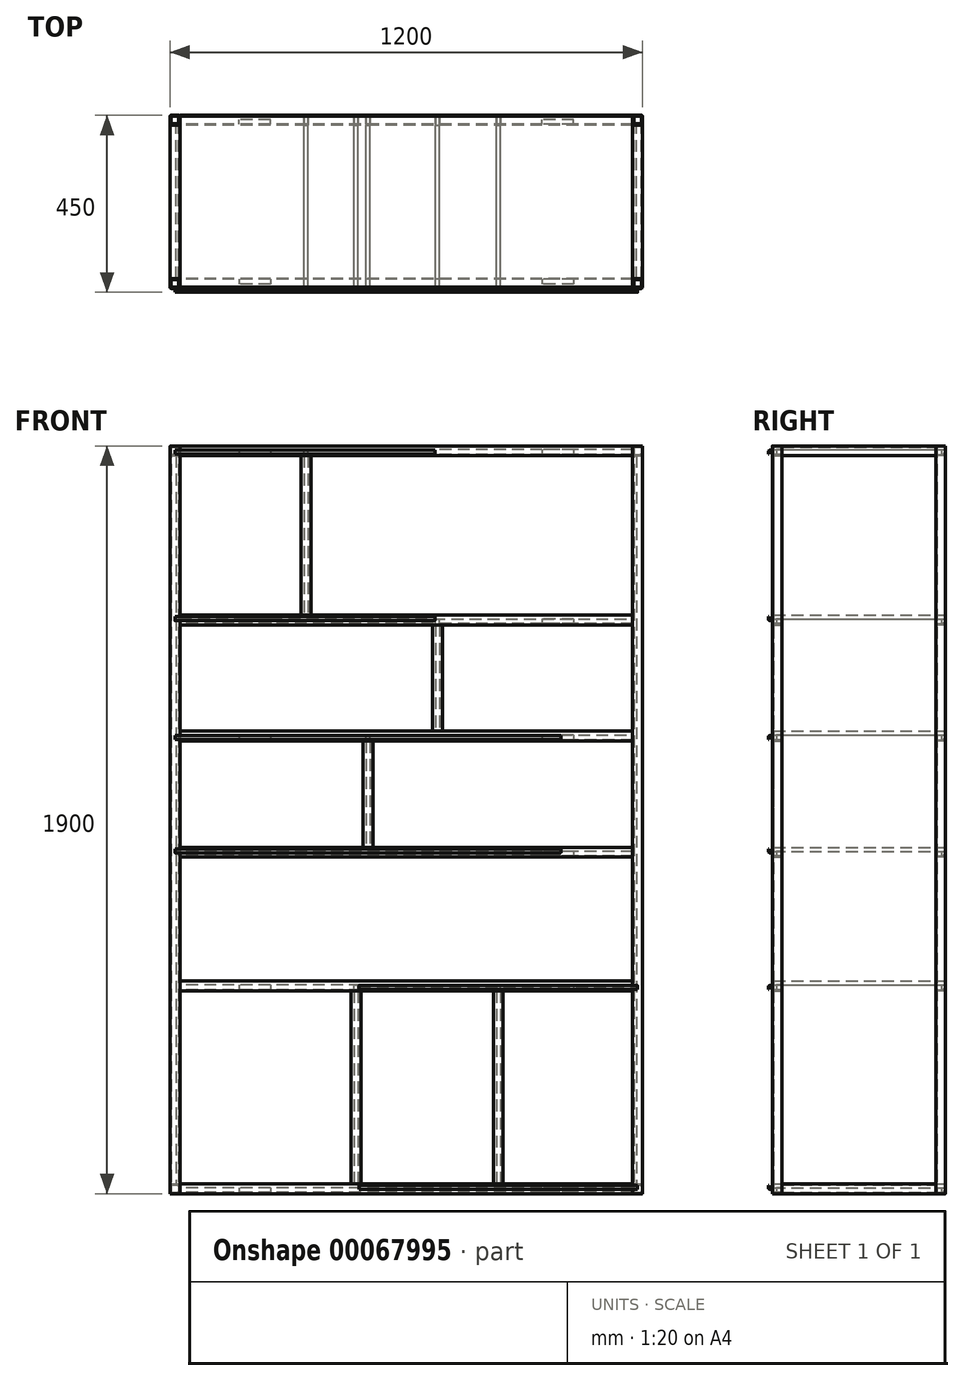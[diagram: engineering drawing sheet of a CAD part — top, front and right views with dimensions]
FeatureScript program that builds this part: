
annotation { "Feature Type Name" : "Feature", "Feature Type Description" : "" }
export const myFeature = defineFeature(function(context is Context, id is Id, definition is map)
    precondition{}
    {
        {
            var Q0;
            Q0=qCreatedBy(makeId("Top.planeOp"),FACE);
            var sketch = newSketch(context, id + "F0", { "sketchPlane" : qUnion([Q0])});
            skLineSegment(sketch, "E0.bottom", {"start": v(-9.5, 12.5) * mm, "end": v(9.5, 12.5) * mm});
            skLineSegment(sketch, "E0.top", {"start": v(-9.5, -12.5) * mm, "end": v(9.5, -12.5) * mm});
            skLineSegment(sketch, "E0.left", {"start": v(-12.5, 9.5) * mm, "end": v(-12.5, -9.5) * mm});
            skLineSegment(sketch, "E0.right", {"start": v(12.5, 9.5) * mm, "end": v(12.5, -9.5) * mm});
            skLineSegment(sketch, "E1.bottom", {"start": v(-6.5, 9.5) * mm, "end": v(6.5, 9.5) * mm});
            skLineSegment(sketch, "E1.top", {"start": v(-6.5, -9.5) * mm, "end": v(6.5, -9.5) * mm});
            skLineSegment(sketch, "E1.left", {"start": v(-9.5, 6.5) * mm, "end": v(-9.5, -6.5) * mm});
            skLineSegment(sketch, "E1.right", {"start": v(9.5, 6.5) * mm, "end": v(9.5, -6.5) * mm});
            skPoint(sketch, "E2.visualSharp", {"position": v(-12.5, 12.5) * mm});
            skArc(sketch, "E2.filletArc", {"start": v(-9.5, 12.5) * mm, "mid": v(-11.62, 11.62) * mm, "end": v(-12.5, 9.5) * mm});
            skPoint(sketch, "E3.visualSharp", {"position": v(12.5, 12.5) * mm});
            skArc(sketch, "E3.filletArc", {"start": v(12.5, 9.5) * mm, "mid": v(11.62, 11.62) * mm, "end": v(9.5, 12.5) * mm});
            skPoint(sketch, "E4.visualSharp", {"position": v(12.5, -12.5) * mm});
            skArc(sketch, "E4.filletArc", {"start": v(9.5, -12.5) * mm, "mid": v(11.62, -11.62) * mm, "end": v(12.5, -9.5) * mm});
            skPoint(sketch, "E5.visualSharp", {"position": v(-12.5, -12.5) * mm});
            skArc(sketch, "E5.filletArc", {"start": v(-12.5, -9.5) * mm, "mid": v(-11.62, -11.62) * mm, "end": v(-9.5, -12.5) * mm});
            skArc(sketch, "E6.filletArc", {"start": v(-6.5, 9.5) * mm, "mid": v(-8.62, 8.62) * mm, "end": v(-9.5, 6.5) * mm});
            skArc(sketch, "E7.filletArc", {"start": v(6.5, -9.5) * mm, "mid": v(8.62, -8.62) * mm, "end": v(9.5, -6.5) * mm});
            skArc(sketch, "E8.filletArc", {"start": v(9.5, 6.5) * mm, "mid": v(8.62, 8.62) * mm, "end": v(6.5, 9.5) * mm});
            skArc(sketch, "E9.filletArc", {"start": v(-9.5, -6.5) * mm, "mid": v(-8.62, -8.62) * mm, "end": v(-6.5, -9.5) * mm});
            skSolve(sketch);
        }
        {
            var Q0;
            Q0=makeQuery(id+"F0.imprint","IMPRINT",FACE,{"disambiguationData":[TD([[makeQuery(id+"F0.imprint","IMPRINT",EDGE,{"derivedFrom":sQuery(id+"F0.wireOp",EDGE,"E0.bottom")}),-1.0]])]});
            extrude(context, id + "F1", {"entities" : qUnion([Q0]), "depth" : 1900 * mm});
        }
        {
            var Q0;
            Q0=makeQuery(id+"F1.opExtrude","SWEPT_BODY",BODY,{"disambiguationData":[OSD([sQuery(id+"F0.wireOp",EDGE,"E0.bottom"),sQuery(id+"F0.wireOp",EDGE,"E0.top"),sQuery(id+"F0.wireOp",EDGE,"E0.left"),sQuery(id+"F0.wireOp",EDGE,"E0.right"),sQuery(id+"F0.wireOp",EDGE,"E1.bottom"),sQuery(id+"F0.wireOp",EDGE,"E1.top"),sQuery(id+"F0.wireOp",EDGE,"E1.left"),sQuery(id+"F0.wireOp",EDGE,"E1.right"),sQuery(id+"F0.wireOp",EDGE,"E2.filletArc"),sQuery(id+"F0.wireOp",EDGE,"E3.filletArc"),sQuery(id+"F0.wireOp",EDGE,"E4.filletArc"),sQuery(id+"F0.wireOp",EDGE,"E5.filletArc"),sQuery(id+"F0.wireOp",EDGE,"E6.filletArc"),sQuery(id+"F0.wireOp",EDGE,"E7.filletArc"),sQuery(id+"F0.wireOp",EDGE,"E8.filletArc"),sQuery(id+"F0.wireOp",EDGE,"E9.filletArc")])]});
            transform(context, id + "F2", {"entities" : qUnion([Q0]), "transformType" : TransformType.TRANSLATION_3D, "dx" : 415 * mm, "dy" : 0 * mm, "dz" : 0 * mm, "makeCopy" : true});
        }
        {
            var Q0;
            Q0=makeQuery(id+"F1.opExtrude","SWEPT_BODY",BODY,{"disambiguationData":[OSD([sQuery(id+"F0.wireOp",EDGE,"E0.bottom"),sQuery(id+"F0.wireOp",EDGE,"E0.top"),sQuery(id+"F0.wireOp",EDGE,"E0.left"),sQuery(id+"F0.wireOp",EDGE,"E0.right"),sQuery(id+"F0.wireOp",EDGE,"E1.bottom"),sQuery(id+"F0.wireOp",EDGE,"E1.top"),sQuery(id+"F0.wireOp",EDGE,"E1.left"),sQuery(id+"F0.wireOp",EDGE,"E1.right"),sQuery(id+"F0.wireOp",EDGE,"E2.filletArc"),sQuery(id+"F0.wireOp",EDGE,"E3.filletArc"),sQuery(id+"F0.wireOp",EDGE,"E4.filletArc"),sQuery(id+"F0.wireOp",EDGE,"E5.filletArc"),sQuery(id+"F0.wireOp",EDGE,"E6.filletArc"),sQuery(id+"F0.wireOp",EDGE,"E7.filletArc"),sQuery(id+"F0.wireOp",EDGE,"E8.filletArc"),sQuery(id+"F0.wireOp",EDGE,"E9.filletArc")])]});
            var Q1;
            Q1=makeQuery(id+"F2.opPattern","COPY",BODY,{"derivedFrom":makeQuery(id+"F1.opExtrude","SWEPT_BODY",BODY,{"disambiguationData":[OSD([sQuery(id+"F0.wireOp",EDGE,"E0.bottom"),sQuery(id+"F0.wireOp",EDGE,"E0.top"),sQuery(id+"F0.wireOp",EDGE,"E0.left"),sQuery(id+"F0.wireOp",EDGE,"E0.right"),sQuery(id+"F0.wireOp",EDGE,"E1.bottom"),sQuery(id+"F0.wireOp",EDGE,"E1.top"),sQuery(id+"F0.wireOp",EDGE,"E1.left"),sQuery(id+"F0.wireOp",EDGE,"E1.right"),sQuery(id+"F0.wireOp",EDGE,"E2.filletArc"),sQuery(id+"F0.wireOp",EDGE,"E3.filletArc"),sQuery(id+"F0.wireOp",EDGE,"E4.filletArc"),sQuery(id+"F0.wireOp",EDGE,"E5.filletArc"),sQuery(id+"F0.wireOp",EDGE,"E6.filletArc"),sQuery(id+"F0.wireOp",EDGE,"E7.filletArc"),sQuery(id+"F0.wireOp",EDGE,"E8.filletArc"),sQuery(id+"F0.wireOp",EDGE,"E9.filletArc")])]}),"instanceName":"1"});
            transform(context, id + "F3", {"entities" : qUnion([Q0, Q1]), "transformType" : TransformType.TRANSLATION_3D, "dx" : 0 * mm, "dy" : 1175 * mm, "dz" : 0 * mm, "makeCopy" : true});
        }
        {
            var Q0;
            Q0=makeQuery(id+"F2.opPattern","COPY",FACE,{"derivedFrom":makeQuery(id+"F1.opExtrude","SWEPT_FACE",FACE,{"disambiguationData":[OSD([sQuery(id+"F0.wireOp",EDGE,"E0.left")])]}),"instanceName":"1"});
            var sketch = newSketch(context, id + "F4", { "sketchPlane" : qUnion([Q0])});
            skSolve(sketch);
        }
        {
            var Q0;
            {var subQ0=sQuery(id+"F0.wireOp",EDGE,"E0.left");Q0=makeQuery(id+"F4.imprint","IMPRINT",FACE,{"disambiguationData":[TD([[makeQuery(id+"F4.imprint","IMPRINT",EDGE,{"derivedFrom":makeQuery(id+"F2.opPattern","COPY",EDGE,{"derivedFrom":makeQuery(id+"F1.opExtrude","CAP_EDGE",EDGE,{"disambiguationData":[OSD([subQ0])],"isStart":true}),"instanceName":"1"})}),1.0]])]});}
            var sketch = newSketch(context, id + "F5", { "sketchPlane" : qUnion([Q0])});
            skLineSegment(sketch, "E10.bottom", {"start": v(-9.5, 1900) * mm, "end": v(9.5, 1900) * mm});
            skLineSegment(sketch, "E10.top", {"start": v(-9.5, 1875) * mm, "end": v(9.5, 1875) * mm});
            skLineSegment(sketch, "E10.left", {"start": v(-12.5, 1897) * mm, "end": v(-12.5, 1878) * mm});
            skLineSegment(sketch, "E10.right", {"start": v(12.5, 1897) * mm, "end": v(12.5, 1878) * mm});
            skLineSegment(sketch, "E11.bottom", {"start": v(-6.5, 1897) * mm, "end": v(6.5, 1897) * mm});
            skLineSegment(sketch, "E11.top", {"start": v(-6.5, 1878) * mm, "end": v(6.5, 1878) * mm});
            skLineSegment(sketch, "E11.left", {"start": v(-9.5, 1894) * mm, "end": v(-9.5, 1881) * mm});
            skLineSegment(sketch, "E11.right", {"start": v(9.5, 1894) * mm, "end": v(9.5, 1881) * mm});
            skPoint(sketch, "E12.visualSharp", {"position": v(-12.5, 1900) * mm});
            skArc(sketch, "E12.filletArc", {"start": v(-9.5, 1900) * mm, "mid": v(-11.62, 1899.12) * mm, "end": v(-12.5, 1897) * mm});
            skPoint(sketch, "E13.visualSharp", {"position": v(12.5, 1900) * mm});
            skArc(sketch, "E13.filletArc", {"start": v(12.5, 1897) * mm, "mid": v(11.62, 1899.12) * mm, "end": v(9.5, 1900) * mm});
            skPoint(sketch, "E14.visualSharp", {"position": v(12.5, 1875) * mm});
            skArc(sketch, "E14.filletArc", {"start": v(9.5, 1875) * mm, "mid": v(11.62, 1875.88) * mm, "end": v(12.5, 1878) * mm});
            skPoint(sketch, "E15.visualSharp", {"position": v(-12.5, 1875) * mm});
            skArc(sketch, "E15.filletArc", {"start": v(-12.5, 1878) * mm, "mid": v(-11.62, 1875.88) * mm, "end": v(-9.5, 1875) * mm});
            skArc(sketch, "E16.filletArc", {"start": v(-9.5, 1881) * mm, "mid": v(-8.62, 1878.88) * mm, "end": v(-6.5, 1878) * mm});
            skArc(sketch, "E17.filletArc", {"start": v(-6.5, 1897) * mm, "mid": v(-8.62, 1896.12) * mm, "end": v(-9.5, 1894) * mm});
            skArc(sketch, "E18.filletArc", {"start": v(9.5, 1894) * mm, "mid": v(8.62, 1896.12) * mm, "end": v(6.5, 1897) * mm});
            skArc(sketch, "E19.filletArc", {"start": v(6.5, 1878) * mm, "mid": v(8.62, 1878.88) * mm, "end": v(9.5, 1881) * mm});
            skSolve(sketch);
        }
        {
            var Q0;
            {var subQ2=sQuery(id+"F5.wireOp",EDGE,"E10.bottom");Q0=makeQuery(id+"F5.imprint","IMPRINT",FACE,{"disambiguationData":[TD([[makeQuery(id+"F5.imprint","IMPRINT",EDGE,{"derivedFrom":subQ2}),-1.0]])]});}
            var Q1;
            Q1=makeQuery(id+"F5.imprint","IMPRINT",FACE,{"disambiguationData":[TD([[makeQuery(id+"F5.imprint","IMPRINT",EDGE,{"derivedFrom":sQuery(id+"F5.wireOp",EDGE,"E10.right")}),-1.0]])]});
            var Q2;
            {var subQ2=sQuery(id+"F5.wireOp",EDGE,"E10.top");Q2=makeQuery(id+"F5.imprint","IMPRINT",FACE,{"disambiguationData":[TD([[makeQuery(id+"F5.imprint","IMPRINT",EDGE,{"derivedFrom":subQ2}),1.0]])]});}
            var Q3;
            Q3=makeQuery(id+"F5.imprint","IMPRINT",FACE,{"disambiguationData":[TD([[makeQuery(id+"F5.imprint","IMPRINT",EDGE,{"derivedFrom":sQuery(id+"F5.wireOp",EDGE,"E10.left")}),1.0]])]});
            extrude(context, id + "F6", {"entities" : qUnion([Q0, Q1, Q2, Q3]), "depth" : 390 * mm});
        }
        {
            var Q0;
            Q0=makeQuery(id+"F6.opExtrude","SWEPT_BODY",BODY,{"disambiguationData":[OSD([sQuery(id+"F5.wireOp",EDGE,"E10.bottom"),sQuery(id+"F5.wireOp",EDGE,"E10.top"),sQuery(id+"F5.wireOp",EDGE,"E10.left"),sQuery(id+"F5.wireOp",EDGE,"E10.right"),sQuery(id+"F5.wireOp",EDGE,"E11.bottom"),sQuery(id+"F5.wireOp",EDGE,"E11.top"),sQuery(id+"F5.wireOp",EDGE,"E11.left"),sQuery(id+"F5.wireOp",EDGE,"E11.right"),sQuery(id+"F5.wireOp",EDGE,"E12.filletArc"),sQuery(id+"F5.wireOp",EDGE,"E13.filletArc"),sQuery(id+"F5.wireOp",EDGE,"E14.filletArc"),sQuery(id+"F5.wireOp",EDGE,"E15.filletArc"),sQuery(id+"F5.wireOp",EDGE,"E16.filletArc"),sQuery(id+"F5.wireOp",EDGE,"E17.filletArc"),sQuery(id+"F5.wireOp",EDGE,"E18.filletArc"),sQuery(id+"F5.wireOp",EDGE,"E19.filletArc")])]});
            transform(context, id + "F7", {"entities" : qUnion([Q0]), "transformType" : TransformType.TRANSLATION_3D, "dx" : 0 * mm, "dy" : 1175 * mm, "dz" : 0 * mm, "makeCopy" : true});
        }
        {
            var Q0;
            Q0=makeQuery(id+"F6.opExtrude","SWEPT_BODY",BODY,{"disambiguationData":[OSD([sQuery(id+"F5.wireOp",EDGE,"E10.bottom"),sQuery(id+"F5.wireOp",EDGE,"E10.top"),sQuery(id+"F5.wireOp",EDGE,"E10.left"),sQuery(id+"F5.wireOp",EDGE,"E10.right"),sQuery(id+"F5.wireOp",EDGE,"E11.bottom"),sQuery(id+"F5.wireOp",EDGE,"E11.top"),sQuery(id+"F5.wireOp",EDGE,"E11.left"),sQuery(id+"F5.wireOp",EDGE,"E11.right"),sQuery(id+"F5.wireOp",EDGE,"E12.filletArc"),sQuery(id+"F5.wireOp",EDGE,"E13.filletArc"),sQuery(id+"F5.wireOp",EDGE,"E14.filletArc"),sQuery(id+"F5.wireOp",EDGE,"E15.filletArc"),sQuery(id+"F5.wireOp",EDGE,"E16.filletArc"),sQuery(id+"F5.wireOp",EDGE,"E17.filletArc"),sQuery(id+"F5.wireOp",EDGE,"E18.filletArc"),sQuery(id+"F5.wireOp",EDGE,"E19.filletArc")])]});
            var Q1;
            Q1=makeQuery(id+"F7.opPattern","COPY",BODY,{"derivedFrom":makeQuery(id+"F6.opExtrude","SWEPT_BODY",BODY,{"disambiguationData":[OSD([sQuery(id+"F5.wireOp",EDGE,"E10.bottom"),sQuery(id+"F5.wireOp",EDGE,"E10.top"),sQuery(id+"F5.wireOp",EDGE,"E10.left"),sQuery(id+"F5.wireOp",EDGE,"E10.right"),sQuery(id+"F5.wireOp",EDGE,"E11.bottom"),sQuery(id+"F5.wireOp",EDGE,"E11.top"),sQuery(id+"F5.wireOp",EDGE,"E11.left"),sQuery(id+"F5.wireOp",EDGE,"E11.right"),sQuery(id+"F5.wireOp",EDGE,"E12.filletArc"),sQuery(id+"F5.wireOp",EDGE,"E13.filletArc"),sQuery(id+"F5.wireOp",EDGE,"E14.filletArc"),sQuery(id+"F5.wireOp",EDGE,"E15.filletArc"),sQuery(id+"F5.wireOp",EDGE,"E16.filletArc"),sQuery(id+"F5.wireOp",EDGE,"E17.filletArc"),sQuery(id+"F5.wireOp",EDGE,"E18.filletArc"),sQuery(id+"F5.wireOp",EDGE,"E19.filletArc")])]}),"instanceName":"1"});
            transform(context, id + "F8", {"entities" : qUnion([Q0, Q1]), "transformType" : TransformType.TRANSLATION_3D, "dx" : 0 * mm, "dy" : 0 * mm, "dz" : -1875 * mm, "makeCopy" : true});
        }
        {
            var Q0;
            Q0=makeQuery(id+"F2.opPattern","COPY",FACE,{"derivedFrom":makeQuery(id+"F1.opExtrude","SWEPT_FACE",FACE,{"disambiguationData":[OSD([sQuery(id+"F0.wireOp",EDGE,"E0.bottom")])]}),"instanceName":"1"});
            var sketch = newSketch(context, id + "F9", { "sketchPlane" : qUnion([Q0])});
            skLineSegment(sketch, "E20", {"start": v(-427.5, 1900) * mm, "end": v(-427.5, 1875) * mm});
            skLineSegment(sketch, "E21", {"start": v(-427.5, 1875) * mm, "end": v(-402.5, 1875) * mm});
            skLineSegment(sketch, "E22", {"start": v(-402.5, 1875) * mm, "end": v(-402.5, 1876) * mm});
            skLineSegment(sketch, "E23", {"start": v(-404.5, 1878) * mm, "end": v(-419.5, 1878) * mm});
            skLineSegment(sketch, "E24", {"start": v(-424.5, 1883) * mm, "end": v(-424.5, 1898) * mm});
            skLineSegment(sketch, "E25", {"start": v(-426.5, 1900) * mm, "end": v(-427.5, 1900) * mm});
            skPoint(sketch, "E26.visualSharp", {"position": v(-424.5, 1878) * mm});
            skArc(sketch, "E26.filletArc", {"start": v(-424.5, 1883) * mm, "mid": v(-423.04, 1879.46) * mm, "end": v(-419.5, 1878) * mm});
            skPoint(sketch, "E27.visualSharp", {"position": v(-424.5, 1900) * mm});
            skArc(sketch, "E27.filletArc", {"start": v(-424.5, 1898) * mm, "mid": v(-425.09, 1899.41) * mm, "end": v(-426.5, 1900) * mm});
            skPoint(sketch, "E28.visualSharp", {"position": v(-402.5, 1878) * mm});
            skArc(sketch, "E28.filletArc", {"start": v(-402.5, 1876) * mm, "mid": v(-403.09, 1877.41) * mm, "end": v(-404.5, 1878) * mm});
            skSolve(sketch);
        }
        {
            var Q0;
            {var subQ4=sQuery(id+"F9.wireOp",EDGE,"E22");Q0=makeQuery(id+"F9.imprint","IMPRINT",FACE,{"disambiguationData":[TD([[makeQuery(id+"F9.imprint","IMPRINT",EDGE,{"derivedFrom":subQ4}),1.0]])]});}
            var Q1;
            {var subQ0=sQuery(id+"F9.wireOp",EDGE,"E26.filletArc");Q1=makeQuery(id+"F9.imprint","IMPRINT",FACE,{"disambiguationData":[TD([[makeQuery(id+"F9.imprint","IMPRINT",EDGE,{"derivedFrom":subQ0}),-1.0]])]});}
            var Q2;
            {var subQ4=sQuery(id+"F9.wireOp",EDGE,"E20");Q2=makeQuery(id+"F9.imprint","IMPRINT",FACE,{"disambiguationData":[TD([[makeQuery(id+"F9.imprint","IMPRINT",EDGE,{"derivedFrom":subQ4}),1.0]])]});}
            extrude(context, id + "F10", {"entities" : qUnion([Q0, Q1, Q2]), "depth" : 1150 * mm});
        }
        {
            var Q0;
            Q0=makeQuery(id+"F10.opExtrude","SWEPT_BODY",BODY,{"disambiguationData":[OSD([sQuery(id+"F9.wireOp",EDGE,"E20"),sQuery(id+"F9.wireOp",EDGE,"E21"),sQuery(id+"F9.wireOp",EDGE,"E22"),sQuery(id+"F9.wireOp",EDGE,"E23"),sQuery(id+"F9.wireOp",EDGE,"E24"),sQuery(id+"F9.wireOp",EDGE,"E25"),sQuery(id+"F9.wireOp",EDGE,"E26.filletArc"),sQuery(id+"F9.wireOp",EDGE,"E27.filletArc"),sQuery(id+"F9.wireOp",EDGE,"E28.filletArc")])]});
            var Q1;
            Q1=makeQuery(id+"F10.opExtrude","SWEPT_FACE",FACE,{"disambiguationData":[OSD([sQuery(id+"F9.wireOp",EDGE,"E22")])]});
            mirror(context, id + "F11", {"entities" : qUnion([Q0]), "mirrorPlane" : qUnion([Q1])});
        }
        {
            var Q0;
            Q0=makeQuery(id+"F11.opPattern","COPY",BODY,{"derivedFrom":makeQuery(id+"F10.opExtrude","SWEPT_BODY",BODY,{"disambiguationData":[OSD([sQuery(id+"F9.wireOp",EDGE,"E20"),sQuery(id+"F9.wireOp",EDGE,"E21"),sQuery(id+"F9.wireOp",EDGE,"E22"),sQuery(id+"F9.wireOp",EDGE,"E23"),sQuery(id+"F9.wireOp",EDGE,"E24"),sQuery(id+"F9.wireOp",EDGE,"E25"),sQuery(id+"F9.wireOp",EDGE,"E26.filletArc"),sQuery(id+"F9.wireOp",EDGE,"E27.filletArc"),sQuery(id+"F9.wireOp",EDGE,"E28.filletArc")])]}),"instanceName":"1"});
            transform(context, id + "F12", {"entities" : qUnion([Q0]), "transformType" : TransformType.TRANSLATION_3D, "dx" : -390 * mm, "dy" : 0 * mm, "dz" : 0 * mm, "makeCopy" : false});
        }
        {
            var Q0;
            Q0=makeQuery(id+"F10.opExtrude","SWEPT_BODY",BODY,{"disambiguationData":[OSD([sQuery(id+"F9.wireOp",EDGE,"E20"),sQuery(id+"F9.wireOp",EDGE,"E21"),sQuery(id+"F9.wireOp",EDGE,"E22"),sQuery(id+"F9.wireOp",EDGE,"E23"),sQuery(id+"F9.wireOp",EDGE,"E24"),sQuery(id+"F9.wireOp",EDGE,"E25"),sQuery(id+"F9.wireOp",EDGE,"E26.filletArc"),sQuery(id+"F9.wireOp",EDGE,"E27.filletArc"),sQuery(id+"F9.wireOp",EDGE,"E28.filletArc")])]});
            var Q1;
            Q1=makeQuery(id+"F11.opPattern","COPY",BODY,{"derivedFrom":makeQuery(id+"F10.opExtrude","SWEPT_BODY",BODY,{"disambiguationData":[OSD([sQuery(id+"F9.wireOp",EDGE,"E20"),sQuery(id+"F9.wireOp",EDGE,"E21"),sQuery(id+"F9.wireOp",EDGE,"E22"),sQuery(id+"F9.wireOp",EDGE,"E23"),sQuery(id+"F9.wireOp",EDGE,"E24"),sQuery(id+"F9.wireOp",EDGE,"E25"),sQuery(id+"F9.wireOp",EDGE,"E26.filletArc"),sQuery(id+"F9.wireOp",EDGE,"E27.filletArc"),sQuery(id+"F9.wireOp",EDGE,"E28.filletArc")])]}),"instanceName":"1"});
            transform(context, id + "F13", {"entities" : qUnion([Q0, Q1]), "transformType" : TransformType.TRANSLATION_3D, "dx" : 0 * mm, "dy" : 0 * mm, "dz" : -1875 * mm, "makeCopy" : false});
        }
        {
            var Q0;
            Q0=makeQuery(id+"F10.opExtrude","SWEPT_BODY",BODY,{"disambiguationData":[OSD([sQuery(id+"F9.wireOp",EDGE,"E20"),sQuery(id+"F9.wireOp",EDGE,"E21"),sQuery(id+"F9.wireOp",EDGE,"E22"),sQuery(id+"F9.wireOp",EDGE,"E23"),sQuery(id+"F9.wireOp",EDGE,"E24"),sQuery(id+"F9.wireOp",EDGE,"E25"),sQuery(id+"F9.wireOp",EDGE,"E26.filletArc"),sQuery(id+"F9.wireOp",EDGE,"E27.filletArc"),sQuery(id+"F9.wireOp",EDGE,"E28.filletArc")])]});
            var Q1;
            Q1=makeQuery(id+"F11.opPattern","COPY",BODY,{"derivedFrom":makeQuery(id+"F10.opExtrude","SWEPT_BODY",BODY,{"disambiguationData":[OSD([sQuery(id+"F9.wireOp",EDGE,"E20"),sQuery(id+"F9.wireOp",EDGE,"E21"),sQuery(id+"F9.wireOp",EDGE,"E22"),sQuery(id+"F9.wireOp",EDGE,"E23"),sQuery(id+"F9.wireOp",EDGE,"E24"),sQuery(id+"F9.wireOp",EDGE,"E25"),sQuery(id+"F9.wireOp",EDGE,"E26.filletArc"),sQuery(id+"F9.wireOp",EDGE,"E27.filletArc"),sQuery(id+"F9.wireOp",EDGE,"E28.filletArc")])]}),"instanceName":"1"});
            transform(context, id + "F14", {"entities" : qUnion([Q0, Q1]), "transformType" : TransformType.TRANSLATION_3D, "dx" : 0 * mm, "dy" : 0 * mm, "dz" : 515 * mm, "makeCopy" : true});
        }
        {
            var Q0;
            Q0=makeQuery(id+"F14.opPattern","COPY",BODY,{"derivedFrom":makeQuery(id+"F10.opExtrude","SWEPT_BODY",BODY,{"disambiguationData":[OSD([sQuery(id+"F9.wireOp",EDGE,"E20"),sQuery(id+"F9.wireOp",EDGE,"E21"),sQuery(id+"F9.wireOp",EDGE,"E22"),sQuery(id+"F9.wireOp",EDGE,"E23"),sQuery(id+"F9.wireOp",EDGE,"E24"),sQuery(id+"F9.wireOp",EDGE,"E25"),sQuery(id+"F9.wireOp",EDGE,"E26.filletArc"),sQuery(id+"F9.wireOp",EDGE,"E27.filletArc"),sQuery(id+"F9.wireOp",EDGE,"E28.filletArc")])]}),"instanceName":"1"});
            var Q1;
            Q1=makeQuery(id+"F14.opPattern","COPY",BODY,{"derivedFrom":makeQuery(id+"F11.opPattern","COPY",BODY,{"derivedFrom":makeQuery(id+"F10.opExtrude","SWEPT_BODY",BODY,{"disambiguationData":[OSD([sQuery(id+"F9.wireOp",EDGE,"E20"),sQuery(id+"F9.wireOp",EDGE,"E21"),sQuery(id+"F9.wireOp",EDGE,"E22"),sQuery(id+"F9.wireOp",EDGE,"E23"),sQuery(id+"F9.wireOp",EDGE,"E24"),sQuery(id+"F9.wireOp",EDGE,"E25"),sQuery(id+"F9.wireOp",EDGE,"E26.filletArc"),sQuery(id+"F9.wireOp",EDGE,"E27.filletArc"),sQuery(id+"F9.wireOp",EDGE,"E28.filletArc")])]}),"instanceName":"1"}),"instanceName":"1"});
            transform(context, id + "F15", {"entities" : qUnion([Q0, Q1]), "transformType" : TransformType.TRANSLATION_3D, "dx" : 0 * mm, "dy" : 0 * mm, "dz" : 340 * mm, "makeCopy" : true});
        }
        {
            var Q0;
            Q0=makeQuery(id+"F15.opPattern","COPY",BODY,{"derivedFrom":makeQuery(id+"F14.opPattern","COPY",BODY,{"derivedFrom":makeQuery(id+"F10.opExtrude","SWEPT_BODY",BODY,{"disambiguationData":[OSD([sQuery(id+"F9.wireOp",EDGE,"E20"),sQuery(id+"F9.wireOp",EDGE,"E21"),sQuery(id+"F9.wireOp",EDGE,"E22"),sQuery(id+"F9.wireOp",EDGE,"E23"),sQuery(id+"F9.wireOp",EDGE,"E24"),sQuery(id+"F9.wireOp",EDGE,"E25"),sQuery(id+"F9.wireOp",EDGE,"E26.filletArc"),sQuery(id+"F9.wireOp",EDGE,"E27.filletArc"),sQuery(id+"F9.wireOp",EDGE,"E28.filletArc")])]}),"instanceName":"1"}),"instanceName":"1"});
            var Q1;
            Q1=makeQuery(id+"F15.opPattern","COPY",BODY,{"derivedFrom":makeQuery(id+"F14.opPattern","COPY",BODY,{"derivedFrom":makeQuery(id+"F11.opPattern","COPY",BODY,{"derivedFrom":makeQuery(id+"F10.opExtrude","SWEPT_BODY",BODY,{"disambiguationData":[OSD([sQuery(id+"F9.wireOp",EDGE,"E20"),sQuery(id+"F9.wireOp",EDGE,"E21"),sQuery(id+"F9.wireOp",EDGE,"E22"),sQuery(id+"F9.wireOp",EDGE,"E23"),sQuery(id+"F9.wireOp",EDGE,"E24"),sQuery(id+"F9.wireOp",EDGE,"E25"),sQuery(id+"F9.wireOp",EDGE,"E26.filletArc"),sQuery(id+"F9.wireOp",EDGE,"E27.filletArc"),sQuery(id+"F9.wireOp",EDGE,"E28.filletArc")])]}),"instanceName":"1"}),"instanceName":"1"}),"instanceName":"1"});
            transform(context, id + "F16", {"entities" : qUnion([Q0, Q1]), "transformType" : TransformType.TRANSLATION_3D, "dx" : 0 * mm, "dy" : 0 * mm, "dz" : 295 * mm, "makeCopy" : true});
        }
        {
            var Q0;
            Q0=makeQuery(id+"F16.opPattern","COPY",BODY,{"derivedFrom":makeQuery(id+"F15.opPattern","COPY",BODY,{"derivedFrom":makeQuery(id+"F14.opPattern","COPY",BODY,{"derivedFrom":makeQuery(id+"F10.opExtrude","SWEPT_BODY",BODY,{"disambiguationData":[OSD([sQuery(id+"F9.wireOp",EDGE,"E20"),sQuery(id+"F9.wireOp",EDGE,"E21"),sQuery(id+"F9.wireOp",EDGE,"E22"),sQuery(id+"F9.wireOp",EDGE,"E23"),sQuery(id+"F9.wireOp",EDGE,"E24"),sQuery(id+"F9.wireOp",EDGE,"E25"),sQuery(id+"F9.wireOp",EDGE,"E26.filletArc"),sQuery(id+"F9.wireOp",EDGE,"E27.filletArc"),sQuery(id+"F9.wireOp",EDGE,"E28.filletArc")])]}),"instanceName":"1"}),"instanceName":"1"}),"instanceName":"1"});
            var Q1;
            Q1=makeQuery(id+"F16.opPattern","COPY",BODY,{"derivedFrom":makeQuery(id+"F15.opPattern","COPY",BODY,{"derivedFrom":makeQuery(id+"F14.opPattern","COPY",BODY,{"derivedFrom":makeQuery(id+"F11.opPattern","COPY",BODY,{"derivedFrom":makeQuery(id+"F10.opExtrude","SWEPT_BODY",BODY,{"disambiguationData":[OSD([sQuery(id+"F9.wireOp",EDGE,"E20"),sQuery(id+"F9.wireOp",EDGE,"E21"),sQuery(id+"F9.wireOp",EDGE,"E22"),sQuery(id+"F9.wireOp",EDGE,"E23"),sQuery(id+"F9.wireOp",EDGE,"E24"),sQuery(id+"F9.wireOp",EDGE,"E25"),sQuery(id+"F9.wireOp",EDGE,"E26.filletArc"),sQuery(id+"F9.wireOp",EDGE,"E27.filletArc"),sQuery(id+"F9.wireOp",EDGE,"E28.filletArc")])]}),"instanceName":"1"}),"instanceName":"1"}),"instanceName":"1"}),"instanceName":"1"});
            transform(context, id + "F17", {"entities" : qUnion([Q0, Q1]), "transformType" : TransformType.TRANSLATION_3D, "dx" : 0 * mm, "dy" : 0 * mm, "dz" : 295 * mm, "makeCopy" : true});
        }
        {
            var Q0;
            Q0=makeQuery(id+"F17.opPattern","COPY",BODY,{"derivedFrom":makeQuery(id+"F16.opPattern","COPY",BODY,{"derivedFrom":makeQuery(id+"F15.opPattern","COPY",BODY,{"derivedFrom":makeQuery(id+"F14.opPattern","COPY",BODY,{"derivedFrom":makeQuery(id+"F10.opExtrude","SWEPT_BODY",BODY,{"disambiguationData":[OSD([sQuery(id+"F9.wireOp",EDGE,"E20"),sQuery(id+"F9.wireOp",EDGE,"E21"),sQuery(id+"F9.wireOp",EDGE,"E22"),sQuery(id+"F9.wireOp",EDGE,"E23"),sQuery(id+"F9.wireOp",EDGE,"E24"),sQuery(id+"F9.wireOp",EDGE,"E25"),sQuery(id+"F9.wireOp",EDGE,"E26.filletArc"),sQuery(id+"F9.wireOp",EDGE,"E27.filletArc"),sQuery(id+"F9.wireOp",EDGE,"E28.filletArc")])]}),"instanceName":"1"}),"instanceName":"1"}),"instanceName":"1"}),"instanceName":"1"});
            var Q1;
            Q1=makeQuery(id+"F17.opPattern","COPY",BODY,{"derivedFrom":makeQuery(id+"F16.opPattern","COPY",BODY,{"derivedFrom":makeQuery(id+"F15.opPattern","COPY",BODY,{"derivedFrom":makeQuery(id+"F14.opPattern","COPY",BODY,{"derivedFrom":makeQuery(id+"F11.opPattern","COPY",BODY,{"derivedFrom":makeQuery(id+"F10.opExtrude","SWEPT_BODY",BODY,{"disambiguationData":[OSD([sQuery(id+"F9.wireOp",EDGE,"E20"),sQuery(id+"F9.wireOp",EDGE,"E21"),sQuery(id+"F9.wireOp",EDGE,"E22"),sQuery(id+"F9.wireOp",EDGE,"E23"),sQuery(id+"F9.wireOp",EDGE,"E24"),sQuery(id+"F9.wireOp",EDGE,"E25"),sQuery(id+"F9.wireOp",EDGE,"E26.filletArc"),sQuery(id+"F9.wireOp",EDGE,"E27.filletArc"),sQuery(id+"F9.wireOp",EDGE,"E28.filletArc")])]}),"instanceName":"1"}),"instanceName":"1"}),"instanceName":"1"}),"instanceName":"1"}),"instanceName":"1"});
            transform(context, id + "F18", {"entities" : qUnion([Q0, Q1]), "transformType" : TransformType.TRANSLATION_3D, "dx" : 0 * mm, "dy" : 0 * mm, "dz" : 430 * mm, "makeCopy" : true});
        }
        {
            var Q0;
            Q0=makeQuery(id+"F1.opExtrude","SWEPT_FACE",FACE,{"disambiguationData":[OSD([sQuery(id+"F0.wireOp",EDGE,"E0.bottom")])]});
            var sketch = newSketch(context, id + "F19", { "sketchPlane" : qUnion([Q0])});
            skLineSegment(sketch, "E29.bottom", {"start": v(-10.5, 1890) * mm, "end": v(4.5, 1890) * mm});
            skLineSegment(sketch, "E29.top", {"start": v(-10.5, 1878) * mm, "end": v(4.5, 1878) * mm});
            skLineSegment(sketch, "E29.left", {"start": v(-10.5, 1890) * mm, "end": v(-10.5, 1878) * mm});
            skLineSegment(sketch, "E29.right", {"start": v(4.5, 1890) * mm, "end": v(4.5, 1878) * mm});
            skSolve(sketch);
        }
        {
            var Q0;
            {var subQ0=sQuery(id+"F19.wireOp",EDGE,"E29.right");Q0=makeQuery(id+"F19.imprint","IMPRINT",FACE,{"disambiguationData":[TD([[makeQuery(id+"F19.imprint","IMPRINT",EDGE,{"derivedFrom":subQ0}),-1.0]])]});}
            var Q1;
            {var subQ0=sQuery(id+"F19.wireOp",EDGE,"E29.left");Q1=makeQuery(id+"F19.imprint","IMPRINT",FACE,{"disambiguationData":[TD([[makeQuery(id+"F19.imprint","IMPRINT",EDGE,{"derivedFrom":subQ0}),1.0]])]});}
            extrude(context, id + "F20", {"entities" : qUnion([Q0, Q1]), "depth" : 60 * mm});
        }
        {
            var Q0;
            Q0=makeQuery(id+"F20.opExtrude","SWEPT_BODY",BODY,{"disambiguationData":[OSD([sQuery(id+"F19.wireOp",EDGE,"E29.bottom"),sQuery(id+"F19.wireOp",EDGE,"E29.top"),sQuery(id+"F19.wireOp",EDGE,"E29.left"),sQuery(id+"F19.wireOp",EDGE,"E29.right")])]});
            transform(context, id + "F21", {"entities" : qUnion([Q0]), "transformType" : TransformType.TRANSLATION_3D, "dx" : 0 * mm, "dy" : 1090 * mm, "dz" : 0 * mm, "makeCopy" : true});
        }
        {
            var Q0;
            Q0=makeQuery(id+"F20.opExtrude","SWEPT_BODY",BODY,{"disambiguationData":[OSD([sQuery(id+"F19.wireOp",EDGE,"E29.bottom"),sQuery(id+"F19.wireOp",EDGE,"E29.top"),sQuery(id+"F19.wireOp",EDGE,"E29.left"),sQuery(id+"F19.wireOp",EDGE,"E29.right")])]});
            transform(context, id + "F22", {"entities" : qUnion([Q0]), "transformType" : TransformType.TRANSLATION_3D, "dx" : 0 * mm, "dy" : 363 * mm, "dz" : 0 * mm, "makeCopy" : true});
        }
        {
            var Q0;
            Q0=makeQuery(id+"F21.opPattern","COPY",BODY,{"derivedFrom":makeQuery(id+"F20.opExtrude","SWEPT_BODY",BODY,{"disambiguationData":[OSD([sQuery(id+"F19.wireOp",EDGE,"E29.bottom"),sQuery(id+"F19.wireOp",EDGE,"E29.top"),sQuery(id+"F19.wireOp",EDGE,"E29.left"),sQuery(id+"F19.wireOp",EDGE,"E29.right")])]}),"instanceName":"1"});
            transform(context, id + "F23", {"entities" : qUnion([Q0]), "transformType" : TransformType.TRANSLATION_3D, "dx" : 0 * mm, "dy" : -363 * mm, "dz" : 0 * mm, "makeCopy" : true});
        }
        {
            var Q0;
            Q0=makeQuery(id+"F22.opPattern","COPY",BODY,{"derivedFrom":makeQuery(id+"F20.opExtrude","SWEPT_BODY",BODY,{"disambiguationData":[OSD([sQuery(id+"F19.wireOp",EDGE,"E29.bottom"),sQuery(id+"F19.wireOp",EDGE,"E29.top"),sQuery(id+"F19.wireOp",EDGE,"E29.left"),sQuery(id+"F19.wireOp",EDGE,"E29.right")])]}),"instanceName":"1"});
            var Q1;
            Q1=makeQuery(id+"F20.opExtrude","SWEPT_BODY",BODY,{"disambiguationData":[OSD([sQuery(id+"F19.wireOp",EDGE,"E29.bottom"),sQuery(id+"F19.wireOp",EDGE,"E29.top"),sQuery(id+"F19.wireOp",EDGE,"E29.left"),sQuery(id+"F19.wireOp",EDGE,"E29.right")])]});
            var Q2;
            Q2=makeQuery(id+"F23.opPattern","COPY",BODY,{"derivedFrom":makeQuery(id+"F21.opPattern","COPY",BODY,{"derivedFrom":makeQuery(id+"F20.opExtrude","SWEPT_BODY",BODY,{"disambiguationData":[OSD([sQuery(id+"F19.wireOp",EDGE,"E29.bottom"),sQuery(id+"F19.wireOp",EDGE,"E29.top"),sQuery(id+"F19.wireOp",EDGE,"E29.left"),sQuery(id+"F19.wireOp",EDGE,"E29.right")])]}),"instanceName":"1"}),"instanceName":"1"});
            var Q3;
            Q3=makeQuery(id+"F21.opPattern","COPY",BODY,{"derivedFrom":makeQuery(id+"F20.opExtrude","SWEPT_BODY",BODY,{"disambiguationData":[OSD([sQuery(id+"F19.wireOp",EDGE,"E29.bottom"),sQuery(id+"F19.wireOp",EDGE,"E29.top"),sQuery(id+"F19.wireOp",EDGE,"E29.left"),sQuery(id+"F19.wireOp",EDGE,"E29.right")])]}),"instanceName":"1"});
            transform(context, id + "F24", {"entities" : qUnion([Q0, Q1, Q2, Q3]), "transformType" : TransformType.TRANSLATION_3D, "dx" : 409 * mm, "dy" : 0 * mm, "dz" : 0 * mm, "makeCopy" : true});
        }
        {
            var Q0;
            Q0=makeQuery(id+"F20.opExtrude","SWEPT_BODY",BODY,{"disambiguationData":[OSD([sQuery(id+"F19.wireOp",EDGE,"E29.bottom"),sQuery(id+"F19.wireOp",EDGE,"E29.top"),sQuery(id+"F19.wireOp",EDGE,"E29.left"),sQuery(id+"F19.wireOp",EDGE,"E29.right")])]});
            var Q1;
            Q1=makeQuery(id+"F22.opPattern","COPY",BODY,{"derivedFrom":makeQuery(id+"F20.opExtrude","SWEPT_BODY",BODY,{"disambiguationData":[OSD([sQuery(id+"F19.wireOp",EDGE,"E29.bottom"),sQuery(id+"F19.wireOp",EDGE,"E29.top"),sQuery(id+"F19.wireOp",EDGE,"E29.left"),sQuery(id+"F19.wireOp",EDGE,"E29.right")])]}),"instanceName":"1"});
            var Q2;
            Q2=makeQuery(id+"F23.opPattern","COPY",BODY,{"derivedFrom":makeQuery(id+"F21.opPattern","COPY",BODY,{"derivedFrom":makeQuery(id+"F20.opExtrude","SWEPT_BODY",BODY,{"disambiguationData":[OSD([sQuery(id+"F19.wireOp",EDGE,"E29.bottom"),sQuery(id+"F19.wireOp",EDGE,"E29.top"),sQuery(id+"F19.wireOp",EDGE,"E29.left"),sQuery(id+"F19.wireOp",EDGE,"E29.right")])]}),"instanceName":"1"}),"instanceName":"1"});
            var Q3;
            Q3=makeQuery(id+"F21.opPattern","COPY",BODY,{"derivedFrom":makeQuery(id+"F20.opExtrude","SWEPT_BODY",BODY,{"disambiguationData":[OSD([sQuery(id+"F19.wireOp",EDGE,"E29.bottom"),sQuery(id+"F19.wireOp",EDGE,"E29.top"),sQuery(id+"F19.wireOp",EDGE,"E29.left"),sQuery(id+"F19.wireOp",EDGE,"E29.right")])]}),"instanceName":"1"});
            var Q4;
            Q4=makeQuery(id+"F24.opPattern","COPY",BODY,{"derivedFrom":makeQuery(id+"F21.opPattern","COPY",BODY,{"derivedFrom":makeQuery(id+"F20.opExtrude","SWEPT_BODY",BODY,{"disambiguationData":[OSD([sQuery(id+"F19.wireOp",EDGE,"E29.bottom"),sQuery(id+"F19.wireOp",EDGE,"E29.top"),sQuery(id+"F19.wireOp",EDGE,"E29.left"),sQuery(id+"F19.wireOp",EDGE,"E29.right")])]}),"instanceName":"1"}),"instanceName":"1"});
            var Q5;
            Q5=makeQuery(id+"F24.opPattern","COPY",BODY,{"derivedFrom":makeQuery(id+"F23.opPattern","COPY",BODY,{"derivedFrom":makeQuery(id+"F21.opPattern","COPY",BODY,{"derivedFrom":makeQuery(id+"F20.opExtrude","SWEPT_BODY",BODY,{"disambiguationData":[OSD([sQuery(id+"F19.wireOp",EDGE,"E29.bottom"),sQuery(id+"F19.wireOp",EDGE,"E29.top"),sQuery(id+"F19.wireOp",EDGE,"E29.left"),sQuery(id+"F19.wireOp",EDGE,"E29.right")])]}),"instanceName":"1"}),"instanceName":"1"}),"instanceName":"1"});
            var Q6;
            Q6=makeQuery(id+"F24.opPattern","COPY",BODY,{"derivedFrom":makeQuery(id+"F22.opPattern","COPY",BODY,{"derivedFrom":makeQuery(id+"F20.opExtrude","SWEPT_BODY",BODY,{"disambiguationData":[OSD([sQuery(id+"F19.wireOp",EDGE,"E29.bottom"),sQuery(id+"F19.wireOp",EDGE,"E29.top"),sQuery(id+"F19.wireOp",EDGE,"E29.left"),sQuery(id+"F19.wireOp",EDGE,"E29.right")])]}),"instanceName":"1"}),"instanceName":"1"});
            var Q7;
            Q7=makeQuery(id+"F24.opPattern","COPY",BODY,{"derivedFrom":makeQuery(id+"F20.opExtrude","SWEPT_BODY",BODY,{"disambiguationData":[OSD([sQuery(id+"F19.wireOp",EDGE,"E29.bottom"),sQuery(id+"F19.wireOp",EDGE,"E29.top"),sQuery(id+"F19.wireOp",EDGE,"E29.left"),sQuery(id+"F19.wireOp",EDGE,"E29.right")])]}),"instanceName":"1"});
            transform(context, id + "F25", {"entities" : qUnion([Q0, Q1, Q2, Q3, Q4, Q5, Q6, Q7]), "transformType" : TransformType.TRANSLATION_3D, "dx" : 0 * mm, "dy" : 0 * mm, "dz" : -430 * mm, "makeCopy" : true});
        }
        {
            var Q0;
            Q0=makeQuery(id+"F25.opPattern","COPY",BODY,{"derivedFrom":makeQuery(id+"F21.opPattern","COPY",BODY,{"derivedFrom":makeQuery(id+"F20.opExtrude","SWEPT_BODY",BODY,{"disambiguationData":[OSD([sQuery(id+"F19.wireOp",EDGE,"E29.bottom"),sQuery(id+"F19.wireOp",EDGE,"E29.top"),sQuery(id+"F19.wireOp",EDGE,"E29.left"),sQuery(id+"F19.wireOp",EDGE,"E29.right")])]}),"instanceName":"1"}),"instanceName":"1"});
            var Q1;
            Q1=makeQuery(id+"F25.opPattern","COPY",BODY,{"derivedFrom":makeQuery(id+"F24.opPattern","COPY",BODY,{"derivedFrom":makeQuery(id+"F21.opPattern","COPY",BODY,{"derivedFrom":makeQuery(id+"F20.opExtrude","SWEPT_BODY",BODY,{"disambiguationData":[OSD([sQuery(id+"F19.wireOp",EDGE,"E29.bottom"),sQuery(id+"F19.wireOp",EDGE,"E29.top"),sQuery(id+"F19.wireOp",EDGE,"E29.left"),sQuery(id+"F19.wireOp",EDGE,"E29.right")])]}),"instanceName":"1"}),"instanceName":"1"}),"instanceName":"1"});
            var Q2;
            Q2=makeQuery(id+"F25.opPattern","COPY",BODY,{"derivedFrom":makeQuery(id+"F23.opPattern","COPY",BODY,{"derivedFrom":makeQuery(id+"F21.opPattern","COPY",BODY,{"derivedFrom":makeQuery(id+"F20.opExtrude","SWEPT_BODY",BODY,{"disambiguationData":[OSD([sQuery(id+"F19.wireOp",EDGE,"E29.bottom"),sQuery(id+"F19.wireOp",EDGE,"E29.top"),sQuery(id+"F19.wireOp",EDGE,"E29.left"),sQuery(id+"F19.wireOp",EDGE,"E29.right")])]}),"instanceName":"1"}),"instanceName":"1"}),"instanceName":"1"});
            var Q3;
            Q3=makeQuery(id+"F25.opPattern","COPY",BODY,{"derivedFrom":makeQuery(id+"F24.opPattern","COPY",BODY,{"derivedFrom":makeQuery(id+"F23.opPattern","COPY",BODY,{"derivedFrom":makeQuery(id+"F21.opPattern","COPY",BODY,{"derivedFrom":makeQuery(id+"F20.opExtrude","SWEPT_BODY",BODY,{"disambiguationData":[OSD([sQuery(id+"F19.wireOp",EDGE,"E29.bottom"),sQuery(id+"F19.wireOp",EDGE,"E29.top"),sQuery(id+"F19.wireOp",EDGE,"E29.left"),sQuery(id+"F19.wireOp",EDGE,"E29.right")])]}),"instanceName":"1"}),"instanceName":"1"}),"instanceName":"1"}),"instanceName":"1"});
            var Q4;
            Q4=makeQuery(id+"F25.opPattern","COPY",BODY,{"derivedFrom":makeQuery(id+"F22.opPattern","COPY",BODY,{"derivedFrom":makeQuery(id+"F20.opExtrude","SWEPT_BODY",BODY,{"disambiguationData":[OSD([sQuery(id+"F19.wireOp",EDGE,"E29.bottom"),sQuery(id+"F19.wireOp",EDGE,"E29.top"),sQuery(id+"F19.wireOp",EDGE,"E29.left"),sQuery(id+"F19.wireOp",EDGE,"E29.right")])]}),"instanceName":"1"}),"instanceName":"1"});
            var Q5;
            Q5=makeQuery(id+"F25.opPattern","COPY",BODY,{"derivedFrom":makeQuery(id+"F24.opPattern","COPY",BODY,{"derivedFrom":makeQuery(id+"F22.opPattern","COPY",BODY,{"derivedFrom":makeQuery(id+"F20.opExtrude","SWEPT_BODY",BODY,{"disambiguationData":[OSD([sQuery(id+"F19.wireOp",EDGE,"E29.bottom"),sQuery(id+"F19.wireOp",EDGE,"E29.top"),sQuery(id+"F19.wireOp",EDGE,"E29.left"),sQuery(id+"F19.wireOp",EDGE,"E29.right")])]}),"instanceName":"1"}),"instanceName":"1"}),"instanceName":"1"});
            var Q6;
            Q6=makeQuery(id+"F25.opPattern","COPY",BODY,{"derivedFrom":makeQuery(id+"F20.opExtrude","SWEPT_BODY",BODY,{"disambiguationData":[OSD([sQuery(id+"F19.wireOp",EDGE,"E29.bottom"),sQuery(id+"F19.wireOp",EDGE,"E29.top"),sQuery(id+"F19.wireOp",EDGE,"E29.left"),sQuery(id+"F19.wireOp",EDGE,"E29.right")])]}),"instanceName":"1"});
            var Q7;
            Q7=makeQuery(id+"F25.opPattern","COPY",BODY,{"derivedFrom":makeQuery(id+"F24.opPattern","COPY",BODY,{"derivedFrom":makeQuery(id+"F20.opExtrude","SWEPT_BODY",BODY,{"disambiguationData":[OSD([sQuery(id+"F19.wireOp",EDGE,"E29.bottom"),sQuery(id+"F19.wireOp",EDGE,"E29.top"),sQuery(id+"F19.wireOp",EDGE,"E29.left"),sQuery(id+"F19.wireOp",EDGE,"E29.right")])]}),"instanceName":"1"}),"instanceName":"1"});
            transform(context, id + "F26", {"entities" : qUnion([Q0, Q1, Q2, Q3, Q4, Q5, Q6, Q7]), "transformType" : TransformType.TRANSLATION_3D, "dx" : 0 * mm, "dy" : 0 * mm, "dz" : -295 * mm, "makeCopy" : true});
        }
        {
            var Q0;
            Q0=makeQuery(id+"F26.opPattern","COPY",BODY,{"derivedFrom":makeQuery(id+"F25.opPattern","COPY",BODY,{"derivedFrom":makeQuery(id+"F21.opPattern","COPY",BODY,{"derivedFrom":makeQuery(id+"F20.opExtrude","SWEPT_BODY",BODY,{"disambiguationData":[OSD([sQuery(id+"F19.wireOp",EDGE,"E29.bottom"),sQuery(id+"F19.wireOp",EDGE,"E29.top"),sQuery(id+"F19.wireOp",EDGE,"E29.left"),sQuery(id+"F19.wireOp",EDGE,"E29.right")])]}),"instanceName":"1"}),"instanceName":"1"}),"instanceName":"1"});
            var Q1;
            Q1=makeQuery(id+"F26.opPattern","COPY",BODY,{"derivedFrom":makeQuery(id+"F25.opPattern","COPY",BODY,{"derivedFrom":makeQuery(id+"F24.opPattern","COPY",BODY,{"derivedFrom":makeQuery(id+"F21.opPattern","COPY",BODY,{"derivedFrom":makeQuery(id+"F20.opExtrude","SWEPT_BODY",BODY,{"disambiguationData":[OSD([sQuery(id+"F19.wireOp",EDGE,"E29.bottom"),sQuery(id+"F19.wireOp",EDGE,"E29.top"),sQuery(id+"F19.wireOp",EDGE,"E29.left"),sQuery(id+"F19.wireOp",EDGE,"E29.right")])]}),"instanceName":"1"}),"instanceName":"1"}),"instanceName":"1"}),"instanceName":"1"});
            var Q2;
            Q2=makeQuery(id+"F26.opPattern","COPY",BODY,{"derivedFrom":makeQuery(id+"F25.opPattern","COPY",BODY,{"derivedFrom":makeQuery(id+"F23.opPattern","COPY",BODY,{"derivedFrom":makeQuery(id+"F21.opPattern","COPY",BODY,{"derivedFrom":makeQuery(id+"F20.opExtrude","SWEPT_BODY",BODY,{"disambiguationData":[OSD([sQuery(id+"F19.wireOp",EDGE,"E29.bottom"),sQuery(id+"F19.wireOp",EDGE,"E29.top"),sQuery(id+"F19.wireOp",EDGE,"E29.left"),sQuery(id+"F19.wireOp",EDGE,"E29.right")])]}),"instanceName":"1"}),"instanceName":"1"}),"instanceName":"1"}),"instanceName":"1"});
            var Q3;
            Q3=makeQuery(id+"F26.opPattern","COPY",BODY,{"derivedFrom":makeQuery(id+"F25.opPattern","COPY",BODY,{"derivedFrom":makeQuery(id+"F24.opPattern","COPY",BODY,{"derivedFrom":makeQuery(id+"F23.opPattern","COPY",BODY,{"derivedFrom":makeQuery(id+"F21.opPattern","COPY",BODY,{"derivedFrom":makeQuery(id+"F20.opExtrude","SWEPT_BODY",BODY,{"disambiguationData":[OSD([sQuery(id+"F19.wireOp",EDGE,"E29.bottom"),sQuery(id+"F19.wireOp",EDGE,"E29.top"),sQuery(id+"F19.wireOp",EDGE,"E29.left"),sQuery(id+"F19.wireOp",EDGE,"E29.right")])]}),"instanceName":"1"}),"instanceName":"1"}),"instanceName":"1"}),"instanceName":"1"}),"instanceName":"1"});
            var Q4;
            Q4=makeQuery(id+"F26.opPattern","COPY",BODY,{"derivedFrom":makeQuery(id+"F25.opPattern","COPY",BODY,{"derivedFrom":makeQuery(id+"F22.opPattern","COPY",BODY,{"derivedFrom":makeQuery(id+"F20.opExtrude","SWEPT_BODY",BODY,{"disambiguationData":[OSD([sQuery(id+"F19.wireOp",EDGE,"E29.bottom"),sQuery(id+"F19.wireOp",EDGE,"E29.top"),sQuery(id+"F19.wireOp",EDGE,"E29.left"),sQuery(id+"F19.wireOp",EDGE,"E29.right")])]}),"instanceName":"1"}),"instanceName":"1"}),"instanceName":"1"});
            var Q5;
            Q5=makeQuery(id+"F26.opPattern","COPY",BODY,{"derivedFrom":makeQuery(id+"F25.opPattern","COPY",BODY,{"derivedFrom":makeQuery(id+"F24.opPattern","COPY",BODY,{"derivedFrom":makeQuery(id+"F22.opPattern","COPY",BODY,{"derivedFrom":makeQuery(id+"F20.opExtrude","SWEPT_BODY",BODY,{"disambiguationData":[OSD([sQuery(id+"F19.wireOp",EDGE,"E29.bottom"),sQuery(id+"F19.wireOp",EDGE,"E29.top"),sQuery(id+"F19.wireOp",EDGE,"E29.left"),sQuery(id+"F19.wireOp",EDGE,"E29.right")])]}),"instanceName":"1"}),"instanceName":"1"}),"instanceName":"1"}),"instanceName":"1"});
            var Q6;
            Q6=makeQuery(id+"F26.opPattern","COPY",BODY,{"derivedFrom":makeQuery(id+"F25.opPattern","COPY",BODY,{"derivedFrom":makeQuery(id+"F20.opExtrude","SWEPT_BODY",BODY,{"disambiguationData":[OSD([sQuery(id+"F19.wireOp",EDGE,"E29.bottom"),sQuery(id+"F19.wireOp",EDGE,"E29.top"),sQuery(id+"F19.wireOp",EDGE,"E29.left"),sQuery(id+"F19.wireOp",EDGE,"E29.right")])]}),"instanceName":"1"}),"instanceName":"1"});
            var Q7;
            Q7=makeQuery(id+"F26.opPattern","COPY",BODY,{"derivedFrom":makeQuery(id+"F25.opPattern","COPY",BODY,{"derivedFrom":makeQuery(id+"F24.opPattern","COPY",BODY,{"derivedFrom":makeQuery(id+"F20.opExtrude","SWEPT_BODY",BODY,{"disambiguationData":[OSD([sQuery(id+"F19.wireOp",EDGE,"E29.bottom"),sQuery(id+"F19.wireOp",EDGE,"E29.top"),sQuery(id+"F19.wireOp",EDGE,"E29.left"),sQuery(id+"F19.wireOp",EDGE,"E29.right")])]}),"instanceName":"1"}),"instanceName":"1"}),"instanceName":"1"});
            transform(context, id + "F27", {"entities" : qUnion([Q0, Q1, Q2, Q3, Q4, Q5, Q6, Q7]), "transformType" : TransformType.TRANSLATION_3D, "dx" : 0 * mm, "dy" : 0 * mm, "dz" : -295 * mm, "makeCopy" : true});
        }
        {
            var Q0;
            Q0=makeQuery(id+"F27.opPattern","COPY",BODY,{"derivedFrom":makeQuery(id+"F26.opPattern","COPY",BODY,{"derivedFrom":makeQuery(id+"F25.opPattern","COPY",BODY,{"derivedFrom":makeQuery(id+"F21.opPattern","COPY",BODY,{"derivedFrom":makeQuery(id+"F20.opExtrude","SWEPT_BODY",BODY,{"disambiguationData":[OSD([sQuery(id+"F19.wireOp",EDGE,"E29.bottom"),sQuery(id+"F19.wireOp",EDGE,"E29.top"),sQuery(id+"F19.wireOp",EDGE,"E29.left"),sQuery(id+"F19.wireOp",EDGE,"E29.right")])]}),"instanceName":"1"}),"instanceName":"1"}),"instanceName":"1"}),"instanceName":"1"});
            var Q1;
            Q1=makeQuery(id+"F27.opPattern","COPY",BODY,{"derivedFrom":makeQuery(id+"F26.opPattern","COPY",BODY,{"derivedFrom":makeQuery(id+"F25.opPattern","COPY",BODY,{"derivedFrom":makeQuery(id+"F24.opPattern","COPY",BODY,{"derivedFrom":makeQuery(id+"F21.opPattern","COPY",BODY,{"derivedFrom":makeQuery(id+"F20.opExtrude","SWEPT_BODY",BODY,{"disambiguationData":[OSD([sQuery(id+"F19.wireOp",EDGE,"E29.bottom"),sQuery(id+"F19.wireOp",EDGE,"E29.top"),sQuery(id+"F19.wireOp",EDGE,"E29.left"),sQuery(id+"F19.wireOp",EDGE,"E29.right")])]}),"instanceName":"1"}),"instanceName":"1"}),"instanceName":"1"}),"instanceName":"1"}),"instanceName":"1"});
            var Q2;
            Q2=makeQuery(id+"F27.opPattern","COPY",BODY,{"derivedFrom":makeQuery(id+"F26.opPattern","COPY",BODY,{"derivedFrom":makeQuery(id+"F25.opPattern","COPY",BODY,{"derivedFrom":makeQuery(id+"F23.opPattern","COPY",BODY,{"derivedFrom":makeQuery(id+"F21.opPattern","COPY",BODY,{"derivedFrom":makeQuery(id+"F20.opExtrude","SWEPT_BODY",BODY,{"disambiguationData":[OSD([sQuery(id+"F19.wireOp",EDGE,"E29.bottom"),sQuery(id+"F19.wireOp",EDGE,"E29.top"),sQuery(id+"F19.wireOp",EDGE,"E29.left"),sQuery(id+"F19.wireOp",EDGE,"E29.right")])]}),"instanceName":"1"}),"instanceName":"1"}),"instanceName":"1"}),"instanceName":"1"}),"instanceName":"1"});
            var Q3;
            Q3=makeQuery(id+"F27.opPattern","COPY",BODY,{"derivedFrom":makeQuery(id+"F26.opPattern","COPY",BODY,{"derivedFrom":makeQuery(id+"F25.opPattern","COPY",BODY,{"derivedFrom":makeQuery(id+"F24.opPattern","COPY",BODY,{"derivedFrom":makeQuery(id+"F23.opPattern","COPY",BODY,{"derivedFrom":makeQuery(id+"F21.opPattern","COPY",BODY,{"derivedFrom":makeQuery(id+"F20.opExtrude","SWEPT_BODY",BODY,{"disambiguationData":[OSD([sQuery(id+"F19.wireOp",EDGE,"E29.bottom"),sQuery(id+"F19.wireOp",EDGE,"E29.top"),sQuery(id+"F19.wireOp",EDGE,"E29.left"),sQuery(id+"F19.wireOp",EDGE,"E29.right")])]}),"instanceName":"1"}),"instanceName":"1"}),"instanceName":"1"}),"instanceName":"1"}),"instanceName":"1"}),"instanceName":"1"});
            var Q4;
            Q4=makeQuery(id+"F27.opPattern","COPY",BODY,{"derivedFrom":makeQuery(id+"F26.opPattern","COPY",BODY,{"derivedFrom":makeQuery(id+"F25.opPattern","COPY",BODY,{"derivedFrom":makeQuery(id+"F22.opPattern","COPY",BODY,{"derivedFrom":makeQuery(id+"F20.opExtrude","SWEPT_BODY",BODY,{"disambiguationData":[OSD([sQuery(id+"F19.wireOp",EDGE,"E29.bottom"),sQuery(id+"F19.wireOp",EDGE,"E29.top"),sQuery(id+"F19.wireOp",EDGE,"E29.left"),sQuery(id+"F19.wireOp",EDGE,"E29.right")])]}),"instanceName":"1"}),"instanceName":"1"}),"instanceName":"1"}),"instanceName":"1"});
            var Q5;
            Q5=makeQuery(id+"F27.opPattern","COPY",BODY,{"derivedFrom":makeQuery(id+"F26.opPattern","COPY",BODY,{"derivedFrom":makeQuery(id+"F25.opPattern","COPY",BODY,{"derivedFrom":makeQuery(id+"F24.opPattern","COPY",BODY,{"derivedFrom":makeQuery(id+"F22.opPattern","COPY",BODY,{"derivedFrom":makeQuery(id+"F20.opExtrude","SWEPT_BODY",BODY,{"disambiguationData":[OSD([sQuery(id+"F19.wireOp",EDGE,"E29.bottom"),sQuery(id+"F19.wireOp",EDGE,"E29.top"),sQuery(id+"F19.wireOp",EDGE,"E29.left"),sQuery(id+"F19.wireOp",EDGE,"E29.right")])]}),"instanceName":"1"}),"instanceName":"1"}),"instanceName":"1"}),"instanceName":"1"}),"instanceName":"1"});
            var Q6;
            Q6=makeQuery(id+"F27.opPattern","COPY",BODY,{"derivedFrom":makeQuery(id+"F26.opPattern","COPY",BODY,{"derivedFrom":makeQuery(id+"F25.opPattern","COPY",BODY,{"derivedFrom":makeQuery(id+"F20.opExtrude","SWEPT_BODY",BODY,{"disambiguationData":[OSD([sQuery(id+"F19.wireOp",EDGE,"E29.bottom"),sQuery(id+"F19.wireOp",EDGE,"E29.top"),sQuery(id+"F19.wireOp",EDGE,"E29.left"),sQuery(id+"F19.wireOp",EDGE,"E29.right")])]}),"instanceName":"1"}),"instanceName":"1"}),"instanceName":"1"});
            var Q7;
            Q7=makeQuery(id+"F27.opPattern","COPY",BODY,{"derivedFrom":makeQuery(id+"F26.opPattern","COPY",BODY,{"derivedFrom":makeQuery(id+"F25.opPattern","COPY",BODY,{"derivedFrom":makeQuery(id+"F24.opPattern","COPY",BODY,{"derivedFrom":makeQuery(id+"F20.opExtrude","SWEPT_BODY",BODY,{"disambiguationData":[OSD([sQuery(id+"F19.wireOp",EDGE,"E29.bottom"),sQuery(id+"F19.wireOp",EDGE,"E29.top"),sQuery(id+"F19.wireOp",EDGE,"E29.left"),sQuery(id+"F19.wireOp",EDGE,"E29.right")])]}),"instanceName":"1"}),"instanceName":"1"}),"instanceName":"1"}),"instanceName":"1"});
            transform(context, id + "F28", {"entities" : qUnion([Q0, Q1, Q2, Q3, Q4, Q5, Q6, Q7]), "transformType" : TransformType.TRANSLATION_3D, "dx" : 0 * mm, "dy" : 0 * mm, "dz" : -340 * mm, "makeCopy" : true});
        }
        {
            var Q0;
            Q0=makeQuery(id+"F28.opPattern","COPY",BODY,{"derivedFrom":makeQuery(id+"F27.opPattern","COPY",BODY,{"derivedFrom":makeQuery(id+"F26.opPattern","COPY",BODY,{"derivedFrom":makeQuery(id+"F25.opPattern","COPY",BODY,{"derivedFrom":makeQuery(id+"F21.opPattern","COPY",BODY,{"derivedFrom":makeQuery(id+"F20.opExtrude","SWEPT_BODY",BODY,{"disambiguationData":[OSD([sQuery(id+"F19.wireOp",EDGE,"E29.bottom"),sQuery(id+"F19.wireOp",EDGE,"E29.top"),sQuery(id+"F19.wireOp",EDGE,"E29.left"),sQuery(id+"F19.wireOp",EDGE,"E29.right")])]}),"instanceName":"1"}),"instanceName":"1"}),"instanceName":"1"}),"instanceName":"1"}),"instanceName":"1"});
            var Q1;
            Q1=makeQuery(id+"F28.opPattern","COPY",BODY,{"derivedFrom":makeQuery(id+"F27.opPattern","COPY",BODY,{"derivedFrom":makeQuery(id+"F26.opPattern","COPY",BODY,{"derivedFrom":makeQuery(id+"F25.opPattern","COPY",BODY,{"derivedFrom":makeQuery(id+"F24.opPattern","COPY",BODY,{"derivedFrom":makeQuery(id+"F21.opPattern","COPY",BODY,{"derivedFrom":makeQuery(id+"F20.opExtrude","SWEPT_BODY",BODY,{"disambiguationData":[OSD([sQuery(id+"F19.wireOp",EDGE,"E29.bottom"),sQuery(id+"F19.wireOp",EDGE,"E29.top"),sQuery(id+"F19.wireOp",EDGE,"E29.left"),sQuery(id+"F19.wireOp",EDGE,"E29.right")])]}),"instanceName":"1"}),"instanceName":"1"}),"instanceName":"1"}),"instanceName":"1"}),"instanceName":"1"}),"instanceName":"1"});
            var Q2;
            Q2=makeQuery(id+"F28.opPattern","COPY",BODY,{"derivedFrom":makeQuery(id+"F27.opPattern","COPY",BODY,{"derivedFrom":makeQuery(id+"F26.opPattern","COPY",BODY,{"derivedFrom":makeQuery(id+"F25.opPattern","COPY",BODY,{"derivedFrom":makeQuery(id+"F23.opPattern","COPY",BODY,{"derivedFrom":makeQuery(id+"F21.opPattern","COPY",BODY,{"derivedFrom":makeQuery(id+"F20.opExtrude","SWEPT_BODY",BODY,{"disambiguationData":[OSD([sQuery(id+"F19.wireOp",EDGE,"E29.bottom"),sQuery(id+"F19.wireOp",EDGE,"E29.top"),sQuery(id+"F19.wireOp",EDGE,"E29.left"),sQuery(id+"F19.wireOp",EDGE,"E29.right")])]}),"instanceName":"1"}),"instanceName":"1"}),"instanceName":"1"}),"instanceName":"1"}),"instanceName":"1"}),"instanceName":"1"});
            var Q3;
            Q3=makeQuery(id+"F28.opPattern","COPY",BODY,{"derivedFrom":makeQuery(id+"F27.opPattern","COPY",BODY,{"derivedFrom":makeQuery(id+"F26.opPattern","COPY",BODY,{"derivedFrom":makeQuery(id+"F25.opPattern","COPY",BODY,{"derivedFrom":makeQuery(id+"F24.opPattern","COPY",BODY,{"derivedFrom":makeQuery(id+"F23.opPattern","COPY",BODY,{"derivedFrom":makeQuery(id+"F21.opPattern","COPY",BODY,{"derivedFrom":makeQuery(id+"F20.opExtrude","SWEPT_BODY",BODY,{"disambiguationData":[OSD([sQuery(id+"F19.wireOp",EDGE,"E29.bottom"),sQuery(id+"F19.wireOp",EDGE,"E29.top"),sQuery(id+"F19.wireOp",EDGE,"E29.left"),sQuery(id+"F19.wireOp",EDGE,"E29.right")])]}),"instanceName":"1"}),"instanceName":"1"}),"instanceName":"1"}),"instanceName":"1"}),"instanceName":"1"}),"instanceName":"1"}),"instanceName":"1"});
            var Q4;
            Q4=makeQuery(id+"F28.opPattern","COPY",BODY,{"derivedFrom":makeQuery(id+"F27.opPattern","COPY",BODY,{"derivedFrom":makeQuery(id+"F26.opPattern","COPY",BODY,{"derivedFrom":makeQuery(id+"F25.opPattern","COPY",BODY,{"derivedFrom":makeQuery(id+"F22.opPattern","COPY",BODY,{"derivedFrom":makeQuery(id+"F20.opExtrude","SWEPT_BODY",BODY,{"disambiguationData":[OSD([sQuery(id+"F19.wireOp",EDGE,"E29.bottom"),sQuery(id+"F19.wireOp",EDGE,"E29.top"),sQuery(id+"F19.wireOp",EDGE,"E29.left"),sQuery(id+"F19.wireOp",EDGE,"E29.right")])]}),"instanceName":"1"}),"instanceName":"1"}),"instanceName":"1"}),"instanceName":"1"}),"instanceName":"1"});
            var Q5;
            Q5=makeQuery(id+"F28.opPattern","COPY",BODY,{"derivedFrom":makeQuery(id+"F27.opPattern","COPY",BODY,{"derivedFrom":makeQuery(id+"F26.opPattern","COPY",BODY,{"derivedFrom":makeQuery(id+"F25.opPattern","COPY",BODY,{"derivedFrom":makeQuery(id+"F24.opPattern","COPY",BODY,{"derivedFrom":makeQuery(id+"F22.opPattern","COPY",BODY,{"derivedFrom":makeQuery(id+"F20.opExtrude","SWEPT_BODY",BODY,{"disambiguationData":[OSD([sQuery(id+"F19.wireOp",EDGE,"E29.bottom"),sQuery(id+"F19.wireOp",EDGE,"E29.top"),sQuery(id+"F19.wireOp",EDGE,"E29.left"),sQuery(id+"F19.wireOp",EDGE,"E29.right")])]}),"instanceName":"1"}),"instanceName":"1"}),"instanceName":"1"}),"instanceName":"1"}),"instanceName":"1"}),"instanceName":"1"});
            var Q6;
            Q6=makeQuery(id+"F28.opPattern","COPY",BODY,{"derivedFrom":makeQuery(id+"F27.opPattern","COPY",BODY,{"derivedFrom":makeQuery(id+"F26.opPattern","COPY",BODY,{"derivedFrom":makeQuery(id+"F25.opPattern","COPY",BODY,{"derivedFrom":makeQuery(id+"F20.opExtrude","SWEPT_BODY",BODY,{"disambiguationData":[OSD([sQuery(id+"F19.wireOp",EDGE,"E29.bottom"),sQuery(id+"F19.wireOp",EDGE,"E29.top"),sQuery(id+"F19.wireOp",EDGE,"E29.left"),sQuery(id+"F19.wireOp",EDGE,"E29.right")])]}),"instanceName":"1"}),"instanceName":"1"}),"instanceName":"1"}),"instanceName":"1"});
            var Q7;
            Q7=makeQuery(id+"F28.opPattern","COPY",BODY,{"derivedFrom":makeQuery(id+"F27.opPattern","COPY",BODY,{"derivedFrom":makeQuery(id+"F26.opPattern","COPY",BODY,{"derivedFrom":makeQuery(id+"F25.opPattern","COPY",BODY,{"derivedFrom":makeQuery(id+"F24.opPattern","COPY",BODY,{"derivedFrom":makeQuery(id+"F20.opExtrude","SWEPT_BODY",BODY,{"disambiguationData":[OSD([sQuery(id+"F19.wireOp",EDGE,"E29.bottom"),sQuery(id+"F19.wireOp",EDGE,"E29.top"),sQuery(id+"F19.wireOp",EDGE,"E29.left"),sQuery(id+"F19.wireOp",EDGE,"E29.right")])]}),"instanceName":"1"}),"instanceName":"1"}),"instanceName":"1"}),"instanceName":"1"}),"instanceName":"1"});
            transform(context, id + "F29", {"entities" : qUnion([Q0, Q1, Q2, Q3, Q4, Q5, Q6, Q7]), "transformType" : TransformType.TRANSLATION_3D, "dx" : 0 * mm, "dy" : 0 * mm, "dz" : -515 * mm, "makeCopy" : true});
        }
        {
            var Q0;
            Q0=makeQuery(id+"F17.opPattern","COPY",FACE,{"derivedFrom":makeQuery(id+"F16.opPattern","COPY",FACE,{"derivedFrom":makeQuery(id+"F15.opPattern","COPY",FACE,{"derivedFrom":makeQuery(id+"F14.opPattern","COPY",FACE,{"derivedFrom":makeQuery(id+"F11.opPattern","COPY",FACE,{"derivedFrom":makeQuery(id+"F10.opExtrude","SWEPT_FACE",FACE,{"disambiguationData":[OSD([sQuery(id+"F9.wireOp",EDGE,"E25")])]}),"instanceName":"1"}),"instanceName":"1"}),"instanceName":"1"}),"instanceName":"1"}),"instanceName":"1"});
            var sketch = newSketch(context, id + "F30", { "sketchPlane" : qUnion([Q0])});
            skLineSegment(sketch, "E30.bottom", {"start": v(-12.5, 854.5) * mm, "end": v(-9.5, 854.5) * mm});
            skLineSegment(sketch, "E30.top", {"start": v(-12.5, 829.5) * mm, "end": v(-9.5, 829.5) * mm});
            skLineSegment(sketch, "E30.left", {"start": v(-12.5, 854.5) * mm, "end": v(-12.5, 829.5) * mm});
            skLineSegment(sketch, "E30.right", {"start": v(-9.5, 854.5) * mm, "end": v(-9.5, 829.5) * mm});
            skSolve(sketch);
        }
        {
            var Q0;
            {var subQ0=sQuery(id+"F30.wireOp",EDGE,"E30.left");Q0=makeQuery(id+"F30.imprint","IMPRINT",FACE,{"disambiguationData":[TD([[makeQuery(id+"F30.imprint","IMPRINT",EDGE,{"derivedFrom":subQ0}),1.0]])]});}
            var Q1;
            {var subQ0=sQuery(id+"F30.wireOp",EDGE,"E30.right");Q1=makeQuery(id+"F30.imprint","IMPRINT",FACE,{"disambiguationData":[TD([[makeQuery(id+"F30.imprint","IMPRINT",EDGE,{"derivedFrom":subQ0}),-1.0]])]});}
            extrude(context, id + "F31", {"entities" : qUnion([Q0, Q1]), "depth" : 405 * mm});
        }
        {
            var Q0;
            Q0=makeQuery(id+"F16.opPattern","COPY",FACE,{"derivedFrom":makeQuery(id+"F15.opPattern","COPY",FACE,{"derivedFrom":makeQuery(id+"F14.opPattern","COPY",FACE,{"derivedFrom":makeQuery(id+"F11.opPattern","COPY",FACE,{"derivedFrom":makeQuery(id+"F10.opExtrude","SWEPT_FACE",FACE,{"disambiguationData":[OSD([sQuery(id+"F9.wireOp",EDGE,"E25")])]}),"instanceName":"1"}),"instanceName":"1"}),"instanceName":"1"}),"instanceName":"1"});
            var sketch = newSketch(context, id + "F32", { "sketchPlane" : qUnion([Q0])});
            skLineSegment(sketch, "E31.bottom", {"start": v(-12.5, 520.5) * mm, "end": v(-9.5, 520.5) * mm});
            skLineSegment(sketch, "E31.top", {"start": v(-12.5, 495.5) * mm, "end": v(-9.5, 495.5) * mm});
            skLineSegment(sketch, "E31.left", {"start": v(-12.5, 520.5) * mm, "end": v(-12.5, 495.5) * mm});
            skLineSegment(sketch, "E31.right", {"start": v(-9.5, 520.5) * mm, "end": v(-9.5, 495.5) * mm});
            skSolve(sketch);
        }
        {
            var Q0;
            {var subQ0=sQuery(id+"F32.wireOp",EDGE,"E31.right");Q0=makeQuery(id+"F32.imprint","IMPRINT",FACE,{"disambiguationData":[TD([[makeQuery(id+"F32.imprint","IMPRINT",EDGE,{"derivedFrom":subQ0}),-1.0]])]});}
            var Q1;
            {var subQ0=sQuery(id+"F32.wireOp",EDGE,"E31.left");Q1=makeQuery(id+"F32.imprint","IMPRINT",FACE,{"disambiguationData":[TD([[makeQuery(id+"F32.imprint","IMPRINT",EDGE,{"derivedFrom":subQ0}),1.0]])]});}
            extrude(context, id + "F33", {"entities" : qUnion([Q0, Q1]), "depth" : 270 * mm});
        }
        {
            var Q0;
            Q0=makeQuery(id+"F15.opPattern","COPY",FACE,{"derivedFrom":makeQuery(id+"F14.opPattern","COPY",FACE,{"derivedFrom":makeQuery(id+"F11.opPattern","COPY",FACE,{"derivedFrom":makeQuery(id+"F10.opExtrude","SWEPT_FACE",FACE,{"disambiguationData":[OSD([sQuery(id+"F9.wireOp",EDGE,"E25")])]}),"instanceName":"1"}),"instanceName":"1"}),"instanceName":"1"});
            var sketch = newSketch(context, id + "F34", { "sketchPlane" : qUnion([Q0])});
            skLineSegment(sketch, "E32.bottom", {"start": v(-12.5, 697.5) * mm, "end": v(-9.5, 697.5) * mm});
            skLineSegment(sketch, "E32.top", {"start": v(-12.5, 672.5) * mm, "end": v(-9.5, 672.5) * mm});
            skLineSegment(sketch, "E32.left", {"start": v(-12.5, 697.5) * mm, "end": v(-12.5, 672.5) * mm});
            skLineSegment(sketch, "E32.right", {"start": v(-9.5, 697.5) * mm, "end": v(-9.5, 672.5) * mm});
            skSolve(sketch);
        }
        {
            var Q0;
            {var subQ0=sQuery(id+"F34.wireOp",EDGE,"E32.right");Q0=makeQuery(id+"F34.imprint","IMPRINT",FACE,{"disambiguationData":[TD([[makeQuery(id+"F34.imprint","IMPRINT",EDGE,{"derivedFrom":subQ0}),-1.0]])]});}
            var Q1;
            {var subQ0=sQuery(id+"F34.wireOp",EDGE,"E32.left");Q1=makeQuery(id+"F34.imprint","IMPRINT",FACE,{"disambiguationData":[TD([[makeQuery(id+"F34.imprint","IMPRINT",EDGE,{"derivedFrom":subQ0}),1.0]])]});}
            extrude(context, id + "F35", {"entities" : qUnion([Q0, Q1]), "depth" : 270 * mm});
        }
        {
            var Q0;
            Q0=makeQuery(id+"F11.opPattern","COPY",FACE,{"derivedFrom":makeQuery(id+"F10.opExtrude","SWEPT_FACE",FACE,{"disambiguationData":[OSD([sQuery(id+"F9.wireOp",EDGE,"E25")])]}),"instanceName":"1"});
            var sketch = newSketch(context, id + "F36", { "sketchPlane" : qUnion([Q0])});
            skLineSegment(sketch, "E33.bottom", {"start": v(-12.5, 727.5) * mm, "end": v(-9.5, 727.5) * mm});
            skLineSegment(sketch, "E33.top", {"start": v(-12.5, 702.5) * mm, "end": v(-9.5, 702.5) * mm});
            skLineSegment(sketch, "E33.left", {"start": v(-12.5, 727.5) * mm, "end": v(-12.5, 702.5) * mm});
            skLineSegment(sketch, "E33.right", {"start": v(-9.5, 727.5) * mm, "end": v(-9.5, 702.5) * mm});
            skSolve(sketch);
        }
        {
            var Q0;
            {var subQ0=sQuery(id+"F36.wireOp",EDGE,"E33.right");Q0=makeQuery(id+"F36.imprint","IMPRINT",FACE,{"disambiguationData":[TD([[makeQuery(id+"F36.imprint","IMPRINT",EDGE,{"derivedFrom":subQ0}),-1.0]])]});}
            var Q1;
            {var subQ0=sQuery(id+"F36.wireOp",EDGE,"E33.left");Q1=makeQuery(id+"F36.imprint","IMPRINT",FACE,{"disambiguationData":[TD([[makeQuery(id+"F36.imprint","IMPRINT",EDGE,{"derivedFrom":subQ0}),1.0]])]});}
            extrude(context, id + "F37", {"entities" : qUnion([Q0, Q1]), "depth" : 490 * mm});
        }
        {
            var Q0;
            Q0=makeQuery(id+"F37.opExtrude","SWEPT_BODY",BODY,{"disambiguationData":[OSD([sQuery(id+"F36.wireOp",EDGE,"E33.bottom"),sQuery(id+"F36.wireOp",EDGE,"E33.top"),sQuery(id+"F36.wireOp",EDGE,"E33.left"),sQuery(id+"F36.wireOp",EDGE,"E33.right")])]});
            transform(context, id + "F38", {"entities" : qUnion([Q0]), "transformType" : TransformType.TRANSLATION_3D, "dx" : 0 * mm, "dy" : -361 * mm, "dz" : 0 * mm, "makeCopy" : true});
        }
        {
            var Q0;
            Q0=makeQuery(id+"F31.opExtrude","SWEPT_BODY",BODY,{"disambiguationData":[OSD([sQuery(id+"F30.wireOp",EDGE,"E30.bottom"),sQuery(id+"F30.wireOp",EDGE,"E30.top"),sQuery(id+"F30.wireOp",EDGE,"E30.left"),sQuery(id+"F30.wireOp",EDGE,"E30.right")])]});
            var Q1;
            Q1=makeQuery(id+"F33.opExtrude","SWEPT_BODY",BODY,{"disambiguationData":[OSD([sQuery(id+"F32.wireOp",EDGE,"E31.bottom"),sQuery(id+"F32.wireOp",EDGE,"E31.top"),sQuery(id+"F32.wireOp",EDGE,"E31.left"),sQuery(id+"F32.wireOp",EDGE,"E31.right")])]});
            var Q2;
            Q2=makeQuery(id+"F35.opExtrude","SWEPT_BODY",BODY,{"disambiguationData":[OSD([sQuery(id+"F34.wireOp",EDGE,"E32.bottom"),sQuery(id+"F34.wireOp",EDGE,"E32.top"),sQuery(id+"F34.wireOp",EDGE,"E32.left"),sQuery(id+"F34.wireOp",EDGE,"E32.right")])]});
            var Q3;
            Q3=makeQuery(id+"F37.opExtrude","SWEPT_BODY",BODY,{"disambiguationData":[OSD([sQuery(id+"F36.wireOp",EDGE,"E33.bottom"),sQuery(id+"F36.wireOp",EDGE,"E33.top"),sQuery(id+"F36.wireOp",EDGE,"E33.left"),sQuery(id+"F36.wireOp",EDGE,"E33.right")])]});
            var Q4;
            Q4=makeQuery(id+"F38.opPattern","COPY",BODY,{"derivedFrom":makeQuery(id+"F37.opExtrude","SWEPT_BODY",BODY,{"disambiguationData":[OSD([sQuery(id+"F36.wireOp",EDGE,"E33.bottom"),sQuery(id+"F36.wireOp",EDGE,"E33.top"),sQuery(id+"F36.wireOp",EDGE,"E33.left"),sQuery(id+"F36.wireOp",EDGE,"E33.right")])]}),"instanceName":"1"});
            transform(context, id + "F39", {"entities" : qUnion([Q0, Q1, Q2, Q3, Q4]), "transformType" : TransformType.TRANSLATION_3D, "dx" : 0 * mm, "dy" : 0 * mm, "dz" : 0 * mm, "makeCopy" : false});
        }
        {
            var Q0;
            Q0=makeQuery(id+"F31.opExtrude","SWEPT_BODY",BODY,{"disambiguationData":[OSD([sQuery(id+"F30.wireOp",EDGE,"E30.bottom"),sQuery(id+"F30.wireOp",EDGE,"E30.top"),sQuery(id+"F30.wireOp",EDGE,"E30.left"),sQuery(id+"F30.wireOp",EDGE,"E30.right")])]});
            var Q1;
            Q1=makeQuery(id+"F33.opExtrude","SWEPT_BODY",BODY,{"disambiguationData":[OSD([sQuery(id+"F32.wireOp",EDGE,"E31.bottom"),sQuery(id+"F32.wireOp",EDGE,"E31.top"),sQuery(id+"F32.wireOp",EDGE,"E31.left"),sQuery(id+"F32.wireOp",EDGE,"E31.right")])]});
            var Q2;
            Q2=makeQuery(id+"F35.opExtrude","SWEPT_BODY",BODY,{"disambiguationData":[OSD([sQuery(id+"F34.wireOp",EDGE,"E32.bottom"),sQuery(id+"F34.wireOp",EDGE,"E32.top"),sQuery(id+"F34.wireOp",EDGE,"E32.left"),sQuery(id+"F34.wireOp",EDGE,"E32.right")])]});
            var Q3;
            Q3=makeQuery(id+"F37.opExtrude","SWEPT_BODY",BODY,{"disambiguationData":[OSD([sQuery(id+"F36.wireOp",EDGE,"E33.bottom"),sQuery(id+"F36.wireOp",EDGE,"E33.top"),sQuery(id+"F36.wireOp",EDGE,"E33.left"),sQuery(id+"F36.wireOp",EDGE,"E33.right")])]});
            var Q4;
            Q4=makeQuery(id+"F38.opPattern","COPY",BODY,{"derivedFrom":makeQuery(id+"F37.opExtrude","SWEPT_BODY",BODY,{"disambiguationData":[OSD([sQuery(id+"F36.wireOp",EDGE,"E33.bottom"),sQuery(id+"F36.wireOp",EDGE,"E33.top"),sQuery(id+"F36.wireOp",EDGE,"E33.left"),sQuery(id+"F36.wireOp",EDGE,"E33.right")])]}),"instanceName":"1"});
            transform(context, id + "F40", {"entities" : qUnion([Q0, Q1, Q2, Q3, Q4]), "transformType" : TransformType.TRANSLATION_3D, "dx" : 437 * mm, "dy" : 0 * mm, "dz" : 0 * mm, "makeCopy" : true});
        }
        {
            var Q0;
            Q0=makeQuery(id+"F21.opPattern","COPY",FACE,{"derivedFrom":makeQuery(id+"F20.opExtrude","SWEPT_FACE",FACE,{"disambiguationData":[OSD([sQuery(id+"F19.wireOp",EDGE,"E29.bottom")])]}),"instanceName":"1"});
            var sketch = newSketch(context, id + "F41", { "sketchPlane" : qUnion([Q0])});
            skLineSegment(sketch, "E34.bottom", {"start": v(-9.5, 1162.5) * mm, "end": v(424.5, 1162.5) * mm});
            skLineSegment(sketch, "E34.top", {"start": v(-9.5, 12.5) * mm, "end": v(424.5, 12.5) * mm});
            skLineSegment(sketch, "E34.left", {"start": v(-9.5, 1162.5) * mm, "end": v(-9.5, 12.5) * mm});
            skLineSegment(sketch, "E34.right", {"start": v(424.5, 1162.5) * mm, "end": v(424.5, 12.5) * mm});
            skSolve(sketch);
        }
        {
            var Q0;
            Q0=makeQuery(id+"F41.imprint","IMPRINT",FACE,{"disambiguationData":[TD([[makeQuery(id+"F41.imprint","IMPRINT",EDGE,{"derivedFrom":sQuery(id+"F41.wireOp",EDGE,"E34.top")}),1.0]])]});
            var Q1;
            {var subQ1=sQuery(id+"F19.wireOp",EDGE,"E29.bottom");Q1=makeQuery(id+"F41.imprint","IMPRINT",FACE,{"disambiguationData":[TD([[makeQuery(id+"F41.imprint","IMPRINT",EDGE,{"derivedFrom":makeQuery(id+"F21.opPattern","COPY",EDGE,{"derivedFrom":makeQuery(id+"F20.opExtrude","CAP_EDGE",EDGE,{"disambiguationData":[OSD([subQ1])],"isStart":true}),"instanceName":"1"})}),-1.0]])]});}
            extrude(context, id + "F42", {"entities" : qUnion([Q0, Q1]), "depth" : 10 * mm});
        }
        {
            var Q0;
            Q0=makeQuery(id+"F42.opExtrude","SWEPT_BODY",BODY,{"disambiguationData":[OSD([sQuery(id+"F41.wireOp",EDGE,"E34.bottom"),sQuery(id+"F41.wireOp",EDGE,"E34.top"),sQuery(id+"F41.wireOp",EDGE,"E34.left"),sQuery(id+"F41.wireOp",EDGE,"E34.right")])]});
            transform(context, id + "F43", {"entities" : qUnion([Q0]), "transformType" : TransformType.TRANSLATION_3D, "dx" : 0 * mm, "dy" : 0 * mm, "dz" : -430 * mm, "makeCopy" : true});
        }
        {
            var Q0;
            Q0=makeQuery(id+"F43.opPattern","COPY",BODY,{"derivedFrom":makeQuery(id+"F42.opExtrude","SWEPT_BODY",BODY,{"disambiguationData":[OSD([sQuery(id+"F41.wireOp",EDGE,"E34.bottom"),sQuery(id+"F41.wireOp",EDGE,"E34.top"),sQuery(id+"F41.wireOp",EDGE,"E34.left"),sQuery(id+"F41.wireOp",EDGE,"E34.right")])]}),"instanceName":"1"});
            transform(context, id + "F44", {"entities" : qUnion([Q0]), "transformType" : TransformType.TRANSLATION_3D, "dx" : 0 * mm, "dy" : 0 * mm, "dz" : -295 * mm, "makeCopy" : true});
        }
        {
            var Q0;
            Q0=makeQuery(id+"F44.opPattern","COPY",BODY,{"derivedFrom":makeQuery(id+"F43.opPattern","COPY",BODY,{"derivedFrom":makeQuery(id+"F42.opExtrude","SWEPT_BODY",BODY,{"disambiguationData":[OSD([sQuery(id+"F41.wireOp",EDGE,"E34.bottom"),sQuery(id+"F41.wireOp",EDGE,"E34.top"),sQuery(id+"F41.wireOp",EDGE,"E34.left"),sQuery(id+"F41.wireOp",EDGE,"E34.right")])]}),"instanceName":"1"}),"instanceName":"1"});
            transform(context, id + "F45", {"entities" : qUnion([Q0]), "transformType" : TransformType.TRANSLATION_3D, "dx" : 0 * mm, "dy" : 0 * mm, "dz" : -295 * mm, "makeCopy" : true});
        }
        {
            var Q0;
            Q0=makeQuery(id+"F45.opPattern","COPY",BODY,{"derivedFrom":makeQuery(id+"F44.opPattern","COPY",BODY,{"derivedFrom":makeQuery(id+"F43.opPattern","COPY",BODY,{"derivedFrom":makeQuery(id+"F42.opExtrude","SWEPT_BODY",BODY,{"disambiguationData":[OSD([sQuery(id+"F41.wireOp",EDGE,"E34.bottom"),sQuery(id+"F41.wireOp",EDGE,"E34.top"),sQuery(id+"F41.wireOp",EDGE,"E34.left"),sQuery(id+"F41.wireOp",EDGE,"E34.right")])]}),"instanceName":"1"}),"instanceName":"1"}),"instanceName":"1"});
            transform(context, id + "F46", {"entities" : qUnion([Q0]), "transformType" : TransformType.TRANSLATION_3D, "dx" : 0 * mm, "dy" : 0 * mm, "dz" : -340 * mm, "makeCopy" : true});
        }
        {
            var Q0;
            Q0=makeQuery(id+"F46.opPattern","COPY",BODY,{"derivedFrom":makeQuery(id+"F45.opPattern","COPY",BODY,{"derivedFrom":makeQuery(id+"F44.opPattern","COPY",BODY,{"derivedFrom":makeQuery(id+"F43.opPattern","COPY",BODY,{"derivedFrom":makeQuery(id+"F42.opExtrude","SWEPT_BODY",BODY,{"disambiguationData":[OSD([sQuery(id+"F41.wireOp",EDGE,"E34.bottom"),sQuery(id+"F41.wireOp",EDGE,"E34.top"),sQuery(id+"F41.wireOp",EDGE,"E34.left"),sQuery(id+"F41.wireOp",EDGE,"E34.right")])]}),"instanceName":"1"}),"instanceName":"1"}),"instanceName":"1"}),"instanceName":"1"});
            transform(context, id + "F47", {"entities" : qUnion([Q0]), "transformType" : TransformType.TRANSLATION_3D, "dx" : 0 * mm, "dy" : 0 * mm, "dz" : -515 * mm, "makeCopy" : true});
        }
        {
            var Q0;
            Q0=makeQuery(id+"F1.opExtrude","SWEPT_BODY",BODY,{"disambiguationData":[OSD([sQuery(id+"F0.wireOp",EDGE,"E0.bottom"),sQuery(id+"F0.wireOp",EDGE,"E0.top"),sQuery(id+"F0.wireOp",EDGE,"E0.left"),sQuery(id+"F0.wireOp",EDGE,"E0.right"),sQuery(id+"F0.wireOp",EDGE,"E1.bottom"),sQuery(id+"F0.wireOp",EDGE,"E1.top"),sQuery(id+"F0.wireOp",EDGE,"E1.left"),sQuery(id+"F0.wireOp",EDGE,"E1.right"),sQuery(id+"F0.wireOp",EDGE,"E2.filletArc"),sQuery(id+"F0.wireOp",EDGE,"E3.filletArc"),sQuery(id+"F0.wireOp",EDGE,"E4.filletArc"),sQuery(id+"F0.wireOp",EDGE,"E5.filletArc"),sQuery(id+"F0.wireOp",EDGE,"E6.filletArc"),sQuery(id+"F0.wireOp",EDGE,"E7.filletArc"),sQuery(id+"F0.wireOp",EDGE,"E8.filletArc"),sQuery(id+"F0.wireOp",EDGE,"E9.filletArc")])]});
            var Q1;
            Q1=makeQuery(id+"F2.opPattern","COPY",BODY,{"derivedFrom":makeQuery(id+"F1.opExtrude","SWEPT_BODY",BODY,{"disambiguationData":[OSD([sQuery(id+"F0.wireOp",EDGE,"E0.bottom"),sQuery(id+"F0.wireOp",EDGE,"E0.top"),sQuery(id+"F0.wireOp",EDGE,"E0.left"),sQuery(id+"F0.wireOp",EDGE,"E0.right"),sQuery(id+"F0.wireOp",EDGE,"E1.bottom"),sQuery(id+"F0.wireOp",EDGE,"E1.top"),sQuery(id+"F0.wireOp",EDGE,"E1.left"),sQuery(id+"F0.wireOp",EDGE,"E1.right"),sQuery(id+"F0.wireOp",EDGE,"E2.filletArc"),sQuery(id+"F0.wireOp",EDGE,"E3.filletArc"),sQuery(id+"F0.wireOp",EDGE,"E4.filletArc"),sQuery(id+"F0.wireOp",EDGE,"E5.filletArc"),sQuery(id+"F0.wireOp",EDGE,"E6.filletArc"),sQuery(id+"F0.wireOp",EDGE,"E7.filletArc"),sQuery(id+"F0.wireOp",EDGE,"E8.filletArc"),sQuery(id+"F0.wireOp",EDGE,"E9.filletArc")])]}),"instanceName":"1"});
            var Q2;
            Q2=makeQuery(id+"F3.opPattern","COPY",BODY,{"derivedFrom":makeQuery(id+"F1.opExtrude","SWEPT_BODY",BODY,{"disambiguationData":[OSD([sQuery(id+"F0.wireOp",EDGE,"E0.bottom"),sQuery(id+"F0.wireOp",EDGE,"E0.top"),sQuery(id+"F0.wireOp",EDGE,"E0.left"),sQuery(id+"F0.wireOp",EDGE,"E0.right"),sQuery(id+"F0.wireOp",EDGE,"E1.bottom"),sQuery(id+"F0.wireOp",EDGE,"E1.top"),sQuery(id+"F0.wireOp",EDGE,"E1.left"),sQuery(id+"F0.wireOp",EDGE,"E1.right"),sQuery(id+"F0.wireOp",EDGE,"E2.filletArc"),sQuery(id+"F0.wireOp",EDGE,"E3.filletArc"),sQuery(id+"F0.wireOp",EDGE,"E4.filletArc"),sQuery(id+"F0.wireOp",EDGE,"E5.filletArc"),sQuery(id+"F0.wireOp",EDGE,"E6.filletArc"),sQuery(id+"F0.wireOp",EDGE,"E7.filletArc"),sQuery(id+"F0.wireOp",EDGE,"E8.filletArc"),sQuery(id+"F0.wireOp",EDGE,"E9.filletArc")])]}),"instanceName":"1"});
            var Q3;
            Q3=makeQuery(id+"F3.opPattern","COPY",BODY,{"derivedFrom":makeQuery(id+"F2.opPattern","COPY",BODY,{"derivedFrom":makeQuery(id+"F1.opExtrude","SWEPT_BODY",BODY,{"disambiguationData":[OSD([sQuery(id+"F0.wireOp",EDGE,"E0.bottom"),sQuery(id+"F0.wireOp",EDGE,"E0.top"),sQuery(id+"F0.wireOp",EDGE,"E0.left"),sQuery(id+"F0.wireOp",EDGE,"E0.right"),sQuery(id+"F0.wireOp",EDGE,"E1.bottom"),sQuery(id+"F0.wireOp",EDGE,"E1.top"),sQuery(id+"F0.wireOp",EDGE,"E1.left"),sQuery(id+"F0.wireOp",EDGE,"E1.right"),sQuery(id+"F0.wireOp",EDGE,"E2.filletArc"),sQuery(id+"F0.wireOp",EDGE,"E3.filletArc"),sQuery(id+"F0.wireOp",EDGE,"E4.filletArc"),sQuery(id+"F0.wireOp",EDGE,"E5.filletArc"),sQuery(id+"F0.wireOp",EDGE,"E6.filletArc"),sQuery(id+"F0.wireOp",EDGE,"E7.filletArc"),sQuery(id+"F0.wireOp",EDGE,"E8.filletArc"),sQuery(id+"F0.wireOp",EDGE,"E9.filletArc")])]}),"instanceName":"1"}),"instanceName":"1"});
            var Q4;
            Q4=makeQuery(id+"F6.opExtrude","SWEPT_BODY",BODY,{"disambiguationData":[OSD([sQuery(id+"F5.wireOp",EDGE,"E10.bottom"),sQuery(id+"F5.wireOp",EDGE,"E10.top"),sQuery(id+"F5.wireOp",EDGE,"E10.left"),sQuery(id+"F5.wireOp",EDGE,"E10.right"),sQuery(id+"F5.wireOp",EDGE,"E11.bottom"),sQuery(id+"F5.wireOp",EDGE,"E11.top"),sQuery(id+"F5.wireOp",EDGE,"E11.left"),sQuery(id+"F5.wireOp",EDGE,"E11.right"),sQuery(id+"F5.wireOp",EDGE,"E12.filletArc"),sQuery(id+"F5.wireOp",EDGE,"E13.filletArc"),sQuery(id+"F5.wireOp",EDGE,"E14.filletArc"),sQuery(id+"F5.wireOp",EDGE,"E15.filletArc"),sQuery(id+"F5.wireOp",EDGE,"E16.filletArc"),sQuery(id+"F5.wireOp",EDGE,"E17.filletArc"),sQuery(id+"F5.wireOp",EDGE,"E18.filletArc"),sQuery(id+"F5.wireOp",EDGE,"E19.filletArc")])]});
            var Q5;
            Q5=makeQuery(id+"F7.opPattern","COPY",BODY,{"derivedFrom":makeQuery(id+"F6.opExtrude","SWEPT_BODY",BODY,{"disambiguationData":[OSD([sQuery(id+"F5.wireOp",EDGE,"E10.bottom"),sQuery(id+"F5.wireOp",EDGE,"E10.top"),sQuery(id+"F5.wireOp",EDGE,"E10.left"),sQuery(id+"F5.wireOp",EDGE,"E10.right"),sQuery(id+"F5.wireOp",EDGE,"E11.bottom"),sQuery(id+"F5.wireOp",EDGE,"E11.top"),sQuery(id+"F5.wireOp",EDGE,"E11.left"),sQuery(id+"F5.wireOp",EDGE,"E11.right"),sQuery(id+"F5.wireOp",EDGE,"E12.filletArc"),sQuery(id+"F5.wireOp",EDGE,"E13.filletArc"),sQuery(id+"F5.wireOp",EDGE,"E14.filletArc"),sQuery(id+"F5.wireOp",EDGE,"E15.filletArc"),sQuery(id+"F5.wireOp",EDGE,"E16.filletArc"),sQuery(id+"F5.wireOp",EDGE,"E17.filletArc"),sQuery(id+"F5.wireOp",EDGE,"E18.filletArc"),sQuery(id+"F5.wireOp",EDGE,"E19.filletArc")])]}),"instanceName":"1"});
            var Q6;
            Q6=makeQuery(id+"F8.opPattern","COPY",BODY,{"derivedFrom":makeQuery(id+"F6.opExtrude","SWEPT_BODY",BODY,{"disambiguationData":[OSD([sQuery(id+"F5.wireOp",EDGE,"E10.bottom"),sQuery(id+"F5.wireOp",EDGE,"E10.top"),sQuery(id+"F5.wireOp",EDGE,"E10.left"),sQuery(id+"F5.wireOp",EDGE,"E10.right"),sQuery(id+"F5.wireOp",EDGE,"E11.bottom"),sQuery(id+"F5.wireOp",EDGE,"E11.top"),sQuery(id+"F5.wireOp",EDGE,"E11.left"),sQuery(id+"F5.wireOp",EDGE,"E11.right"),sQuery(id+"F5.wireOp",EDGE,"E12.filletArc"),sQuery(id+"F5.wireOp",EDGE,"E13.filletArc"),sQuery(id+"F5.wireOp",EDGE,"E14.filletArc"),sQuery(id+"F5.wireOp",EDGE,"E15.filletArc"),sQuery(id+"F5.wireOp",EDGE,"E16.filletArc"),sQuery(id+"F5.wireOp",EDGE,"E17.filletArc"),sQuery(id+"F5.wireOp",EDGE,"E18.filletArc"),sQuery(id+"F5.wireOp",EDGE,"E19.filletArc")])]}),"instanceName":"1"});
            var Q7;
            Q7=makeQuery(id+"F8.opPattern","COPY",BODY,{"derivedFrom":makeQuery(id+"F7.opPattern","COPY",BODY,{"derivedFrom":makeQuery(id+"F6.opExtrude","SWEPT_BODY",BODY,{"disambiguationData":[OSD([sQuery(id+"F5.wireOp",EDGE,"E10.bottom"),sQuery(id+"F5.wireOp",EDGE,"E10.top"),sQuery(id+"F5.wireOp",EDGE,"E10.left"),sQuery(id+"F5.wireOp",EDGE,"E10.right"),sQuery(id+"F5.wireOp",EDGE,"E11.bottom"),sQuery(id+"F5.wireOp",EDGE,"E11.top"),sQuery(id+"F5.wireOp",EDGE,"E11.left"),sQuery(id+"F5.wireOp",EDGE,"E11.right"),sQuery(id+"F5.wireOp",EDGE,"E12.filletArc"),sQuery(id+"F5.wireOp",EDGE,"E13.filletArc"),sQuery(id+"F5.wireOp",EDGE,"E14.filletArc"),sQuery(id+"F5.wireOp",EDGE,"E15.filletArc"),sQuery(id+"F5.wireOp",EDGE,"E16.filletArc"),sQuery(id+"F5.wireOp",EDGE,"E17.filletArc"),sQuery(id+"F5.wireOp",EDGE,"E18.filletArc"),sQuery(id+"F5.wireOp",EDGE,"E19.filletArc")])]}),"instanceName":"1"}),"instanceName":"1"});
            var Q8;
            Q8=makeQuery(id+"F10.opExtrude","SWEPT_BODY",BODY,{"disambiguationData":[OSD([sQuery(id+"F9.wireOp",EDGE,"E20"),sQuery(id+"F9.wireOp",EDGE,"E21"),sQuery(id+"F9.wireOp",EDGE,"E22"),sQuery(id+"F9.wireOp",EDGE,"E23"),sQuery(id+"F9.wireOp",EDGE,"E24"),sQuery(id+"F9.wireOp",EDGE,"E25"),sQuery(id+"F9.wireOp",EDGE,"E26.filletArc"),sQuery(id+"F9.wireOp",EDGE,"E27.filletArc"),sQuery(id+"F9.wireOp",EDGE,"E28.filletArc")])]});
            var Q9;
            Q9=makeQuery(id+"F11.opPattern","COPY",BODY,{"derivedFrom":makeQuery(id+"F10.opExtrude","SWEPT_BODY",BODY,{"disambiguationData":[OSD([sQuery(id+"F9.wireOp",EDGE,"E20"),sQuery(id+"F9.wireOp",EDGE,"E21"),sQuery(id+"F9.wireOp",EDGE,"E22"),sQuery(id+"F9.wireOp",EDGE,"E23"),sQuery(id+"F9.wireOp",EDGE,"E24"),sQuery(id+"F9.wireOp",EDGE,"E25"),sQuery(id+"F9.wireOp",EDGE,"E26.filletArc"),sQuery(id+"F9.wireOp",EDGE,"E27.filletArc"),sQuery(id+"F9.wireOp",EDGE,"E28.filletArc")])]}),"instanceName":"1"});
            var Q10;
            Q10=makeQuery(id+"F14.opPattern","COPY",BODY,{"derivedFrom":makeQuery(id+"F11.opPattern","COPY",BODY,{"derivedFrom":makeQuery(id+"F10.opExtrude","SWEPT_BODY",BODY,{"disambiguationData":[OSD([sQuery(id+"F9.wireOp",EDGE,"E20"),sQuery(id+"F9.wireOp",EDGE,"E21"),sQuery(id+"F9.wireOp",EDGE,"E22"),sQuery(id+"F9.wireOp",EDGE,"E23"),sQuery(id+"F9.wireOp",EDGE,"E24"),sQuery(id+"F9.wireOp",EDGE,"E25"),sQuery(id+"F9.wireOp",EDGE,"E26.filletArc"),sQuery(id+"F9.wireOp",EDGE,"E27.filletArc"),sQuery(id+"F9.wireOp",EDGE,"E28.filletArc")])]}),"instanceName":"1"}),"instanceName":"1"});
            var Q11;
            Q11=makeQuery(id+"F15.opPattern","COPY",BODY,{"derivedFrom":makeQuery(id+"F14.opPattern","COPY",BODY,{"derivedFrom":makeQuery(id+"F11.opPattern","COPY",BODY,{"derivedFrom":makeQuery(id+"F10.opExtrude","SWEPT_BODY",BODY,{"disambiguationData":[OSD([sQuery(id+"F9.wireOp",EDGE,"E20"),sQuery(id+"F9.wireOp",EDGE,"E21"),sQuery(id+"F9.wireOp",EDGE,"E22"),sQuery(id+"F9.wireOp",EDGE,"E23"),sQuery(id+"F9.wireOp",EDGE,"E24"),sQuery(id+"F9.wireOp",EDGE,"E25"),sQuery(id+"F9.wireOp",EDGE,"E26.filletArc"),sQuery(id+"F9.wireOp",EDGE,"E27.filletArc"),sQuery(id+"F9.wireOp",EDGE,"E28.filletArc")])]}),"instanceName":"1"}),"instanceName":"1"}),"instanceName":"1"});
            var Q12;
            Q12=makeQuery(id+"F16.opPattern","COPY",BODY,{"derivedFrom":makeQuery(id+"F15.opPattern","COPY",BODY,{"derivedFrom":makeQuery(id+"F14.opPattern","COPY",BODY,{"derivedFrom":makeQuery(id+"F11.opPattern","COPY",BODY,{"derivedFrom":makeQuery(id+"F10.opExtrude","SWEPT_BODY",BODY,{"disambiguationData":[OSD([sQuery(id+"F9.wireOp",EDGE,"E20"),sQuery(id+"F9.wireOp",EDGE,"E21"),sQuery(id+"F9.wireOp",EDGE,"E22"),sQuery(id+"F9.wireOp",EDGE,"E23"),sQuery(id+"F9.wireOp",EDGE,"E24"),sQuery(id+"F9.wireOp",EDGE,"E25"),sQuery(id+"F9.wireOp",EDGE,"E26.filletArc"),sQuery(id+"F9.wireOp",EDGE,"E27.filletArc"),sQuery(id+"F9.wireOp",EDGE,"E28.filletArc")])]}),"instanceName":"1"}),"instanceName":"1"}),"instanceName":"1"}),"instanceName":"1"});
            var Q13;
            Q13=makeQuery(id+"F17.opPattern","COPY",BODY,{"derivedFrom":makeQuery(id+"F16.opPattern","COPY",BODY,{"derivedFrom":makeQuery(id+"F15.opPattern","COPY",BODY,{"derivedFrom":makeQuery(id+"F14.opPattern","COPY",BODY,{"derivedFrom":makeQuery(id+"F11.opPattern","COPY",BODY,{"derivedFrom":makeQuery(id+"F10.opExtrude","SWEPT_BODY",BODY,{"disambiguationData":[OSD([sQuery(id+"F9.wireOp",EDGE,"E20"),sQuery(id+"F9.wireOp",EDGE,"E21"),sQuery(id+"F9.wireOp",EDGE,"E22"),sQuery(id+"F9.wireOp",EDGE,"E23"),sQuery(id+"F9.wireOp",EDGE,"E24"),sQuery(id+"F9.wireOp",EDGE,"E25"),sQuery(id+"F9.wireOp",EDGE,"E26.filletArc"),sQuery(id+"F9.wireOp",EDGE,"E27.filletArc"),sQuery(id+"F9.wireOp",EDGE,"E28.filletArc")])]}),"instanceName":"1"}),"instanceName":"1"}),"instanceName":"1"}),"instanceName":"1"}),"instanceName":"1"});
            var Q14;
            Q14=makeQuery(id+"F18.opPattern","COPY",BODY,{"derivedFrom":makeQuery(id+"F17.opPattern","COPY",BODY,{"derivedFrom":makeQuery(id+"F16.opPattern","COPY",BODY,{"derivedFrom":makeQuery(id+"F15.opPattern","COPY",BODY,{"derivedFrom":makeQuery(id+"F14.opPattern","COPY",BODY,{"derivedFrom":makeQuery(id+"F10.opExtrude","SWEPT_BODY",BODY,{"disambiguationData":[OSD([sQuery(id+"F9.wireOp",EDGE,"E20"),sQuery(id+"F9.wireOp",EDGE,"E21"),sQuery(id+"F9.wireOp",EDGE,"E22"),sQuery(id+"F9.wireOp",EDGE,"E23"),sQuery(id+"F9.wireOp",EDGE,"E24"),sQuery(id+"F9.wireOp",EDGE,"E25"),sQuery(id+"F9.wireOp",EDGE,"E26.filletArc"),sQuery(id+"F9.wireOp",EDGE,"E27.filletArc"),sQuery(id+"F9.wireOp",EDGE,"E28.filletArc")])]}),"instanceName":"1"}),"instanceName":"1"}),"instanceName":"1"}),"instanceName":"1"}),"instanceName":"1"});
            var Q15;
            Q15=makeQuery(id+"F18.opPattern","COPY",BODY,{"derivedFrom":makeQuery(id+"F17.opPattern","COPY",BODY,{"derivedFrom":makeQuery(id+"F16.opPattern","COPY",BODY,{"derivedFrom":makeQuery(id+"F15.opPattern","COPY",BODY,{"derivedFrom":makeQuery(id+"F14.opPattern","COPY",BODY,{"derivedFrom":makeQuery(id+"F11.opPattern","COPY",BODY,{"derivedFrom":makeQuery(id+"F10.opExtrude","SWEPT_BODY",BODY,{"disambiguationData":[OSD([sQuery(id+"F9.wireOp",EDGE,"E20"),sQuery(id+"F9.wireOp",EDGE,"E21"),sQuery(id+"F9.wireOp",EDGE,"E22"),sQuery(id+"F9.wireOp",EDGE,"E23"),sQuery(id+"F9.wireOp",EDGE,"E24"),sQuery(id+"F9.wireOp",EDGE,"E25"),sQuery(id+"F9.wireOp",EDGE,"E26.filletArc"),sQuery(id+"F9.wireOp",EDGE,"E27.filletArc"),sQuery(id+"F9.wireOp",EDGE,"E28.filletArc")])]}),"instanceName":"1"}),"instanceName":"1"}),"instanceName":"1"}),"instanceName":"1"}),"instanceName":"1"}),"instanceName":"1"});
            var Q16;
            Q16=makeQuery(id+"F24.opPattern","COPY",BODY,{"derivedFrom":makeQuery(id+"F22.opPattern","COPY",BODY,{"derivedFrom":makeQuery(id+"F20.opExtrude","SWEPT_BODY",BODY,{"disambiguationData":[OSD([sQuery(id+"F19.wireOp",EDGE,"E29.bottom"),sQuery(id+"F19.wireOp",EDGE,"E29.top"),sQuery(id+"F19.wireOp",EDGE,"E29.left"),sQuery(id+"F19.wireOp",EDGE,"E29.right")])]}),"instanceName":"1"}),"instanceName":"1"});
            var Q17;
            Q17=makeQuery(id+"F25.opPattern","COPY",BODY,{"derivedFrom":makeQuery(id+"F24.opPattern","COPY",BODY,{"derivedFrom":makeQuery(id+"F21.opPattern","COPY",BODY,{"derivedFrom":makeQuery(id+"F20.opExtrude","SWEPT_BODY",BODY,{"disambiguationData":[OSD([sQuery(id+"F19.wireOp",EDGE,"E29.bottom"),sQuery(id+"F19.wireOp",EDGE,"E29.top"),sQuery(id+"F19.wireOp",EDGE,"E29.left"),sQuery(id+"F19.wireOp",EDGE,"E29.right")])]}),"instanceName":"1"}),"instanceName":"1"}),"instanceName":"1"});
            var Q18;
            Q18=makeQuery(id+"F29.opPattern","COPY",BODY,{"derivedFrom":makeQuery(id+"F28.opPattern","COPY",BODY,{"derivedFrom":makeQuery(id+"F27.opPattern","COPY",BODY,{"derivedFrom":makeQuery(id+"F26.opPattern","COPY",BODY,{"derivedFrom":makeQuery(id+"F25.opPattern","COPY",BODY,{"derivedFrom":makeQuery(id+"F22.opPattern","COPY",BODY,{"derivedFrom":makeQuery(id+"F20.opExtrude","SWEPT_BODY",BODY,{"disambiguationData":[OSD([sQuery(id+"F19.wireOp",EDGE,"E29.bottom"),sQuery(id+"F19.wireOp",EDGE,"E29.top"),sQuery(id+"F19.wireOp",EDGE,"E29.left"),sQuery(id+"F19.wireOp",EDGE,"E29.right")])]}),"instanceName":"1"}),"instanceName":"1"}),"instanceName":"1"}),"instanceName":"1"}),"instanceName":"1"}),"instanceName":"1"});
            var Q19;
            Q19=makeQuery(id+"F29.opPattern","COPY",BODY,{"derivedFrom":makeQuery(id+"F28.opPattern","COPY",BODY,{"derivedFrom":makeQuery(id+"F27.opPattern","COPY",BODY,{"derivedFrom":makeQuery(id+"F26.opPattern","COPY",BODY,{"derivedFrom":makeQuery(id+"F25.opPattern","COPY",BODY,{"derivedFrom":makeQuery(id+"F24.opPattern","COPY",BODY,{"derivedFrom":makeQuery(id+"F20.opExtrude","SWEPT_BODY",BODY,{"disambiguationData":[OSD([sQuery(id+"F19.wireOp",EDGE,"E29.bottom"),sQuery(id+"F19.wireOp",EDGE,"E29.top"),sQuery(id+"F19.wireOp",EDGE,"E29.left"),sQuery(id+"F19.wireOp",EDGE,"E29.right")])]}),"instanceName":"1"}),"instanceName":"1"}),"instanceName":"1"}),"instanceName":"1"}),"instanceName":"1"}),"instanceName":"1"});
            var Q20;
            Q20=makeQuery(id+"F29.opPattern","COPY",BODY,{"derivedFrom":makeQuery(id+"F28.opPattern","COPY",BODY,{"derivedFrom":makeQuery(id+"F27.opPattern","COPY",BODY,{"derivedFrom":makeQuery(id+"F26.opPattern","COPY",BODY,{"derivedFrom":makeQuery(id+"F25.opPattern","COPY",BODY,{"derivedFrom":makeQuery(id+"F24.opPattern","COPY",BODY,{"derivedFrom":makeQuery(id+"F21.opPattern","COPY",BODY,{"derivedFrom":makeQuery(id+"F20.opExtrude","SWEPT_BODY",BODY,{"disambiguationData":[OSD([sQuery(id+"F19.wireOp",EDGE,"E29.bottom"),sQuery(id+"F19.wireOp",EDGE,"E29.top"),sQuery(id+"F19.wireOp",EDGE,"E29.left"),sQuery(id+"F19.wireOp",EDGE,"E29.right")])]}),"instanceName":"1"}),"instanceName":"1"}),"instanceName":"1"}),"instanceName":"1"}),"instanceName":"1"}),"instanceName":"1"}),"instanceName":"1"});
            var Q21;
            Q21=makeQuery(id+"F29.opPattern","COPY",BODY,{"derivedFrom":makeQuery(id+"F28.opPattern","COPY",BODY,{"derivedFrom":makeQuery(id+"F27.opPattern","COPY",BODY,{"derivedFrom":makeQuery(id+"F26.opPattern","COPY",BODY,{"derivedFrom":makeQuery(id+"F25.opPattern","COPY",BODY,{"derivedFrom":makeQuery(id+"F24.opPattern","COPY",BODY,{"derivedFrom":makeQuery(id+"F22.opPattern","COPY",BODY,{"derivedFrom":makeQuery(id+"F20.opExtrude","SWEPT_BODY",BODY,{"disambiguationData":[OSD([sQuery(id+"F19.wireOp",EDGE,"E29.bottom"),sQuery(id+"F19.wireOp",EDGE,"E29.top"),sQuery(id+"F19.wireOp",EDGE,"E29.left"),sQuery(id+"F19.wireOp",EDGE,"E29.right")])]}),"instanceName":"1"}),"instanceName":"1"}),"instanceName":"1"}),"instanceName":"1"}),"instanceName":"1"}),"instanceName":"1"}),"instanceName":"1"});
            var Q22;
            Q22=makeQuery(id+"F29.opPattern","COPY",BODY,{"derivedFrom":makeQuery(id+"F28.opPattern","COPY",BODY,{"derivedFrom":makeQuery(id+"F27.opPattern","COPY",BODY,{"derivedFrom":makeQuery(id+"F26.opPattern","COPY",BODY,{"derivedFrom":makeQuery(id+"F25.opPattern","COPY",BODY,{"derivedFrom":makeQuery(id+"F24.opPattern","COPY",BODY,{"derivedFrom":makeQuery(id+"F23.opPattern","COPY",BODY,{"derivedFrom":makeQuery(id+"F21.opPattern","COPY",BODY,{"derivedFrom":makeQuery(id+"F20.opExtrude","SWEPT_BODY",BODY,{"disambiguationData":[OSD([sQuery(id+"F19.wireOp",EDGE,"E29.bottom"),sQuery(id+"F19.wireOp",EDGE,"E29.top"),sQuery(id+"F19.wireOp",EDGE,"E29.left"),sQuery(id+"F19.wireOp",EDGE,"E29.right")])]}),"instanceName":"1"}),"instanceName":"1"}),"instanceName":"1"}),"instanceName":"1"}),"instanceName":"1"}),"instanceName":"1"}),"instanceName":"1"}),"instanceName":"1"});
            var Q23;
            Q23=makeQuery(id+"F31.opExtrude","SWEPT_BODY",BODY,{"disambiguationData":[OSD([sQuery(id+"F30.wireOp",EDGE,"E30.bottom"),sQuery(id+"F30.wireOp",EDGE,"E30.top"),sQuery(id+"F30.wireOp",EDGE,"E30.left"),sQuery(id+"F30.wireOp",EDGE,"E30.right")])]});
            var Q24;
            Q24=makeQuery(id+"F33.opExtrude","SWEPT_BODY",BODY,{"disambiguationData":[OSD([sQuery(id+"F32.wireOp",EDGE,"E31.bottom"),sQuery(id+"F32.wireOp",EDGE,"E31.top"),sQuery(id+"F32.wireOp",EDGE,"E31.left"),sQuery(id+"F32.wireOp",EDGE,"E31.right")])]});
            var Q25;
            Q25=makeQuery(id+"F35.opExtrude","SWEPT_BODY",BODY,{"disambiguationData":[OSD([sQuery(id+"F34.wireOp",EDGE,"E32.bottom"),sQuery(id+"F34.wireOp",EDGE,"E32.top"),sQuery(id+"F34.wireOp",EDGE,"E32.left"),sQuery(id+"F34.wireOp",EDGE,"E32.right")])]});
            var Q26;
            Q26=makeQuery(id+"F37.opExtrude","SWEPT_BODY",BODY,{"disambiguationData":[OSD([sQuery(id+"F36.wireOp",EDGE,"E33.bottom"),sQuery(id+"F36.wireOp",EDGE,"E33.top"),sQuery(id+"F36.wireOp",EDGE,"E33.left"),sQuery(id+"F36.wireOp",EDGE,"E33.right")])]});
            var Q27;
            Q27=makeQuery(id+"F38.opPattern","COPY",BODY,{"derivedFrom":makeQuery(id+"F37.opExtrude","SWEPT_BODY",BODY,{"disambiguationData":[OSD([sQuery(id+"F36.wireOp",EDGE,"E33.bottom"),sQuery(id+"F36.wireOp",EDGE,"E33.top"),sQuery(id+"F36.wireOp",EDGE,"E33.left"),sQuery(id+"F36.wireOp",EDGE,"E33.right")])]}),"instanceName":"1"});
            var Q28;
            Q28=makeQuery(id+"F40.opPattern","COPY",BODY,{"derivedFrom":makeQuery(id+"F37.opExtrude","SWEPT_BODY",BODY,{"disambiguationData":[OSD([sQuery(id+"F36.wireOp",EDGE,"E33.bottom"),sQuery(id+"F36.wireOp",EDGE,"E33.top"),sQuery(id+"F36.wireOp",EDGE,"E33.left"),sQuery(id+"F36.wireOp",EDGE,"E33.right")])]}),"instanceName":"1"});
            var Q29;
            Q29=makeQuery(id+"F40.opPattern","COPY",BODY,{"derivedFrom":makeQuery(id+"F38.opPattern","COPY",BODY,{"derivedFrom":makeQuery(id+"F37.opExtrude","SWEPT_BODY",BODY,{"disambiguationData":[OSD([sQuery(id+"F36.wireOp",EDGE,"E33.bottom"),sQuery(id+"F36.wireOp",EDGE,"E33.top"),sQuery(id+"F36.wireOp",EDGE,"E33.left"),sQuery(id+"F36.wireOp",EDGE,"E33.right")])]}),"instanceName":"1"}),"instanceName":"1"});
            var Q30;
            Q30=makeQuery(id+"F42.opExtrude","SWEPT_BODY",BODY,{"disambiguationData":[OSD([sQuery(id+"F41.wireOp",EDGE,"E34.bottom"),sQuery(id+"F41.wireOp",EDGE,"E34.top"),sQuery(id+"F41.wireOp",EDGE,"E34.left"),sQuery(id+"F41.wireOp",EDGE,"E34.right")])]});
            var Q31;
            Q31=makeQuery(id+"F43.opPattern","COPY",BODY,{"derivedFrom":makeQuery(id+"F42.opExtrude","SWEPT_BODY",BODY,{"disambiguationData":[OSD([sQuery(id+"F41.wireOp",EDGE,"E34.bottom"),sQuery(id+"F41.wireOp",EDGE,"E34.top"),sQuery(id+"F41.wireOp",EDGE,"E34.left"),sQuery(id+"F41.wireOp",EDGE,"E34.right")])]}),"instanceName":"1"});
            var Q32;
            Q32=makeQuery(id+"F44.opPattern","COPY",BODY,{"derivedFrom":makeQuery(id+"F43.opPattern","COPY",BODY,{"derivedFrom":makeQuery(id+"F42.opExtrude","SWEPT_BODY",BODY,{"disambiguationData":[OSD([sQuery(id+"F41.wireOp",EDGE,"E34.bottom"),sQuery(id+"F41.wireOp",EDGE,"E34.top"),sQuery(id+"F41.wireOp",EDGE,"E34.left"),sQuery(id+"F41.wireOp",EDGE,"E34.right")])]}),"instanceName":"1"}),"instanceName":"1"});
            var Q33;
            Q33=makeQuery(id+"F45.opPattern","COPY",BODY,{"derivedFrom":makeQuery(id+"F44.opPattern","COPY",BODY,{"derivedFrom":makeQuery(id+"F43.opPattern","COPY",BODY,{"derivedFrom":makeQuery(id+"F42.opExtrude","SWEPT_BODY",BODY,{"disambiguationData":[OSD([sQuery(id+"F41.wireOp",EDGE,"E34.bottom"),sQuery(id+"F41.wireOp",EDGE,"E34.top"),sQuery(id+"F41.wireOp",EDGE,"E34.left"),sQuery(id+"F41.wireOp",EDGE,"E34.right")])]}),"instanceName":"1"}),"instanceName":"1"}),"instanceName":"1"});
            var Q34;
            Q34=makeQuery(id+"F46.opPattern","COPY",BODY,{"derivedFrom":makeQuery(id+"F45.opPattern","COPY",BODY,{"derivedFrom":makeQuery(id+"F44.opPattern","COPY",BODY,{"derivedFrom":makeQuery(id+"F43.opPattern","COPY",BODY,{"derivedFrom":makeQuery(id+"F42.opExtrude","SWEPT_BODY",BODY,{"disambiguationData":[OSD([sQuery(id+"F41.wireOp",EDGE,"E34.bottom"),sQuery(id+"F41.wireOp",EDGE,"E34.top"),sQuery(id+"F41.wireOp",EDGE,"E34.left"),sQuery(id+"F41.wireOp",EDGE,"E34.right")])]}),"instanceName":"1"}),"instanceName":"1"}),"instanceName":"1"}),"instanceName":"1"});
            var Q35;
            Q35=makeQuery(id+"F47.opPattern","COPY",BODY,{"derivedFrom":makeQuery(id+"F46.opPattern","COPY",BODY,{"derivedFrom":makeQuery(id+"F45.opPattern","COPY",BODY,{"derivedFrom":makeQuery(id+"F44.opPattern","COPY",BODY,{"derivedFrom":makeQuery(id+"F43.opPattern","COPY",BODY,{"derivedFrom":makeQuery(id+"F42.opExtrude","SWEPT_BODY",BODY,{"disambiguationData":[OSD([sQuery(id+"F41.wireOp",EDGE,"E34.bottom"),sQuery(id+"F41.wireOp",EDGE,"E34.top"),sQuery(id+"F41.wireOp",EDGE,"E34.left"),sQuery(id+"F41.wireOp",EDGE,"E34.right")])]}),"instanceName":"1"}),"instanceName":"1"}),"instanceName":"1"}),"instanceName":"1"}),"instanceName":"1"});
            var Q36;
            Q36=makeQuery(id+"F14.opPattern","COPY",BODY,{"derivedFrom":makeQuery(id+"F10.opExtrude","SWEPT_BODY",BODY,{"disambiguationData":[OSD([sQuery(id+"F9.wireOp",EDGE,"E20"),sQuery(id+"F9.wireOp",EDGE,"E21"),sQuery(id+"F9.wireOp",EDGE,"E22"),sQuery(id+"F9.wireOp",EDGE,"E23"),sQuery(id+"F9.wireOp",EDGE,"E24"),sQuery(id+"F9.wireOp",EDGE,"E25"),sQuery(id+"F9.wireOp",EDGE,"E26.filletArc"),sQuery(id+"F9.wireOp",EDGE,"E27.filletArc"),sQuery(id+"F9.wireOp",EDGE,"E28.filletArc")])]}),"instanceName":"1"});
            var Q37;
            Q37=makeQuery(id+"F15.opPattern","COPY",BODY,{"derivedFrom":makeQuery(id+"F14.opPattern","COPY",BODY,{"derivedFrom":makeQuery(id+"F10.opExtrude","SWEPT_BODY",BODY,{"disambiguationData":[OSD([sQuery(id+"F9.wireOp",EDGE,"E20"),sQuery(id+"F9.wireOp",EDGE,"E21"),sQuery(id+"F9.wireOp",EDGE,"E22"),sQuery(id+"F9.wireOp",EDGE,"E23"),sQuery(id+"F9.wireOp",EDGE,"E24"),sQuery(id+"F9.wireOp",EDGE,"E25"),sQuery(id+"F9.wireOp",EDGE,"E26.filletArc"),sQuery(id+"F9.wireOp",EDGE,"E27.filletArc"),sQuery(id+"F9.wireOp",EDGE,"E28.filletArc")])]}),"instanceName":"1"}),"instanceName":"1"});
            var Q38;
            Q38=makeQuery(id+"F16.opPattern","COPY",BODY,{"derivedFrom":makeQuery(id+"F15.opPattern","COPY",BODY,{"derivedFrom":makeQuery(id+"F14.opPattern","COPY",BODY,{"derivedFrom":makeQuery(id+"F10.opExtrude","SWEPT_BODY",BODY,{"disambiguationData":[OSD([sQuery(id+"F9.wireOp",EDGE,"E20"),sQuery(id+"F9.wireOp",EDGE,"E21"),sQuery(id+"F9.wireOp",EDGE,"E22"),sQuery(id+"F9.wireOp",EDGE,"E23"),sQuery(id+"F9.wireOp",EDGE,"E24"),sQuery(id+"F9.wireOp",EDGE,"E25"),sQuery(id+"F9.wireOp",EDGE,"E26.filletArc"),sQuery(id+"F9.wireOp",EDGE,"E27.filletArc"),sQuery(id+"F9.wireOp",EDGE,"E28.filletArc")])]}),"instanceName":"1"}),"instanceName":"1"}),"instanceName":"1"});
            var Q39;
            Q39=makeQuery(id+"F17.opPattern","COPY",BODY,{"derivedFrom":makeQuery(id+"F16.opPattern","COPY",BODY,{"derivedFrom":makeQuery(id+"F15.opPattern","COPY",BODY,{"derivedFrom":makeQuery(id+"F14.opPattern","COPY",BODY,{"derivedFrom":makeQuery(id+"F10.opExtrude","SWEPT_BODY",BODY,{"disambiguationData":[OSD([sQuery(id+"F9.wireOp",EDGE,"E20"),sQuery(id+"F9.wireOp",EDGE,"E21"),sQuery(id+"F9.wireOp",EDGE,"E22"),sQuery(id+"F9.wireOp",EDGE,"E23"),sQuery(id+"F9.wireOp",EDGE,"E24"),sQuery(id+"F9.wireOp",EDGE,"E25"),sQuery(id+"F9.wireOp",EDGE,"E26.filletArc"),sQuery(id+"F9.wireOp",EDGE,"E27.filletArc"),sQuery(id+"F9.wireOp",EDGE,"E28.filletArc")])]}),"instanceName":"1"}),"instanceName":"1"}),"instanceName":"1"}),"instanceName":"1"});
            var Q40;
            Q40=makeQuery(id+"F21.opPattern","COPY",BODY,{"derivedFrom":makeQuery(id+"F20.opExtrude","SWEPT_BODY",BODY,{"disambiguationData":[OSD([sQuery(id+"F19.wireOp",EDGE,"E29.bottom"),sQuery(id+"F19.wireOp",EDGE,"E29.top"),sQuery(id+"F19.wireOp",EDGE,"E29.left"),sQuery(id+"F19.wireOp",EDGE,"E29.right")])]}),"instanceName":"1"});
            var Q41;
            Q41=makeQuery(id+"F24.opPattern","COPY",BODY,{"derivedFrom":makeQuery(id+"F20.opExtrude","SWEPT_BODY",BODY,{"disambiguationData":[OSD([sQuery(id+"F19.wireOp",EDGE,"E29.bottom"),sQuery(id+"F19.wireOp",EDGE,"E29.top"),sQuery(id+"F19.wireOp",EDGE,"E29.left"),sQuery(id+"F19.wireOp",EDGE,"E29.right")])]}),"instanceName":"1"});
            var Q42;
            Q42=makeQuery(id+"F24.opPattern","COPY",BODY,{"derivedFrom":makeQuery(id+"F21.opPattern","COPY",BODY,{"derivedFrom":makeQuery(id+"F20.opExtrude","SWEPT_BODY",BODY,{"disambiguationData":[OSD([sQuery(id+"F19.wireOp",EDGE,"E29.bottom"),sQuery(id+"F19.wireOp",EDGE,"E29.top"),sQuery(id+"F19.wireOp",EDGE,"E29.left"),sQuery(id+"F19.wireOp",EDGE,"E29.right")])]}),"instanceName":"1"}),"instanceName":"1"});
            var Q43;
            Q43=makeQuery(id+"F24.opPattern","COPY",BODY,{"derivedFrom":makeQuery(id+"F23.opPattern","COPY",BODY,{"derivedFrom":makeQuery(id+"F21.opPattern","COPY",BODY,{"derivedFrom":makeQuery(id+"F20.opExtrude","SWEPT_BODY",BODY,{"disambiguationData":[OSD([sQuery(id+"F19.wireOp",EDGE,"E29.bottom"),sQuery(id+"F19.wireOp",EDGE,"E29.top"),sQuery(id+"F19.wireOp",EDGE,"E29.left"),sQuery(id+"F19.wireOp",EDGE,"E29.right")])]}),"instanceName":"1"}),"instanceName":"1"}),"instanceName":"1"});
            var Q44;
            Q44=makeQuery(id+"F25.opPattern","COPY",BODY,{"derivedFrom":makeQuery(id+"F20.opExtrude","SWEPT_BODY",BODY,{"disambiguationData":[OSD([sQuery(id+"F19.wireOp",EDGE,"E29.bottom"),sQuery(id+"F19.wireOp",EDGE,"E29.top"),sQuery(id+"F19.wireOp",EDGE,"E29.left"),sQuery(id+"F19.wireOp",EDGE,"E29.right")])]}),"instanceName":"1"});
            var Q45;
            Q45=makeQuery(id+"F25.opPattern","COPY",BODY,{"derivedFrom":makeQuery(id+"F21.opPattern","COPY",BODY,{"derivedFrom":makeQuery(id+"F20.opExtrude","SWEPT_BODY",BODY,{"disambiguationData":[OSD([sQuery(id+"F19.wireOp",EDGE,"E29.bottom"),sQuery(id+"F19.wireOp",EDGE,"E29.top"),sQuery(id+"F19.wireOp",EDGE,"E29.left"),sQuery(id+"F19.wireOp",EDGE,"E29.right")])]}),"instanceName":"1"}),"instanceName":"1"});
            var Q46;
            Q46=makeQuery(id+"F25.opPattern","COPY",BODY,{"derivedFrom":makeQuery(id+"F23.opPattern","COPY",BODY,{"derivedFrom":makeQuery(id+"F21.opPattern","COPY",BODY,{"derivedFrom":makeQuery(id+"F20.opExtrude","SWEPT_BODY",BODY,{"disambiguationData":[OSD([sQuery(id+"F19.wireOp",EDGE,"E29.bottom"),sQuery(id+"F19.wireOp",EDGE,"E29.top"),sQuery(id+"F19.wireOp",EDGE,"E29.left"),sQuery(id+"F19.wireOp",EDGE,"E29.right")])]}),"instanceName":"1"}),"instanceName":"1"}),"instanceName":"1"});
            var Q47;
            Q47=makeQuery(id+"F25.opPattern","COPY",BODY,{"derivedFrom":makeQuery(id+"F24.opPattern","COPY",BODY,{"derivedFrom":makeQuery(id+"F20.opExtrude","SWEPT_BODY",BODY,{"disambiguationData":[OSD([sQuery(id+"F19.wireOp",EDGE,"E29.bottom"),sQuery(id+"F19.wireOp",EDGE,"E29.top"),sQuery(id+"F19.wireOp",EDGE,"E29.left"),sQuery(id+"F19.wireOp",EDGE,"E29.right")])]}),"instanceName":"1"}),"instanceName":"1"});
            var Q48;
            Q48=makeQuery(id+"F25.opPattern","COPY",BODY,{"derivedFrom":makeQuery(id+"F24.opPattern","COPY",BODY,{"derivedFrom":makeQuery(id+"F22.opPattern","COPY",BODY,{"derivedFrom":makeQuery(id+"F20.opExtrude","SWEPT_BODY",BODY,{"disambiguationData":[OSD([sQuery(id+"F19.wireOp",EDGE,"E29.bottom"),sQuery(id+"F19.wireOp",EDGE,"E29.top"),sQuery(id+"F19.wireOp",EDGE,"E29.left"),sQuery(id+"F19.wireOp",EDGE,"E29.right")])]}),"instanceName":"1"}),"instanceName":"1"}),"instanceName":"1"});
            var Q49;
            Q49=makeQuery(id+"F25.opPattern","COPY",BODY,{"derivedFrom":makeQuery(id+"F24.opPattern","COPY",BODY,{"derivedFrom":makeQuery(id+"F23.opPattern","COPY",BODY,{"derivedFrom":makeQuery(id+"F21.opPattern","COPY",BODY,{"derivedFrom":makeQuery(id+"F20.opExtrude","SWEPT_BODY",BODY,{"disambiguationData":[OSD([sQuery(id+"F19.wireOp",EDGE,"E29.bottom"),sQuery(id+"F19.wireOp",EDGE,"E29.top"),sQuery(id+"F19.wireOp",EDGE,"E29.left"),sQuery(id+"F19.wireOp",EDGE,"E29.right")])]}),"instanceName":"1"}),"instanceName":"1"}),"instanceName":"1"}),"instanceName":"1"});
            var Q50;
            Q50=makeQuery(id+"F26.opPattern","COPY",BODY,{"derivedFrom":makeQuery(id+"F25.opPattern","COPY",BODY,{"derivedFrom":makeQuery(id+"F22.opPattern","COPY",BODY,{"derivedFrom":makeQuery(id+"F20.opExtrude","SWEPT_BODY",BODY,{"disambiguationData":[OSD([sQuery(id+"F19.wireOp",EDGE,"E29.bottom"),sQuery(id+"F19.wireOp",EDGE,"E29.top"),sQuery(id+"F19.wireOp",EDGE,"E29.left"),sQuery(id+"F19.wireOp",EDGE,"E29.right")])]}),"instanceName":"1"}),"instanceName":"1"}),"instanceName":"1"});
            var Q51;
            Q51=makeQuery(id+"F26.opPattern","COPY",BODY,{"derivedFrom":makeQuery(id+"F25.opPattern","COPY",BODY,{"derivedFrom":makeQuery(id+"F24.opPattern","COPY",BODY,{"derivedFrom":makeQuery(id+"F20.opExtrude","SWEPT_BODY",BODY,{"disambiguationData":[OSD([sQuery(id+"F19.wireOp",EDGE,"E29.bottom"),sQuery(id+"F19.wireOp",EDGE,"E29.top"),sQuery(id+"F19.wireOp",EDGE,"E29.left"),sQuery(id+"F19.wireOp",EDGE,"E29.right")])]}),"instanceName":"1"}),"instanceName":"1"}),"instanceName":"1"});
            var Q52;
            Q52=makeQuery(id+"F26.opPattern","COPY",BODY,{"derivedFrom":makeQuery(id+"F25.opPattern","COPY",BODY,{"derivedFrom":makeQuery(id+"F24.opPattern","COPY",BODY,{"derivedFrom":makeQuery(id+"F21.opPattern","COPY",BODY,{"derivedFrom":makeQuery(id+"F20.opExtrude","SWEPT_BODY",BODY,{"disambiguationData":[OSD([sQuery(id+"F19.wireOp",EDGE,"E29.bottom"),sQuery(id+"F19.wireOp",EDGE,"E29.top"),sQuery(id+"F19.wireOp",EDGE,"E29.left"),sQuery(id+"F19.wireOp",EDGE,"E29.right")])]}),"instanceName":"1"}),"instanceName":"1"}),"instanceName":"1"}),"instanceName":"1"});
            var Q53;
            Q53=makeQuery(id+"F26.opPattern","COPY",BODY,{"derivedFrom":makeQuery(id+"F25.opPattern","COPY",BODY,{"derivedFrom":makeQuery(id+"F24.opPattern","COPY",BODY,{"derivedFrom":makeQuery(id+"F22.opPattern","COPY",BODY,{"derivedFrom":makeQuery(id+"F20.opExtrude","SWEPT_BODY",BODY,{"disambiguationData":[OSD([sQuery(id+"F19.wireOp",EDGE,"E29.bottom"),sQuery(id+"F19.wireOp",EDGE,"E29.top"),sQuery(id+"F19.wireOp",EDGE,"E29.left"),sQuery(id+"F19.wireOp",EDGE,"E29.right")])]}),"instanceName":"1"}),"instanceName":"1"}),"instanceName":"1"}),"instanceName":"1"});
            var Q54;
            Q54=makeQuery(id+"F26.opPattern","COPY",BODY,{"derivedFrom":makeQuery(id+"F25.opPattern","COPY",BODY,{"derivedFrom":makeQuery(id+"F24.opPattern","COPY",BODY,{"derivedFrom":makeQuery(id+"F23.opPattern","COPY",BODY,{"derivedFrom":makeQuery(id+"F21.opPattern","COPY",BODY,{"derivedFrom":makeQuery(id+"F20.opExtrude","SWEPT_BODY",BODY,{"disambiguationData":[OSD([sQuery(id+"F19.wireOp",EDGE,"E29.bottom"),sQuery(id+"F19.wireOp",EDGE,"E29.top"),sQuery(id+"F19.wireOp",EDGE,"E29.left"),sQuery(id+"F19.wireOp",EDGE,"E29.right")])]}),"instanceName":"1"}),"instanceName":"1"}),"instanceName":"1"}),"instanceName":"1"}),"instanceName":"1"});
            var Q55;
            Q55=makeQuery(id+"F27.opPattern","COPY",BODY,{"derivedFrom":makeQuery(id+"F26.opPattern","COPY",BODY,{"derivedFrom":makeQuery(id+"F25.opPattern","COPY",BODY,{"derivedFrom":makeQuery(id+"F23.opPattern","COPY",BODY,{"derivedFrom":makeQuery(id+"F21.opPattern","COPY",BODY,{"derivedFrom":makeQuery(id+"F20.opExtrude","SWEPT_BODY",BODY,{"disambiguationData":[OSD([sQuery(id+"F19.wireOp",EDGE,"E29.bottom"),sQuery(id+"F19.wireOp",EDGE,"E29.top"),sQuery(id+"F19.wireOp",EDGE,"E29.left"),sQuery(id+"F19.wireOp",EDGE,"E29.right")])]}),"instanceName":"1"}),"instanceName":"1"}),"instanceName":"1"}),"instanceName":"1"}),"instanceName":"1"});
            var Q56;
            Q56=makeQuery(id+"F27.opPattern","COPY",BODY,{"derivedFrom":makeQuery(id+"F26.opPattern","COPY",BODY,{"derivedFrom":makeQuery(id+"F25.opPattern","COPY",BODY,{"derivedFrom":makeQuery(id+"F24.opPattern","COPY",BODY,{"derivedFrom":makeQuery(id+"F20.opExtrude","SWEPT_BODY",BODY,{"disambiguationData":[OSD([sQuery(id+"F19.wireOp",EDGE,"E29.bottom"),sQuery(id+"F19.wireOp",EDGE,"E29.top"),sQuery(id+"F19.wireOp",EDGE,"E29.left"),sQuery(id+"F19.wireOp",EDGE,"E29.right")])]}),"instanceName":"1"}),"instanceName":"1"}),"instanceName":"1"}),"instanceName":"1"});
            var Q57;
            Q57=makeQuery(id+"F27.opPattern","COPY",BODY,{"derivedFrom":makeQuery(id+"F26.opPattern","COPY",BODY,{"derivedFrom":makeQuery(id+"F25.opPattern","COPY",BODY,{"derivedFrom":makeQuery(id+"F24.opPattern","COPY",BODY,{"derivedFrom":makeQuery(id+"F21.opPattern","COPY",BODY,{"derivedFrom":makeQuery(id+"F20.opExtrude","SWEPT_BODY",BODY,{"disambiguationData":[OSD([sQuery(id+"F19.wireOp",EDGE,"E29.bottom"),sQuery(id+"F19.wireOp",EDGE,"E29.top"),sQuery(id+"F19.wireOp",EDGE,"E29.left"),sQuery(id+"F19.wireOp",EDGE,"E29.right")])]}),"instanceName":"1"}),"instanceName":"1"}),"instanceName":"1"}),"instanceName":"1"}),"instanceName":"1"});
            var Q58;
            Q58=makeQuery(id+"F27.opPattern","COPY",BODY,{"derivedFrom":makeQuery(id+"F26.opPattern","COPY",BODY,{"derivedFrom":makeQuery(id+"F25.opPattern","COPY",BODY,{"derivedFrom":makeQuery(id+"F24.opPattern","COPY",BODY,{"derivedFrom":makeQuery(id+"F22.opPattern","COPY",BODY,{"derivedFrom":makeQuery(id+"F20.opExtrude","SWEPT_BODY",BODY,{"disambiguationData":[OSD([sQuery(id+"F19.wireOp",EDGE,"E29.bottom"),sQuery(id+"F19.wireOp",EDGE,"E29.top"),sQuery(id+"F19.wireOp",EDGE,"E29.left"),sQuery(id+"F19.wireOp",EDGE,"E29.right")])]}),"instanceName":"1"}),"instanceName":"1"}),"instanceName":"1"}),"instanceName":"1"}),"instanceName":"1"});
            var Q59;
            Q59=makeQuery(id+"F27.opPattern","COPY",BODY,{"derivedFrom":makeQuery(id+"F26.opPattern","COPY",BODY,{"derivedFrom":makeQuery(id+"F25.opPattern","COPY",BODY,{"derivedFrom":makeQuery(id+"F24.opPattern","COPY",BODY,{"derivedFrom":makeQuery(id+"F23.opPattern","COPY",BODY,{"derivedFrom":makeQuery(id+"F21.opPattern","COPY",BODY,{"derivedFrom":makeQuery(id+"F20.opExtrude","SWEPT_BODY",BODY,{"disambiguationData":[OSD([sQuery(id+"F19.wireOp",EDGE,"E29.bottom"),sQuery(id+"F19.wireOp",EDGE,"E29.top"),sQuery(id+"F19.wireOp",EDGE,"E29.left"),sQuery(id+"F19.wireOp",EDGE,"E29.right")])]}),"instanceName":"1"}),"instanceName":"1"}),"instanceName":"1"}),"instanceName":"1"}),"instanceName":"1"}),"instanceName":"1"});
            var Q60;
            Q60=makeQuery(id+"F28.opPattern","COPY",BODY,{"derivedFrom":makeQuery(id+"F27.opPattern","COPY",BODY,{"derivedFrom":makeQuery(id+"F26.opPattern","COPY",BODY,{"derivedFrom":makeQuery(id+"F25.opPattern","COPY",BODY,{"derivedFrom":makeQuery(id+"F22.opPattern","COPY",BODY,{"derivedFrom":makeQuery(id+"F20.opExtrude","SWEPT_BODY",BODY,{"disambiguationData":[OSD([sQuery(id+"F19.wireOp",EDGE,"E29.bottom"),sQuery(id+"F19.wireOp",EDGE,"E29.top"),sQuery(id+"F19.wireOp",EDGE,"E29.left"),sQuery(id+"F19.wireOp",EDGE,"E29.right")])]}),"instanceName":"1"}),"instanceName":"1"}),"instanceName":"1"}),"instanceName":"1"}),"instanceName":"1"});
            var Q61;
            Q61=makeQuery(id+"F28.opPattern","COPY",BODY,{"derivedFrom":makeQuery(id+"F27.opPattern","COPY",BODY,{"derivedFrom":makeQuery(id+"F26.opPattern","COPY",BODY,{"derivedFrom":makeQuery(id+"F25.opPattern","COPY",BODY,{"derivedFrom":makeQuery(id+"F24.opPattern","COPY",BODY,{"derivedFrom":makeQuery(id+"F20.opExtrude","SWEPT_BODY",BODY,{"disambiguationData":[OSD([sQuery(id+"F19.wireOp",EDGE,"E29.bottom"),sQuery(id+"F19.wireOp",EDGE,"E29.top"),sQuery(id+"F19.wireOp",EDGE,"E29.left"),sQuery(id+"F19.wireOp",EDGE,"E29.right")])]}),"instanceName":"1"}),"instanceName":"1"}),"instanceName":"1"}),"instanceName":"1"}),"instanceName":"1"});
            var Q62;
            Q62=makeQuery(id+"F28.opPattern","COPY",BODY,{"derivedFrom":makeQuery(id+"F27.opPattern","COPY",BODY,{"derivedFrom":makeQuery(id+"F26.opPattern","COPY",BODY,{"derivedFrom":makeQuery(id+"F25.opPattern","COPY",BODY,{"derivedFrom":makeQuery(id+"F24.opPattern","COPY",BODY,{"derivedFrom":makeQuery(id+"F21.opPattern","COPY",BODY,{"derivedFrom":makeQuery(id+"F20.opExtrude","SWEPT_BODY",BODY,{"disambiguationData":[OSD([sQuery(id+"F19.wireOp",EDGE,"E29.bottom"),sQuery(id+"F19.wireOp",EDGE,"E29.top"),sQuery(id+"F19.wireOp",EDGE,"E29.left"),sQuery(id+"F19.wireOp",EDGE,"E29.right")])]}),"instanceName":"1"}),"instanceName":"1"}),"instanceName":"1"}),"instanceName":"1"}),"instanceName":"1"}),"instanceName":"1"});
            var Q63;
            Q63=makeQuery(id+"F28.opPattern","COPY",BODY,{"derivedFrom":makeQuery(id+"F27.opPattern","COPY",BODY,{"derivedFrom":makeQuery(id+"F26.opPattern","COPY",BODY,{"derivedFrom":makeQuery(id+"F25.opPattern","COPY",BODY,{"derivedFrom":makeQuery(id+"F24.opPattern","COPY",BODY,{"derivedFrom":makeQuery(id+"F22.opPattern","COPY",BODY,{"derivedFrom":makeQuery(id+"F20.opExtrude","SWEPT_BODY",BODY,{"disambiguationData":[OSD([sQuery(id+"F19.wireOp",EDGE,"E29.bottom"),sQuery(id+"F19.wireOp",EDGE,"E29.top"),sQuery(id+"F19.wireOp",EDGE,"E29.left"),sQuery(id+"F19.wireOp",EDGE,"E29.right")])]}),"instanceName":"1"}),"instanceName":"1"}),"instanceName":"1"}),"instanceName":"1"}),"instanceName":"1"}),"instanceName":"1"});
            var Q64;
            Q64=makeQuery(id+"F29.opPattern","COPY",BODY,{"derivedFrom":makeQuery(id+"F28.opPattern","COPY",BODY,{"derivedFrom":makeQuery(id+"F27.opPattern","COPY",BODY,{"derivedFrom":makeQuery(id+"F26.opPattern","COPY",BODY,{"derivedFrom":makeQuery(id+"F25.opPattern","COPY",BODY,{"derivedFrom":makeQuery(id+"F21.opPattern","COPY",BODY,{"derivedFrom":makeQuery(id+"F20.opExtrude","SWEPT_BODY",BODY,{"disambiguationData":[OSD([sQuery(id+"F19.wireOp",EDGE,"E29.bottom"),sQuery(id+"F19.wireOp",EDGE,"E29.top"),sQuery(id+"F19.wireOp",EDGE,"E29.left"),sQuery(id+"F19.wireOp",EDGE,"E29.right")])]}),"instanceName":"1"}),"instanceName":"1"}),"instanceName":"1"}),"instanceName":"1"}),"instanceName":"1"}),"instanceName":"1"});
            var Q65;
            Q65=makeQuery(id+"F40.opPattern","COPY",BODY,{"derivedFrom":makeQuery(id+"F31.opExtrude","SWEPT_BODY",BODY,{"disambiguationData":[OSD([sQuery(id+"F30.wireOp",EDGE,"E30.bottom"),sQuery(id+"F30.wireOp",EDGE,"E30.top"),sQuery(id+"F30.wireOp",EDGE,"E30.left"),sQuery(id+"F30.wireOp",EDGE,"E30.right")])]}),"instanceName":"1"});
            var Q66;
            Q66=makeQuery(id+"F40.opPattern","COPY",BODY,{"derivedFrom":makeQuery(id+"F33.opExtrude","SWEPT_BODY",BODY,{"disambiguationData":[OSD([sQuery(id+"F32.wireOp",EDGE,"E31.bottom"),sQuery(id+"F32.wireOp",EDGE,"E31.top"),sQuery(id+"F32.wireOp",EDGE,"E31.left"),sQuery(id+"F32.wireOp",EDGE,"E31.right")])]}),"instanceName":"1"});
            var Q67;
            Q67=makeQuery(id+"F40.opPattern","COPY",BODY,{"derivedFrom":makeQuery(id+"F35.opExtrude","SWEPT_BODY",BODY,{"disambiguationData":[OSD([sQuery(id+"F34.wireOp",EDGE,"E32.bottom"),sQuery(id+"F34.wireOp",EDGE,"E32.top"),sQuery(id+"F34.wireOp",EDGE,"E32.left"),sQuery(id+"F34.wireOp",EDGE,"E32.right")])]}),"instanceName":"1"});
            var Q68;
            Q68=makeQuery(id+"F20.opExtrude","SWEPT_BODY",BODY,{"disambiguationData":[OSD([sQuery(id+"F19.wireOp",EDGE,"E29.bottom"),sQuery(id+"F19.wireOp",EDGE,"E29.top"),sQuery(id+"F19.wireOp",EDGE,"E29.left"),sQuery(id+"F19.wireOp",EDGE,"E29.right")])]});
            var Q69;
            Q69=makeQuery(id+"F22.opPattern","COPY",BODY,{"derivedFrom":makeQuery(id+"F20.opExtrude","SWEPT_BODY",BODY,{"disambiguationData":[OSD([sQuery(id+"F19.wireOp",EDGE,"E29.bottom"),sQuery(id+"F19.wireOp",EDGE,"E29.top"),sQuery(id+"F19.wireOp",EDGE,"E29.left"),sQuery(id+"F19.wireOp",EDGE,"E29.right")])]}),"instanceName":"1"});
            var Q70;
            Q70=makeQuery(id+"F23.opPattern","COPY",BODY,{"derivedFrom":makeQuery(id+"F21.opPattern","COPY",BODY,{"derivedFrom":makeQuery(id+"F20.opExtrude","SWEPT_BODY",BODY,{"disambiguationData":[OSD([sQuery(id+"F19.wireOp",EDGE,"E29.bottom"),sQuery(id+"F19.wireOp",EDGE,"E29.top"),sQuery(id+"F19.wireOp",EDGE,"E29.left"),sQuery(id+"F19.wireOp",EDGE,"E29.right")])]}),"instanceName":"1"}),"instanceName":"1"});
            var Q71;
            Q71=makeQuery(id+"F25.opPattern","COPY",BODY,{"derivedFrom":makeQuery(id+"F22.opPattern","COPY",BODY,{"derivedFrom":makeQuery(id+"F20.opExtrude","SWEPT_BODY",BODY,{"disambiguationData":[OSD([sQuery(id+"F19.wireOp",EDGE,"E29.bottom"),sQuery(id+"F19.wireOp",EDGE,"E29.top"),sQuery(id+"F19.wireOp",EDGE,"E29.left"),sQuery(id+"F19.wireOp",EDGE,"E29.right")])]}),"instanceName":"1"}),"instanceName":"1"});
            var Q72;
            Q72=makeQuery(id+"F26.opPattern","COPY",BODY,{"derivedFrom":makeQuery(id+"F25.opPattern","COPY",BODY,{"derivedFrom":makeQuery(id+"F20.opExtrude","SWEPT_BODY",BODY,{"disambiguationData":[OSD([sQuery(id+"F19.wireOp",EDGE,"E29.bottom"),sQuery(id+"F19.wireOp",EDGE,"E29.top"),sQuery(id+"F19.wireOp",EDGE,"E29.left"),sQuery(id+"F19.wireOp",EDGE,"E29.right")])]}),"instanceName":"1"}),"instanceName":"1"});
            var Q73;
            Q73=makeQuery(id+"F26.opPattern","COPY",BODY,{"derivedFrom":makeQuery(id+"F25.opPattern","COPY",BODY,{"derivedFrom":makeQuery(id+"F21.opPattern","COPY",BODY,{"derivedFrom":makeQuery(id+"F20.opExtrude","SWEPT_BODY",BODY,{"disambiguationData":[OSD([sQuery(id+"F19.wireOp",EDGE,"E29.bottom"),sQuery(id+"F19.wireOp",EDGE,"E29.top"),sQuery(id+"F19.wireOp",EDGE,"E29.left"),sQuery(id+"F19.wireOp",EDGE,"E29.right")])]}),"instanceName":"1"}),"instanceName":"1"}),"instanceName":"1"});
            var Q74;
            Q74=makeQuery(id+"F26.opPattern","COPY",BODY,{"derivedFrom":makeQuery(id+"F25.opPattern","COPY",BODY,{"derivedFrom":makeQuery(id+"F23.opPattern","COPY",BODY,{"derivedFrom":makeQuery(id+"F21.opPattern","COPY",BODY,{"derivedFrom":makeQuery(id+"F20.opExtrude","SWEPT_BODY",BODY,{"disambiguationData":[OSD([sQuery(id+"F19.wireOp",EDGE,"E29.bottom"),sQuery(id+"F19.wireOp",EDGE,"E29.top"),sQuery(id+"F19.wireOp",EDGE,"E29.left"),sQuery(id+"F19.wireOp",EDGE,"E29.right")])]}),"instanceName":"1"}),"instanceName":"1"}),"instanceName":"1"}),"instanceName":"1"});
            var Q75;
            Q75=makeQuery(id+"F27.opPattern","COPY",BODY,{"derivedFrom":makeQuery(id+"F26.opPattern","COPY",BODY,{"derivedFrom":makeQuery(id+"F25.opPattern","COPY",BODY,{"derivedFrom":makeQuery(id+"F20.opExtrude","SWEPT_BODY",BODY,{"disambiguationData":[OSD([sQuery(id+"F19.wireOp",EDGE,"E29.bottom"),sQuery(id+"F19.wireOp",EDGE,"E29.top"),sQuery(id+"F19.wireOp",EDGE,"E29.left"),sQuery(id+"F19.wireOp",EDGE,"E29.right")])]}),"instanceName":"1"}),"instanceName":"1"}),"instanceName":"1"});
            var Q76;
            Q76=makeQuery(id+"F27.opPattern","COPY",BODY,{"derivedFrom":makeQuery(id+"F26.opPattern","COPY",BODY,{"derivedFrom":makeQuery(id+"F25.opPattern","COPY",BODY,{"derivedFrom":makeQuery(id+"F21.opPattern","COPY",BODY,{"derivedFrom":makeQuery(id+"F20.opExtrude","SWEPT_BODY",BODY,{"disambiguationData":[OSD([sQuery(id+"F19.wireOp",EDGE,"E29.bottom"),sQuery(id+"F19.wireOp",EDGE,"E29.top"),sQuery(id+"F19.wireOp",EDGE,"E29.left"),sQuery(id+"F19.wireOp",EDGE,"E29.right")])]}),"instanceName":"1"}),"instanceName":"1"}),"instanceName":"1"}),"instanceName":"1"});
            var Q77;
            Q77=makeQuery(id+"F27.opPattern","COPY",BODY,{"derivedFrom":makeQuery(id+"F26.opPattern","COPY",BODY,{"derivedFrom":makeQuery(id+"F25.opPattern","COPY",BODY,{"derivedFrom":makeQuery(id+"F22.opPattern","COPY",BODY,{"derivedFrom":makeQuery(id+"F20.opExtrude","SWEPT_BODY",BODY,{"disambiguationData":[OSD([sQuery(id+"F19.wireOp",EDGE,"E29.bottom"),sQuery(id+"F19.wireOp",EDGE,"E29.top"),sQuery(id+"F19.wireOp",EDGE,"E29.left"),sQuery(id+"F19.wireOp",EDGE,"E29.right")])]}),"instanceName":"1"}),"instanceName":"1"}),"instanceName":"1"}),"instanceName":"1"});
            var Q78;
            Q78=makeQuery(id+"F28.opPattern","COPY",BODY,{"derivedFrom":makeQuery(id+"F27.opPattern","COPY",BODY,{"derivedFrom":makeQuery(id+"F26.opPattern","COPY",BODY,{"derivedFrom":makeQuery(id+"F25.opPattern","COPY",BODY,{"derivedFrom":makeQuery(id+"F20.opExtrude","SWEPT_BODY",BODY,{"disambiguationData":[OSD([sQuery(id+"F19.wireOp",EDGE,"E29.bottom"),sQuery(id+"F19.wireOp",EDGE,"E29.top"),sQuery(id+"F19.wireOp",EDGE,"E29.left"),sQuery(id+"F19.wireOp",EDGE,"E29.right")])]}),"instanceName":"1"}),"instanceName":"1"}),"instanceName":"1"}),"instanceName":"1"});
            var Q79;
            Q79=makeQuery(id+"F28.opPattern","COPY",BODY,{"derivedFrom":makeQuery(id+"F27.opPattern","COPY",BODY,{"derivedFrom":makeQuery(id+"F26.opPattern","COPY",BODY,{"derivedFrom":makeQuery(id+"F25.opPattern","COPY",BODY,{"derivedFrom":makeQuery(id+"F21.opPattern","COPY",BODY,{"derivedFrom":makeQuery(id+"F20.opExtrude","SWEPT_BODY",BODY,{"disambiguationData":[OSD([sQuery(id+"F19.wireOp",EDGE,"E29.bottom"),sQuery(id+"F19.wireOp",EDGE,"E29.top"),sQuery(id+"F19.wireOp",EDGE,"E29.left"),sQuery(id+"F19.wireOp",EDGE,"E29.right")])]}),"instanceName":"1"}),"instanceName":"1"}),"instanceName":"1"}),"instanceName":"1"}),"instanceName":"1"});
            var Q80;
            Q80=makeQuery(id+"F28.opPattern","COPY",BODY,{"derivedFrom":makeQuery(id+"F27.opPattern","COPY",BODY,{"derivedFrom":makeQuery(id+"F26.opPattern","COPY",BODY,{"derivedFrom":makeQuery(id+"F25.opPattern","COPY",BODY,{"derivedFrom":makeQuery(id+"F23.opPattern","COPY",BODY,{"derivedFrom":makeQuery(id+"F21.opPattern","COPY",BODY,{"derivedFrom":makeQuery(id+"F20.opExtrude","SWEPT_BODY",BODY,{"disambiguationData":[OSD([sQuery(id+"F19.wireOp",EDGE,"E29.bottom"),sQuery(id+"F19.wireOp",EDGE,"E29.top"),sQuery(id+"F19.wireOp",EDGE,"E29.left"),sQuery(id+"F19.wireOp",EDGE,"E29.right")])]}),"instanceName":"1"}),"instanceName":"1"}),"instanceName":"1"}),"instanceName":"1"}),"instanceName":"1"}),"instanceName":"1"});
            var Q81;
            Q81=makeQuery(id+"F28.opPattern","COPY",BODY,{"derivedFrom":makeQuery(id+"F27.opPattern","COPY",BODY,{"derivedFrom":makeQuery(id+"F26.opPattern","COPY",BODY,{"derivedFrom":makeQuery(id+"F25.opPattern","COPY",BODY,{"derivedFrom":makeQuery(id+"F24.opPattern","COPY",BODY,{"derivedFrom":makeQuery(id+"F23.opPattern","COPY",BODY,{"derivedFrom":makeQuery(id+"F21.opPattern","COPY",BODY,{"derivedFrom":makeQuery(id+"F20.opExtrude","SWEPT_BODY",BODY,{"disambiguationData":[OSD([sQuery(id+"F19.wireOp",EDGE,"E29.bottom"),sQuery(id+"F19.wireOp",EDGE,"E29.top"),sQuery(id+"F19.wireOp",EDGE,"E29.left"),sQuery(id+"F19.wireOp",EDGE,"E29.right")])]}),"instanceName":"1"}),"instanceName":"1"}),"instanceName":"1"}),"instanceName":"1"}),"instanceName":"1"}),"instanceName":"1"}),"instanceName":"1"});
            var Q82;
            Q82=makeQuery(id+"F29.opPattern","COPY",BODY,{"derivedFrom":makeQuery(id+"F28.opPattern","COPY",BODY,{"derivedFrom":makeQuery(id+"F27.opPattern","COPY",BODY,{"derivedFrom":makeQuery(id+"F26.opPattern","COPY",BODY,{"derivedFrom":makeQuery(id+"F25.opPattern","COPY",BODY,{"derivedFrom":makeQuery(id+"F20.opExtrude","SWEPT_BODY",BODY,{"disambiguationData":[OSD([sQuery(id+"F19.wireOp",EDGE,"E29.bottom"),sQuery(id+"F19.wireOp",EDGE,"E29.top"),sQuery(id+"F19.wireOp",EDGE,"E29.left"),sQuery(id+"F19.wireOp",EDGE,"E29.right")])]}),"instanceName":"1"}),"instanceName":"1"}),"instanceName":"1"}),"instanceName":"1"}),"instanceName":"1"});
            var Q83;
            Q83=makeQuery(id+"F29.opPattern","COPY",BODY,{"derivedFrom":makeQuery(id+"F28.opPattern","COPY",BODY,{"derivedFrom":makeQuery(id+"F27.opPattern","COPY",BODY,{"derivedFrom":makeQuery(id+"F26.opPattern","COPY",BODY,{"derivedFrom":makeQuery(id+"F25.opPattern","COPY",BODY,{"derivedFrom":makeQuery(id+"F23.opPattern","COPY",BODY,{"derivedFrom":makeQuery(id+"F21.opPattern","COPY",BODY,{"derivedFrom":makeQuery(id+"F20.opExtrude","SWEPT_BODY",BODY,{"disambiguationData":[OSD([sQuery(id+"F19.wireOp",EDGE,"E29.bottom"),sQuery(id+"F19.wireOp",EDGE,"E29.top"),sQuery(id+"F19.wireOp",EDGE,"E29.left"),sQuery(id+"F19.wireOp",EDGE,"E29.right")])]}),"instanceName":"1"}),"instanceName":"1"}),"instanceName":"1"}),"instanceName":"1"}),"instanceName":"1"}),"instanceName":"1"}),"instanceName":"1"});
            var Q84;
            Q84=makeQuery(id+"F1.opExtrude","SWEPT_EDGE",EDGE,{"disambiguationData":[OSD([sQuery(id+"F0.wireOp",EDGE,"E0.left"),sQuery(id+"F0.wireOp",EDGE,"E5.filletArc")])]});
            transform(context, id + "F48", {"entities" : qUnion([Q0, Q1, Q2, Q3, Q4, Q5, Q6, Q7, Q8, Q9, Q10, Q11, Q12, Q13, Q14, Q15, Q16, Q17, Q18, Q19, Q20, Q21, Q22, Q23, Q24, Q25, Q26, Q27, Q28, Q29, Q30, Q31, Q32, Q33, Q34, Q35, Q36, Q37, Q38, Q39, Q40, Q41, Q42, Q43, Q44, Q45, Q46, Q47, Q48, Q49, Q50, Q51, Q52, Q53, Q54, Q55, Q56, Q57, Q58, Q59, Q60, Q61, Q62, Q63, Q64, Q65, Q66, Q67, Q68, Q69, Q70, Q71, Q72, Q73, Q74, Q75, Q76, Q77, Q78, Q79, Q80, Q81, Q82, Q83]), "transformType" : TransformType.ROTATION, "transformAxis" : qUnion([Q84]), "angle" : 270 * degree, "makeCopy" : false});
        }
        {
            var Q0;
            Q0=makeQuery(id+"F43.opPattern","COPY",FACE,{"derivedFrom":makeQuery(id+"F42.opExtrude","SWEPT_FACE",FACE,{"disambiguationData":[OSD([sQuery(id+"F41.wireOp",EDGE,"E34.top")])]}),"instanceName":"1"});
            var sketch = newSketch(context, id + "F49", { "sketchPlane" : qUnion([Q0])});
            skLineSegment(sketch, "E35.0", {"start": v(405.5, 1875) * mm, "end": v(405.5, 25) * mm});
            skLineSegment(sketch, "E36.0", {"start": v(15.5, 1875) * mm, "end": v(405.5, 1875) * mm});
            skLineSegment(sketch, "E37.0", {"start": v(15.5, 1875) * mm, "end": v(15.5, 25) * mm});
            skLineSegment(sketch, "E38.0", {"start": v(15.5, 25) * mm, "end": v(405.5, 25) * mm});
            skPoint(sketch, "E39.orphan", {"position": v(15.5, 0) * mm});
            skPoint(sketch, "E40.orphan", {"position": v(405.5, 0) * mm});
            skPoint(sketch, "E41.orphan", {"position": v(405.5, 1900) * mm});
            skPoint(sketch, "E42.orphan", {"position": v(15.5, 1900) * mm});
            skSolve(sketch);
        }
        {
            var Q0;
            {var subQ0=sQuery(id+"F49.wireOp",EDGE,"E36.0");Q0=makeQuery(id+"F49.imprint","IMPRINT",FACE,{"disambiguationData":[TD([[makeQuery(id+"F49.imprint","IMPRINT",EDGE,{"derivedFrom":subQ0}),-1.0]])]});}
            var Q1;
            {var subQ0=sQuery(id+"F49.wireOp",EDGE,"E35.0");var subQ1=sQuery(id+"F41.wireOp",EDGE,"E34.top");var subQ2=makeQuery(id+"F43.opPattern","COPY",EDGE,{"derivedFrom":makeQuery(id+"F42.opExtrude","CAP_EDGE",EDGE,{"disambiguationData":[OSD([subQ1])],"isStart":false}),"instanceName":"1"});var subQ3=makeQuery(id+"F49.imprint","INTERSECT",VERTEX,{"derivedFrom":[subQ2,subQ0]});Q1=makeQuery(id+"F49.imprint","IMPRINT",FACE,{"disambiguationData":[TD([[makeQuery(id+"F49.imprint","IMPRINT",EDGE,{"disambiguationData":[TD([[subQ3,-1.0]])],"derivedFrom":subQ0}),-1.0]])]});}
            var Q2;
            {var subQ0=sQuery(id+"F49.wireOp",EDGE,"E38.0");Q2=makeQuery(id+"F49.imprint","IMPRINT",FACE,{"disambiguationData":[TD([[makeQuery(id+"F49.imprint","IMPRINT",EDGE,{"derivedFrom":subQ0}),1.0]])]});}
            extrude(context, id + "F50", {"entities" : qUnion([Q0, Q1, Q2]), "depth" : 10 * mm});
        }
        {
            var Q0;
            Q0=makeQuery(id+"F43.opPattern","COPY",FACE,{"derivedFrom":makeQuery(id+"F42.opExtrude","SWEPT_FACE",FACE,{"disambiguationData":[OSD([sQuery(id+"F41.wireOp",EDGE,"E34.bottom")])]}),"instanceName":"1"});
            var sketch = newSketch(context, id + "F51", { "sketchPlane" : qUnion([Q0])});
            skLineSegment(sketch, "E43.0", {"start": v(-15.5, 1875) * mm, "end": v(-15.5, 25) * mm});
            skLineSegment(sketch, "E44.0", {"start": v(-15.5, 1875) * mm, "end": v(-405.5, 1875) * mm});
            skLineSegment(sketch, "E45.0", {"start": v(-405.5, 1875) * mm, "end": v(-405.5, 25) * mm});
            skLineSegment(sketch, "E46.0", {"start": v(-15.5, 25) * mm, "end": v(-405.5, 25) * mm});
            skPoint(sketch, "E47.orphan", {"position": v(-405.5, 0) * mm});
            skPoint(sketch, "E48.orphan", {"position": v(-15.5, 0) * mm});
            skPoint(sketch, "E49.orphan", {"position": v(-15.5, 1900) * mm});
            skPoint(sketch, "E50.orphan", {"position": v(-405.5, 1900) * mm});
            skSolve(sketch);
        }
        {
            var Q0;
            {var subQ0=sQuery(id+"F51.wireOp",EDGE,"E44.0");Q0=makeQuery(id+"F51.imprint","IMPRINT",FACE,{"disambiguationData":[TD([[makeQuery(id+"F51.imprint","IMPRINT",EDGE,{"derivedFrom":subQ0}),1.0]])]});}
            var Q1;
            {var subQ0=sQuery(id+"F51.wireOp",EDGE,"E43.0");var subQ1=sQuery(id+"F41.wireOp",EDGE,"E34.bottom");var subQ2=makeQuery(id+"F43.opPattern","COPY",EDGE,{"derivedFrom":makeQuery(id+"F42.opExtrude","CAP_EDGE",EDGE,{"disambiguationData":[OSD([subQ1])],"isStart":false}),"instanceName":"1"});var subQ3=makeQuery(id+"F51.imprint","INTERSECT",VERTEX,{"derivedFrom":[subQ2,subQ0]});Q1=makeQuery(id+"F51.imprint","IMPRINT",FACE,{"disambiguationData":[TD([[makeQuery(id+"F51.imprint","IMPRINT",EDGE,{"disambiguationData":[TD([[subQ3,-1.0]])],"derivedFrom":subQ0}),-1.0]])]});}
            var Q2;
            {var subQ0=sQuery(id+"F51.wireOp",EDGE,"E46.0");Q2=makeQuery(id+"F51.imprint","IMPRINT",FACE,{"disambiguationData":[TD([[makeQuery(id+"F51.imprint","IMPRINT",EDGE,{"derivedFrom":subQ0}),-1.0]])]});}
            extrude(context, id + "F52", {"entities" : qUnion([Q0, Q1, Q2]), "depth" : 10 * mm});
        }
        {
            var Q0;
            Q0=makeQuery(id+"F31.opExtrude","SWEPT_FACE",FACE,{"disambiguationData":[OSD([sQuery(id+"F30.wireOp",EDGE,"E30.top")])]});
            cPlane(context, id + "F53", {"entities" : qUnion([Q0]), "cplaneType" : CPlaneType.OFFSET, "offset" : 7.5 * mm, "oppositeDirection" : true, "width" : 150 * mm, "height" : 150 * mm});
        }
        {
            var Q0;
            Q0=qCreatedBy(id+"F53.planeOp",FACE);
            var sketch = newSketch(context, id + "F54", { "sketchPlane" : qUnion([Q0])});
            skLineSegment(sketch, "E51.0", {"start": v(-6.5, 1470) * mm, "end": v(427.5, 1470) * mm});
            skLineSegment(sketch, "E52.0", {"start": v(-6.5, 1875) * mm, "end": v(-6.5, 1470) * mm});
            skLineSegment(sketch, "E53.0", {"start": v(427.5, 1875) * mm, "end": v(427.5, 1470) * mm});
            skLineSegment(sketch, "E54.0", {"start": v(15.5, 1890) * mm, "end": v(405.5, 1890) * mm});
            skLineSegment(sketch, "E55.0", {"start": v(405.5, 1875) * mm, "end": v(405.5, 1890) * mm});
            skLineSegment(sketch, "E56.0", {"start": v(427.5, 1875) * mm, "end": v(405.5, 1875) * mm});
            skLineSegment(sketch, "E57.0", {"start": v(-6.5, 1875) * mm, "end": v(15.5, 1875) * mm});
            skLineSegment(sketch, "E58.0", {"start": v(15.5, 1875) * mm, "end": v(15.5, 1890) * mm});
            skPoint(sketch, "E59.orphan", {"position": v(405.5, 1876) * mm});
            skPoint(sketch, "E60.orphan", {"position": v(15.5, 1876) * mm});
            skPoint(sketch, "E61.orphan", {"position": v(-6.5, 1890) * mm});
            skPoint(sketch, "E62.orphan", {"position": v(-9.5, 1875) * mm});
            skPoint(sketch, "E63.orphan", {"position": v(427.5, 1890) * mm});
            skPoint(sketch, "E64.orphan", {"position": v(430.5, 1875) * mm});
            skSolve(sketch);
        }
        {
            var Q0;
            Q0=makeQuery(id+"F54.imprint","IMPRINT",FACE,{"disambiguationData":[TD([[makeQuery(id+"F54.imprint","IMPRINT",EDGE,{"derivedFrom":sQuery(id+"F54.wireOp",EDGE,"E51.0")}),1.0]])]});
            extrude(context, id + "F55", {"entities" : qUnion([Q0]), "oppositeDirection" : true, "depth" : 10 * mm});
        }
        {
            var Q0;
            Q0=makeQuery(id+"F33.opExtrude","SWEPT_FACE",FACE,{"disambiguationData":[OSD([sQuery(id+"F32.wireOp",EDGE,"E31.top")])]});
            cPlane(context, id + "F56", {"entities" : qUnion([Q0]), "cplaneType" : CPlaneType.OFFSET, "offset" : 7.5 * mm, "oppositeDirection" : true, "width" : 150 * mm, "height" : 150 * mm});
        }
        {
            var Q0;
            Q0=qCreatedBy(id+"F56.planeOp",FACE);
            var sketch = newSketch(context, id + "F57", { "sketchPlane" : qUnion([Q0])});
            skLineSegment(sketch, "E65.0", {"start": v(-6.5, 1175) * mm, "end": v(427.5, 1175) * mm});
            skLineSegment(sketch, "E66.0", {"start": v(427.5, 1445) * mm, "end": v(427.5, 1175) * mm});
            skLineSegment(sketch, "E67.0", {"start": v(-6.5, 1445) * mm, "end": v(-6.5, 1175) * mm});
            skLineSegment(sketch, "E68.0", {"start": v(15.5, 1460) * mm, "end": v(405.5, 1460) * mm});
            skLineSegment(sketch, "E69.0", {"start": v(427.5, 1445) * mm, "end": v(405.5, 1445) * mm});
            skLineSegment(sketch, "E70.0", {"start": v(405.5, 1445) * mm, "end": v(405.5, 1460) * mm});
            skLineSegment(sketch, "E71.0", {"start": v(-6.5, 1445) * mm, "end": v(15.5, 1445) * mm});
            skLineSegment(sketch, "E72.0", {"start": v(15.5, 1445) * mm, "end": v(15.5, 1460) * mm});
            skPoint(sketch, "E73.orphan", {"position": v(405.5, 1446) * mm});
            skPoint(sketch, "E74.orphan", {"position": v(15.5, 1446) * mm});
            skPoint(sketch, "E75.orphan", {"position": v(-6.5, 1460) * mm});
            skPoint(sketch, "E76.orphan", {"position": v(-9.5, 1445) * mm});
            skPoint(sketch, "E77.orphan", {"position": v(430.5, 1445) * mm});
            skPoint(sketch, "E78.orphan", {"position": v(427.5, 1460) * mm});
            skSolve(sketch);
        }
        {
            var Q0;
            Q0=makeQuery(id+"F57.imprint","IMPRINT",FACE,{"disambiguationData":[TD([[makeQuery(id+"F57.imprint","IMPRINT",EDGE,{"derivedFrom":sQuery(id+"F57.wireOp",EDGE,"E65.0")}),1.0]])]});
            extrude(context, id + "F58", {"entities" : qUnion([Q0]), "oppositeDirection" : true, "depth" : 10 * mm});
        }
        {
            var Q0;
            Q0=makeQuery(id+"F35.opExtrude","SWEPT_FACE",FACE,{"disambiguationData":[OSD([sQuery(id+"F34.wireOp",EDGE,"E32.top")])]});
            cPlane(context, id + "F59", {"entities" : qUnion([Q0]), "cplaneType" : CPlaneType.OFFSET, "offset" : 7.5 * mm, "oppositeDirection" : true, "width" : 150 * mm, "height" : 150 * mm});
        }
        {
            var Q0;
            Q0=qCreatedBy(id+"F59.planeOp",FACE);
            var sketch = newSketch(context, id + "F60", { "sketchPlane" : qUnion([Q0])});
            skLineSegment(sketch, "E79.0", {"start": v(-6.5, 880) * mm, "end": v(427.5, 880) * mm});
            skLineSegment(sketch, "E80.0", {"start": v(-6.5, 1150) * mm, "end": v(-6.5, 880) * mm});
            skLineSegment(sketch, "E81.0", {"start": v(427.5, 1150) * mm, "end": v(427.5, 880) * mm});
            skLineSegment(sketch, "E82.0", {"start": v(427.5, 1150) * mm, "end": v(405.5, 1150) * mm});
            skLineSegment(sketch, "E83.0", {"start": v(405.5, 1150) * mm, "end": v(405.5, 1165) * mm});
            skLineSegment(sketch, "E84.0", {"start": v(-6.5, 1150) * mm, "end": v(15.5, 1150) * mm});
            skLineSegment(sketch, "E85.0", {"start": v(15.5, 1150) * mm, "end": v(15.5, 1165) * mm});
            skLineSegment(sketch, "E86.0", {"start": v(15.5, 1165) * mm, "end": v(405.5, 1165) * mm});
            skPoint(sketch, "E87.orphan", {"position": v(405.5, 1151) * mm});
            skPoint(sketch, "E88.orphan", {"position": v(15.5, 1151) * mm});
            skPoint(sketch, "E89.orphan", {"position": v(-6.5, 1165) * mm});
            skPoint(sketch, "E90.orphan", {"position": v(-9.5, 1150) * mm});
            skPoint(sketch, "E91.orphan", {"position": v(427.5, 1165) * mm});
            skPoint(sketch, "E92.orphan", {"position": v(430.5, 1150) * mm});
            skSolve(sketch);
        }
        {
            var Q0;
            Q0=makeQuery(id+"F60.imprint","IMPRINT",FACE,{"disambiguationData":[TD([[makeQuery(id+"F60.imprint","IMPRINT",EDGE,{"derivedFrom":sQuery(id+"F60.wireOp",EDGE,"E79.0")}),1.0]])]});
            extrude(context, id + "F61", {"entities" : qUnion([Q0]), "oppositeDirection" : true, "depth" : 10 * mm});
        }
        {
            var Q0;
            Q0=makeQuery(id+"F37.opExtrude","SWEPT_FACE",FACE,{"disambiguationData":[OSD([sQuery(id+"F36.wireOp",EDGE,"E33.top")])]});
            cPlane(context, id + "F62", {"entities" : qUnion([Q0]), "cplaneType" : CPlaneType.OFFSET, "offset" : 7.5 * mm, "oppositeDirection" : true, "width" : 150 * mm, "height" : 150 * mm});
        }
        {
            var Q0;
            Q0=qCreatedBy(id+"F62.planeOp",FACE);
            var sketch = newSketch(context, id + "F63", { "sketchPlane" : qUnion([Q0])});
            skLineSegment(sketch, "E93.0", {"start": v(-6.5, 25) * mm, "end": v(427.5, 25) * mm});
            skLineSegment(sketch, "E94.0", {"start": v(-6.5, 515) * mm, "end": v(-6.5, 25) * mm});
            skLineSegment(sketch, "E95.0", {"start": v(427.5, 515) * mm, "end": v(427.5, 25) * mm});
            skLineSegment(sketch, "E96.0", {"start": v(15.5, 530) * mm, "end": v(405.5, 530) * mm});
            skLineSegment(sketch, "E97.0", {"start": v(427.5, 515) * mm, "end": v(405.5, 515) * mm});
            skLineSegment(sketch, "E98.0", {"start": v(405.5, 515) * mm, "end": v(405.5, 530) * mm});
            skLineSegment(sketch, "E99.0", {"start": v(-6.5, 515) * mm, "end": v(15.5, 515) * mm});
            skLineSegment(sketch, "E100.0", {"start": v(15.5, 515) * mm, "end": v(15.5, 530) * mm});
            skPoint(sketch, "E101.orphan", {"position": v(405.5, 516) * mm});
            skPoint(sketch, "E102.orphan", {"position": v(15.5, 516) * mm});
            skPoint(sketch, "E103.orphan", {"position": v(-6.5, 530) * mm});
            skPoint(sketch, "E104.orphan", {"position": v(-9.5, 515) * mm});
            skPoint(sketch, "E105.orphan", {"position": v(430.5, 515) * mm});
            skPoint(sketch, "E106.orphan", {"position": v(427.5, 530) * mm});
            skSolve(sketch);
        }
        {
            var Q0;
            Q0=makeQuery(id+"F63.imprint","IMPRINT",FACE,{"disambiguationData":[TD([[makeQuery(id+"F63.imprint","IMPRINT",EDGE,{"derivedFrom":sQuery(id+"F63.wireOp",EDGE,"E93.0")}),1.0]])]});
            extrude(context, id + "F64", {"entities" : qUnion([Q0]), "oppositeDirection" : true, "depth" : 10 * mm});
        }
        {
            var Q0;
            Q0=makeQuery(id+"F64.opExtrude","SWEPT_BODY",BODY,{"disambiguationData":[OSD([sQuery(id+"F63.wireOp",EDGE,"E93.0"),sQuery(id+"F63.wireOp",EDGE,"E94.0"),sQuery(id+"F63.wireOp",EDGE,"E95.0"),sQuery(id+"F63.wireOp",EDGE,"E96.0"),sQuery(id+"F63.wireOp",EDGE,"E97.0"),sQuery(id+"F63.wireOp",EDGE,"E98.0"),sQuery(id+"F63.wireOp",EDGE,"E99.0"),sQuery(id+"F63.wireOp",EDGE,"E100.0")])]});
            transform(context, id + "F65", {"entities" : qUnion([Q0]), "transformType" : TransformType.TRANSLATION_3D, "dx" : 362 * mm, "dy" : 0 * mm, "dz" : 0 * mm, "makeCopy" : true});
        }
        {
            var Q0;
            Q0=makeQuery(id+"F3.opPattern","COPY",FACE,{"derivedFrom":makeQuery(id+"F1.opExtrude","SWEPT_FACE",FACE,{"disambiguationData":[OSD([sQuery(id+"F0.wireOp",EDGE,"E0.bottom")])]}),"instanceName":"1"});
            cPlane(context, id + "F66", {"entities" : qUnion([Q0]), "cplaneType" : CPlaneType.OFFSET, "offset" : 12.5 * mm, "oppositeDirection" : true, "width" : 150 * mm, "height" : 150 * mm});
        }
        {
            var Q0;
            Q0=qCreatedBy(id+"F66.planeOp",FACE);
            var sketch = newSketch(context, id + "F67", { "sketchPlane" : qUnion([Q0])});
            skLineSegment(sketch, "E107", {"start": v(9.5, 1889) * mm, "end": v(15.5, 1889) * mm});
            skLineSegment(sketch, "E108", {"start": v(19.5, 1885) * mm, "end": v(19.5, 1879) * mm});
            skLineSegment(sketch, "E109", {"start": v(19.5, 1879) * mm, "end": v(17.5, 1879) * mm});
            skLineSegment(sketch, "E110", {"start": v(17.5, 1879) * mm, "end": v(17.5, 1885) * mm});
            skLineSegment(sketch, "E111", {"start": v(15.5, 1887) * mm, "end": v(9.5, 1887) * mm});
            skLineSegment(sketch, "E112", {"start": v(9.5, 1887) * mm, "end": v(9.5, 1889) * mm});
            skPoint(sketch, "E113.visualSharp", {"position": v(17.5, 1887) * mm});
            skArc(sketch, "E113.filletArc", {"start": v(17.5, 1885) * mm, "mid": v(16.91, 1886.41) * mm, "end": v(15.5, 1887) * mm});
            skPoint(sketch, "E114.visualSharp", {"position": v(19.5, 1889) * mm});
            skArc(sketch, "E114.filletArc", {"start": v(19.5, 1885) * mm, "mid": v(18.33, 1887.83) * mm, "end": v(15.5, 1889) * mm});
            skSolve(sketch);
        }
        {
            var Q0;
            Q0=makeQuery(id+"F67.imprint","IMPRINT",FACE,{"disambiguationData":[TD([[makeQuery(id+"F67.imprint","IMPRINT",EDGE,{"derivedFrom":sQuery(id+"F67.wireOp",EDGE,"E107")}),-1.0]])]});
            extrude(context, id + "F68", {"entities" : qUnion([Q0]), "oppositeDirection" : true, "depth" : 660 * mm});
        }
        {
            var Q0;
            Q0=makeQuery(id+"F68.opExtrude","SWEPT_BODY",BODY,{"disambiguationData":[OSD([sQuery(id+"F67.wireOp",EDGE,"E107"),sQuery(id+"F67.wireOp",EDGE,"E108"),sQuery(id+"F67.wireOp",EDGE,"E109"),sQuery(id+"F67.wireOp",EDGE,"E110"),sQuery(id+"F67.wireOp",EDGE,"E111"),sQuery(id+"F67.wireOp",EDGE,"E112"),sQuery(id+"F67.wireOp",EDGE,"E113.filletArc"),sQuery(id+"F67.wireOp",EDGE,"E114.filletArc")])]});
            var Q1;
            Q1=makeQuery(id+"F68.opExtrude","CAP_EDGE",EDGE,{"disambiguationData":[OSD([sQuery(id+"F67.wireOp",EDGE,"E111")])],"isStart":true});
            transform(context, id + "F69", {"entities" : qUnion([Q0]), "transformType" : TransformType.ROTATION, "transformAxis" : qUnion([Q1]), "angle" : 180 * degree, "makeCopy" : true});
        }
        {
            var Q0;
            Q0=makeQuery(id+"F69.opPattern","COPY",BODY,{"derivedFrom":makeQuery(id+"F68.opExtrude","SWEPT_BODY",BODY,{"disambiguationData":[OSD([sQuery(id+"F67.wireOp",EDGE,"E107"),sQuery(id+"F67.wireOp",EDGE,"E108"),sQuery(id+"F67.wireOp",EDGE,"E109"),sQuery(id+"F67.wireOp",EDGE,"E110"),sQuery(id+"F67.wireOp",EDGE,"E111"),sQuery(id+"F67.wireOp",EDGE,"E112"),sQuery(id+"F67.wireOp",EDGE,"E113.filletArc"),sQuery(id+"F67.wireOp",EDGE,"E114.filletArc")])]}),"instanceName":"1"});
            transform(context, id + "F70", {"entities" : qUnion([Q0]), "transformType" : TransformType.TRANSLATION_3D, "dx" : 670 * mm, "dy" : 0 * mm, "dz" : 0 * mm, "makeCopy" : false});
        }
        {
            var Q0;
            Q0=makeQuery(id+"F69.opPattern","COPY",BODY,{"derivedFrom":makeQuery(id+"F68.opExtrude","SWEPT_BODY",BODY,{"disambiguationData":[OSD([sQuery(id+"F67.wireOp",EDGE,"E107"),sQuery(id+"F67.wireOp",EDGE,"E108"),sQuery(id+"F67.wireOp",EDGE,"E109"),sQuery(id+"F67.wireOp",EDGE,"E110"),sQuery(id+"F67.wireOp",EDGE,"E111"),sQuery(id+"F67.wireOp",EDGE,"E112"),sQuery(id+"F67.wireOp",EDGE,"E113.filletArc"),sQuery(id+"F67.wireOp",EDGE,"E114.filletArc")])]}),"instanceName":"1"});
            transform(context, id + "F71", {"entities" : qUnion([Q0]), "transformType" : TransformType.TRANSLATION_3D, "dx" : 0 * mm, "dy" : 0 * mm, "dz" : -405 * mm, "makeCopy" : false});
        }
        {
            var Q0;
            Q0=makeQuery(id+"F69.opPattern","COPY",BODY,{"derivedFrom":makeQuery(id+"F68.opExtrude","SWEPT_BODY",BODY,{"disambiguationData":[OSD([sQuery(id+"F67.wireOp",EDGE,"E107"),sQuery(id+"F67.wireOp",EDGE,"E108"),sQuery(id+"F67.wireOp",EDGE,"E109"),sQuery(id+"F67.wireOp",EDGE,"E110"),sQuery(id+"F67.wireOp",EDGE,"E111"),sQuery(id+"F67.wireOp",EDGE,"E112"),sQuery(id+"F67.wireOp",EDGE,"E113.filletArc"),sQuery(id+"F67.wireOp",EDGE,"E114.filletArc")])]}),"instanceName":"1"});
            transform(context, id + "F72", {"entities" : qUnion([Q0]), "transformType" : TransformType.TRANSLATION_3D, "dx" : 0 * mm, "dy" : 0 * mm, "dz" : -24 * mm, "makeCopy" : false});
        }
        {
            var Q0;
            Q0=qCreatedBy(id+"F66.planeOp",FACE);
            var sketch = newSketch(context, id + "F73", { "sketchPlane" : qUnion([Q0])});
            skLineSegment(sketch, "E115", {"start": v(9.5, 1164) * mm, "end": v(15.5, 1164) * mm});
            skLineSegment(sketch, "E116", {"start": v(19.5, 1160) * mm, "end": v(19.5, 1154) * mm});
            skLineSegment(sketch, "E117", {"start": v(19.5, 1154) * mm, "end": v(17.5, 1154) * mm});
            skLineSegment(sketch, "E118", {"start": v(17.5, 1154) * mm, "end": v(17.5, 1160) * mm});
            skLineSegment(sketch, "E119", {"start": v(15.5, 1162) * mm, "end": v(9.5, 1162) * mm});
            skLineSegment(sketch, "E120", {"start": v(9.5, 1162) * mm, "end": v(9.5, 1164) * mm});
            skPoint(sketch, "E121.visualSharp", {"position": v(17.5, 1162) * mm});
            skArc(sketch, "E121.filletArc", {"start": v(17.5, 1160) * mm, "mid": v(16.91, 1161.41) * mm, "end": v(15.5, 1162) * mm});
            skPoint(sketch, "E122.visualSharp", {"position": v(19.5, 1164) * mm});
            skArc(sketch, "E122.filletArc", {"start": v(19.5, 1160) * mm, "mid": v(18.33, 1162.83) * mm, "end": v(15.5, 1164) * mm});
            skSolve(sketch);
        }
        {
            var Q0;
            Q0=makeQuery(id+"F73.imprint","IMPRINT",FACE,{"disambiguationData":[TD([[makeQuery(id+"F73.imprint","IMPRINT",EDGE,{"derivedFrom":sQuery(id+"F73.wireOp",EDGE,"E115")}),-1.0]])]});
            extrude(context, id + "F74", {"entities" : qUnion([Q0]), "oppositeDirection" : true, "depth" : 980 * mm});
        }
        {
            var Q0;
            Q0=makeQuery(id+"F74.opExtrude","SWEPT_BODY",BODY,{"disambiguationData":[OSD([sQuery(id+"F73.wireOp",EDGE,"E115"),sQuery(id+"F73.wireOp",EDGE,"E116"),sQuery(id+"F73.wireOp",EDGE,"E117"),sQuery(id+"F73.wireOp",EDGE,"E118"),sQuery(id+"F73.wireOp",EDGE,"E119"),sQuery(id+"F73.wireOp",EDGE,"E120"),sQuery(id+"F73.wireOp",EDGE,"E121.filletArc"),sQuery(id+"F73.wireOp",EDGE,"E122.filletArc")])]});
            var Q1;
            Q1=makeQuery(id+"F74.opExtrude","SWEPT_FACE",FACE,{"disambiguationData":[OSD([sQuery(id+"F73.wireOp",EDGE,"E117")])]});
            mirror(context, id + "F75", {"entities" : qUnion([Q0]), "mirrorPlane" : qUnion([Q1])});
        }
        {
            var Q0;
            Q0=makeQuery(id+"F75.opPattern","COPY",BODY,{"derivedFrom":makeQuery(id+"F74.opExtrude","SWEPT_BODY",BODY,{"disambiguationData":[OSD([sQuery(id+"F73.wireOp",EDGE,"E115"),sQuery(id+"F73.wireOp",EDGE,"E116"),sQuery(id+"F73.wireOp",EDGE,"E117"),sQuery(id+"F73.wireOp",EDGE,"E118"),sQuery(id+"F73.wireOp",EDGE,"E119"),sQuery(id+"F73.wireOp",EDGE,"E120"),sQuery(id+"F73.wireOp",EDGE,"E121.filletArc"),sQuery(id+"F73.wireOp",EDGE,"E122.filletArc")])]}),"instanceName":"1"});
            transform(context, id + "F76", {"entities" : qUnion([Q0]), "transformType" : TransformType.TRANSLATION_3D, "dx" : 0 * mm, "dy" : 0 * mm, "dz" : -278 * mm, "makeCopy" : false});
        }
        {
            var Q0;
            Q0=makeQuery(id+"F1.opExtrude","SWEPT_FACE",FACE,{"disambiguationData":[OSD([sQuery(id+"F0.wireOp",EDGE,"E0.top")])]});
            cPlane(context, id + "F77", {"entities" : qUnion([Q0]), "cplaneType" : CPlaneType.OFFSET, "offset" : 12.5 * mm, "oppositeDirection" : true, "width" : 150 * mm, "height" : 150 * mm});
        }
        {
            var Q0;
            Q0=qCreatedBy(id+"F77.planeOp",FACE);
            var sketch = newSketch(context, id + "F78", { "sketchPlane" : qUnion([Q0])});
            skLineSegment(sketch, "E123", {"start": v(-9.5, 529) * mm, "end": v(-15.5, 529) * mm});
            skLineSegment(sketch, "E124", {"start": v(-19.5, 525) * mm, "end": v(-19.5, 519) * mm});
            skLineSegment(sketch, "E125", {"start": v(-19.5, 519) * mm, "end": v(-17.5, 519) * mm});
            skLineSegment(sketch, "E126", {"start": v(-17.5, 519) * mm, "end": v(-17.5, 525) * mm});
            skLineSegment(sketch, "E127", {"start": v(-15.5, 527) * mm, "end": v(-9.5, 527) * mm});
            skLineSegment(sketch, "E128", {"start": v(-9.5, 527) * mm, "end": v(-9.5, 529) * mm});
            skPoint(sketch, "E129.visualSharp", {"position": v(-17.5, 527) * mm});
            skArc(sketch, "E129.filletArc", {"start": v(-15.5, 527) * mm, "mid": v(-16.91, 526.41) * mm, "end": v(-17.5, 525) * mm});
            skPoint(sketch, "E130.visualSharp", {"position": v(-19.5, 529) * mm});
            skArc(sketch, "E130.filletArc", {"start": v(-15.5, 529) * mm, "mid": v(-18.33, 527.83) * mm, "end": v(-19.5, 525) * mm});
            skSolve(sketch);
        }
        {
            var Q0;
            Q0=makeQuery(id+"F78.imprint","IMPRINT",FACE,{"disambiguationData":[TD([[makeQuery(id+"F78.imprint","IMPRINT",EDGE,{"derivedFrom":sQuery(id+"F78.wireOp",EDGE,"E123")}),1.0]])]});
            extrude(context, id + "F79", {"entities" : qUnion([Q0]), "oppositeDirection" : true, "depth" : 708 * mm});
        }
        {
            var Q0;
            Q0=makeQuery(id+"F79.opExtrude","SWEPT_BODY",BODY,{"disambiguationData":[OSD([sQuery(id+"F78.wireOp",EDGE,"E123"),sQuery(id+"F78.wireOp",EDGE,"E124"),sQuery(id+"F78.wireOp",EDGE,"E125"),sQuery(id+"F78.wireOp",EDGE,"E126"),sQuery(id+"F78.wireOp",EDGE,"E127"),sQuery(id+"F78.wireOp",EDGE,"E128"),sQuery(id+"F78.wireOp",EDGE,"E129.filletArc"),sQuery(id+"F78.wireOp",EDGE,"E130.filletArc")])]});
            var Q1;
            Q1=makeQuery(id+"F79.opExtrude","SWEPT_FACE",FACE,{"disambiguationData":[OSD([sQuery(id+"F78.wireOp",EDGE,"E125")])]});
            mirror(context, id + "F80", {"entities" : qUnion([Q0]), "mirrorPlane" : qUnion([Q1])});
        }
        {
            var Q0;
            Q0=makeQuery(id+"F80.opPattern","COPY",BODY,{"derivedFrom":makeQuery(id+"F79.opExtrude","SWEPT_BODY",BODY,{"disambiguationData":[OSD([sQuery(id+"F78.wireOp",EDGE,"E123"),sQuery(id+"F78.wireOp",EDGE,"E124"),sQuery(id+"F78.wireOp",EDGE,"E125"),sQuery(id+"F78.wireOp",EDGE,"E126"),sQuery(id+"F78.wireOp",EDGE,"E127"),sQuery(id+"F78.wireOp",EDGE,"E128"),sQuery(id+"F78.wireOp",EDGE,"E129.filletArc"),sQuery(id+"F78.wireOp",EDGE,"E130.filletArc")])]}),"instanceName":"1"});
            transform(context, id + "F81", {"entities" : qUnion([Q0]), "transformType" : TransformType.TRANSLATION_3D, "dx" : 0 * mm, "dy" : 0 * mm, "dz" : -498 * mm, "makeCopy" : false});
        }
        {
            var Q0;
            Q0=makeQuery(id+"F69.opPattern","COPY",BODY,{"derivedFrom":makeQuery(id+"F68.opExtrude","SWEPT_BODY",BODY,{"disambiguationData":[OSD([sQuery(id+"F67.wireOp",EDGE,"E107"),sQuery(id+"F67.wireOp",EDGE,"E108"),sQuery(id+"F67.wireOp",EDGE,"E109"),sQuery(id+"F67.wireOp",EDGE,"E110"),sQuery(id+"F67.wireOp",EDGE,"E111"),sQuery(id+"F67.wireOp",EDGE,"E112"),sQuery(id+"F67.wireOp",EDGE,"E113.filletArc"),sQuery(id+"F67.wireOp",EDGE,"E114.filletArc")])]}),"instanceName":"1"});
            transform(context, id + "F82", {"entities" : qUnion([Q0]), "transformType" : TransformType.TRANSLATION_3D, "dx" : -10 * mm, "dy" : 0 * mm, "dz" : 0 * mm, "makeCopy" : false});
        }
        {
            var Q0;
            Q0=makeQuery(id+"F24.opPattern","COPY",BODY,{"derivedFrom":makeQuery(id+"F22.opPattern","COPY",BODY,{"derivedFrom":makeQuery(id+"F20.opExtrude","SWEPT_BODY",BODY,{"disambiguationData":[OSD([sQuery(id+"F19.wireOp",EDGE,"E29.bottom"),sQuery(id+"F19.wireOp",EDGE,"E29.top"),sQuery(id+"F19.wireOp",EDGE,"E29.left"),sQuery(id+"F19.wireOp",EDGE,"E29.right")])]}),"instanceName":"1"}),"instanceName":"1"});
            var Q1;
            Q1=makeQuery(id+"F24.opPattern","COPY",BODY,{"derivedFrom":makeQuery(id+"F21.opPattern","COPY",BODY,{"derivedFrom":makeQuery(id+"F20.opExtrude","SWEPT_BODY",BODY,{"disambiguationData":[OSD([sQuery(id+"F19.wireOp",EDGE,"E29.bottom"),sQuery(id+"F19.wireOp",EDGE,"E29.top"),sQuery(id+"F19.wireOp",EDGE,"E29.left"),sQuery(id+"F19.wireOp",EDGE,"E29.right")])]}),"instanceName":"1"}),"instanceName":"1"});
            var Q2;
            Q2=makeQuery(id+"F24.opPattern","COPY",BODY,{"derivedFrom":makeQuery(id+"F23.opPattern","COPY",BODY,{"derivedFrom":makeQuery(id+"F21.opPattern","COPY",BODY,{"derivedFrom":makeQuery(id+"F20.opExtrude","SWEPT_BODY",BODY,{"disambiguationData":[OSD([sQuery(id+"F19.wireOp",EDGE,"E29.bottom"),sQuery(id+"F19.wireOp",EDGE,"E29.top"),sQuery(id+"F19.wireOp",EDGE,"E29.left"),sQuery(id+"F19.wireOp",EDGE,"E29.right")])]}),"instanceName":"1"}),"instanceName":"1"}),"instanceName":"1"});
            deleteBodies(context, id + "F83", {"entities" : qUnion([Q0, Q1, Q2])});
        }
        {
            var Q0;
            Q0=makeQuery(id+"F20.opExtrude","SWEPT_BODY",BODY,{"disambiguationData":[OSD([sQuery(id+"F19.wireOp",EDGE,"E29.bottom"),sQuery(id+"F19.wireOp",EDGE,"E29.top"),sQuery(id+"F19.wireOp",EDGE,"E29.left"),sQuery(id+"F19.wireOp",EDGE,"E29.right")])]});
            var Q1;
            Q1=makeQuery(id+"F21.opPattern","COPY",BODY,{"derivedFrom":makeQuery(id+"F20.opExtrude","SWEPT_BODY",BODY,{"disambiguationData":[OSD([sQuery(id+"F19.wireOp",EDGE,"E29.bottom"),sQuery(id+"F19.wireOp",EDGE,"E29.top"),sQuery(id+"F19.wireOp",EDGE,"E29.left"),sQuery(id+"F19.wireOp",EDGE,"E29.right")])]}),"instanceName":"1"});
            var Q2;
            Q2=makeQuery(id+"F22.opPattern","COPY",BODY,{"derivedFrom":makeQuery(id+"F20.opExtrude","SWEPT_BODY",BODY,{"disambiguationData":[OSD([sQuery(id+"F19.wireOp",EDGE,"E29.bottom"),sQuery(id+"F19.wireOp",EDGE,"E29.top"),sQuery(id+"F19.wireOp",EDGE,"E29.left"),sQuery(id+"F19.wireOp",EDGE,"E29.right")])]}),"instanceName":"1"});
            var Q3;
            Q3=makeQuery(id+"F23.opPattern","COPY",BODY,{"derivedFrom":makeQuery(id+"F21.opPattern","COPY",BODY,{"derivedFrom":makeQuery(id+"F20.opExtrude","SWEPT_BODY",BODY,{"disambiguationData":[OSD([sQuery(id+"F19.wireOp",EDGE,"E29.bottom"),sQuery(id+"F19.wireOp",EDGE,"E29.top"),sQuery(id+"F19.wireOp",EDGE,"E29.left"),sQuery(id+"F19.wireOp",EDGE,"E29.right")])]}),"instanceName":"1"}),"instanceName":"1"});
            var Q4;
            Q4=makeQuery(id+"F24.opPattern","COPY",BODY,{"derivedFrom":makeQuery(id+"F20.opExtrude","SWEPT_BODY",BODY,{"disambiguationData":[OSD([sQuery(id+"F19.wireOp",EDGE,"E29.bottom"),sQuery(id+"F19.wireOp",EDGE,"E29.top"),sQuery(id+"F19.wireOp",EDGE,"E29.left"),sQuery(id+"F19.wireOp",EDGE,"E29.right")])]}),"instanceName":"1"});
            var Q5;
            Q5=makeQuery(id+"F25.opPattern","COPY",BODY,{"derivedFrom":makeQuery(id+"F20.opExtrude","SWEPT_BODY",BODY,{"disambiguationData":[OSD([sQuery(id+"F19.wireOp",EDGE,"E29.bottom"),sQuery(id+"F19.wireOp",EDGE,"E29.top"),sQuery(id+"F19.wireOp",EDGE,"E29.left"),sQuery(id+"F19.wireOp",EDGE,"E29.right")])]}),"instanceName":"1"});
            var Q6;
            Q6=makeQuery(id+"F25.opPattern","COPY",BODY,{"derivedFrom":makeQuery(id+"F22.opPattern","COPY",BODY,{"derivedFrom":makeQuery(id+"F20.opExtrude","SWEPT_BODY",BODY,{"disambiguationData":[OSD([sQuery(id+"F19.wireOp",EDGE,"E29.bottom"),sQuery(id+"F19.wireOp",EDGE,"E29.top"),sQuery(id+"F19.wireOp",EDGE,"E29.left"),sQuery(id+"F19.wireOp",EDGE,"E29.right")])]}),"instanceName":"1"}),"instanceName":"1"});
            var Q7;
            Q7=makeQuery(id+"F25.opPattern","COPY",BODY,{"derivedFrom":makeQuery(id+"F23.opPattern","COPY",BODY,{"derivedFrom":makeQuery(id+"F21.opPattern","COPY",BODY,{"derivedFrom":makeQuery(id+"F20.opExtrude","SWEPT_BODY",BODY,{"disambiguationData":[OSD([sQuery(id+"F19.wireOp",EDGE,"E29.bottom"),sQuery(id+"F19.wireOp",EDGE,"E29.top"),sQuery(id+"F19.wireOp",EDGE,"E29.left"),sQuery(id+"F19.wireOp",EDGE,"E29.right")])]}),"instanceName":"1"}),"instanceName":"1"}),"instanceName":"1"});
            var Q8;
            Q8=makeQuery(id+"F25.opPattern","COPY",BODY,{"derivedFrom":makeQuery(id+"F21.opPattern","COPY",BODY,{"derivedFrom":makeQuery(id+"F20.opExtrude","SWEPT_BODY",BODY,{"disambiguationData":[OSD([sQuery(id+"F19.wireOp",EDGE,"E29.bottom"),sQuery(id+"F19.wireOp",EDGE,"E29.top"),sQuery(id+"F19.wireOp",EDGE,"E29.left"),sQuery(id+"F19.wireOp",EDGE,"E29.right")])]}),"instanceName":"1"}),"instanceName":"1"});
            var Q9;
            Q9=makeQuery(id+"F25.opPattern","COPY",BODY,{"derivedFrom":makeQuery(id+"F24.opPattern","COPY",BODY,{"derivedFrom":makeQuery(id+"F20.opExtrude","SWEPT_BODY",BODY,{"disambiguationData":[OSD([sQuery(id+"F19.wireOp",EDGE,"E29.bottom"),sQuery(id+"F19.wireOp",EDGE,"E29.top"),sQuery(id+"F19.wireOp",EDGE,"E29.left"),sQuery(id+"F19.wireOp",EDGE,"E29.right")])]}),"instanceName":"1"}),"instanceName":"1"});
            var Q10;
            Q10=makeQuery(id+"F25.opPattern","COPY",BODY,{"derivedFrom":makeQuery(id+"F24.opPattern","COPY",BODY,{"derivedFrom":makeQuery(id+"F21.opPattern","COPY",BODY,{"derivedFrom":makeQuery(id+"F20.opExtrude","SWEPT_BODY",BODY,{"disambiguationData":[OSD([sQuery(id+"F19.wireOp",EDGE,"E29.bottom"),sQuery(id+"F19.wireOp",EDGE,"E29.top"),sQuery(id+"F19.wireOp",EDGE,"E29.left"),sQuery(id+"F19.wireOp",EDGE,"E29.right")])]}),"instanceName":"1"}),"instanceName":"1"}),"instanceName":"1"});
            var Q11;
            Q11=makeQuery(id+"F25.opPattern","COPY",BODY,{"derivedFrom":makeQuery(id+"F24.opPattern","COPY",BODY,{"derivedFrom":makeQuery(id+"F22.opPattern","COPY",BODY,{"derivedFrom":makeQuery(id+"F20.opExtrude","SWEPT_BODY",BODY,{"disambiguationData":[OSD([sQuery(id+"F19.wireOp",EDGE,"E29.bottom"),sQuery(id+"F19.wireOp",EDGE,"E29.top"),sQuery(id+"F19.wireOp",EDGE,"E29.left"),sQuery(id+"F19.wireOp",EDGE,"E29.right")])]}),"instanceName":"1"}),"instanceName":"1"}),"instanceName":"1"});
            var Q12;
            Q12=makeQuery(id+"F25.opPattern","COPY",BODY,{"derivedFrom":makeQuery(id+"F24.opPattern","COPY",BODY,{"derivedFrom":makeQuery(id+"F23.opPattern","COPY",BODY,{"derivedFrom":makeQuery(id+"F21.opPattern","COPY",BODY,{"derivedFrom":makeQuery(id+"F20.opExtrude","SWEPT_BODY",BODY,{"disambiguationData":[OSD([sQuery(id+"F19.wireOp",EDGE,"E29.bottom"),sQuery(id+"F19.wireOp",EDGE,"E29.top"),sQuery(id+"F19.wireOp",EDGE,"E29.left"),sQuery(id+"F19.wireOp",EDGE,"E29.right")])]}),"instanceName":"1"}),"instanceName":"1"}),"instanceName":"1"}),"instanceName":"1"});
            var Q13;
            Q13=makeQuery(id+"F26.opPattern","COPY",BODY,{"derivedFrom":makeQuery(id+"F25.opPattern","COPY",BODY,{"derivedFrom":makeQuery(id+"F21.opPattern","COPY",BODY,{"derivedFrom":makeQuery(id+"F20.opExtrude","SWEPT_BODY",BODY,{"disambiguationData":[OSD([sQuery(id+"F19.wireOp",EDGE,"E29.bottom"),sQuery(id+"F19.wireOp",EDGE,"E29.top"),sQuery(id+"F19.wireOp",EDGE,"E29.left"),sQuery(id+"F19.wireOp",EDGE,"E29.right")])]}),"instanceName":"1"}),"instanceName":"1"}),"instanceName":"1"});
            var Q14;
            Q14=makeQuery(id+"F26.opPattern","COPY",BODY,{"derivedFrom":makeQuery(id+"F25.opPattern","COPY",BODY,{"derivedFrom":makeQuery(id+"F20.opExtrude","SWEPT_BODY",BODY,{"disambiguationData":[OSD([sQuery(id+"F19.wireOp",EDGE,"E29.bottom"),sQuery(id+"F19.wireOp",EDGE,"E29.top"),sQuery(id+"F19.wireOp",EDGE,"E29.left"),sQuery(id+"F19.wireOp",EDGE,"E29.right")])]}),"instanceName":"1"}),"instanceName":"1"});
            var Q15;
            Q15=makeQuery(id+"F26.opPattern","COPY",BODY,{"derivedFrom":makeQuery(id+"F25.opPattern","COPY",BODY,{"derivedFrom":makeQuery(id+"F22.opPattern","COPY",BODY,{"derivedFrom":makeQuery(id+"F20.opExtrude","SWEPT_BODY",BODY,{"disambiguationData":[OSD([sQuery(id+"F19.wireOp",EDGE,"E29.bottom"),sQuery(id+"F19.wireOp",EDGE,"E29.top"),sQuery(id+"F19.wireOp",EDGE,"E29.left"),sQuery(id+"F19.wireOp",EDGE,"E29.right")])]}),"instanceName":"1"}),"instanceName":"1"}),"instanceName":"1"});
            var Q16;
            Q16=makeQuery(id+"F26.opPattern","COPY",BODY,{"derivedFrom":makeQuery(id+"F25.opPattern","COPY",BODY,{"derivedFrom":makeQuery(id+"F23.opPattern","COPY",BODY,{"derivedFrom":makeQuery(id+"F21.opPattern","COPY",BODY,{"derivedFrom":makeQuery(id+"F20.opExtrude","SWEPT_BODY",BODY,{"disambiguationData":[OSD([sQuery(id+"F19.wireOp",EDGE,"E29.bottom"),sQuery(id+"F19.wireOp",EDGE,"E29.top"),sQuery(id+"F19.wireOp",EDGE,"E29.left"),sQuery(id+"F19.wireOp",EDGE,"E29.right")])]}),"instanceName":"1"}),"instanceName":"1"}),"instanceName":"1"}),"instanceName":"1"});
            var Q17;
            Q17=makeQuery(id+"F26.opPattern","COPY",BODY,{"derivedFrom":makeQuery(id+"F25.opPattern","COPY",BODY,{"derivedFrom":makeQuery(id+"F24.opPattern","COPY",BODY,{"derivedFrom":makeQuery(id+"F20.opExtrude","SWEPT_BODY",BODY,{"disambiguationData":[OSD([sQuery(id+"F19.wireOp",EDGE,"E29.bottom"),sQuery(id+"F19.wireOp",EDGE,"E29.top"),sQuery(id+"F19.wireOp",EDGE,"E29.left"),sQuery(id+"F19.wireOp",EDGE,"E29.right")])]}),"instanceName":"1"}),"instanceName":"1"}),"instanceName":"1"});
            deleteBodies(context, id + "F84", {"entities" : qUnion([Q0, Q1, Q2, Q3, Q4, Q5, Q6, Q7, Q8, Q9, Q10, Q11, Q12, Q13, Q14, Q15, Q16, Q17])});
        }
        {
            var Q0;
            Q0=makeQuery(id+"F26.opPattern","COPY",BODY,{"derivedFrom":makeQuery(id+"F25.opPattern","COPY",BODY,{"derivedFrom":makeQuery(id+"F24.opPattern","COPY",BODY,{"derivedFrom":makeQuery(id+"F21.opPattern","COPY",BODY,{"derivedFrom":makeQuery(id+"F20.opExtrude","SWEPT_BODY",BODY,{"disambiguationData":[OSD([sQuery(id+"F19.wireOp",EDGE,"E29.bottom"),sQuery(id+"F19.wireOp",EDGE,"E29.top"),sQuery(id+"F19.wireOp",EDGE,"E29.left"),sQuery(id+"F19.wireOp",EDGE,"E29.right")])]}),"instanceName":"1"}),"instanceName":"1"}),"instanceName":"1"}),"instanceName":"1"});
            var Q1;
            Q1=makeQuery(id+"F26.opPattern","COPY",BODY,{"derivedFrom":makeQuery(id+"F25.opPattern","COPY",BODY,{"derivedFrom":makeQuery(id+"F24.opPattern","COPY",BODY,{"derivedFrom":makeQuery(id+"F23.opPattern","COPY",BODY,{"derivedFrom":makeQuery(id+"F21.opPattern","COPY",BODY,{"derivedFrom":makeQuery(id+"F20.opExtrude","SWEPT_BODY",BODY,{"disambiguationData":[OSD([sQuery(id+"F19.wireOp",EDGE,"E29.bottom"),sQuery(id+"F19.wireOp",EDGE,"E29.top"),sQuery(id+"F19.wireOp",EDGE,"E29.left"),sQuery(id+"F19.wireOp",EDGE,"E29.right")])]}),"instanceName":"1"}),"instanceName":"1"}),"instanceName":"1"}),"instanceName":"1"}),"instanceName":"1"});
            var Q2;
            Q2=makeQuery(id+"F26.opPattern","COPY",BODY,{"derivedFrom":makeQuery(id+"F25.opPattern","COPY",BODY,{"derivedFrom":makeQuery(id+"F24.opPattern","COPY",BODY,{"derivedFrom":makeQuery(id+"F22.opPattern","COPY",BODY,{"derivedFrom":makeQuery(id+"F20.opExtrude","SWEPT_BODY",BODY,{"disambiguationData":[OSD([sQuery(id+"F19.wireOp",EDGE,"E29.bottom"),sQuery(id+"F19.wireOp",EDGE,"E29.top"),sQuery(id+"F19.wireOp",EDGE,"E29.left"),sQuery(id+"F19.wireOp",EDGE,"E29.right")])]}),"instanceName":"1"}),"instanceName":"1"}),"instanceName":"1"}),"instanceName":"1"});
            var Q3;
            Q3=makeQuery(id+"F27.opPattern","COPY",BODY,{"derivedFrom":makeQuery(id+"F26.opPattern","COPY",BODY,{"derivedFrom":makeQuery(id+"F25.opPattern","COPY",BODY,{"derivedFrom":makeQuery(id+"F24.opPattern","COPY",BODY,{"derivedFrom":makeQuery(id+"F21.opPattern","COPY",BODY,{"derivedFrom":makeQuery(id+"F20.opExtrude","SWEPT_BODY",BODY,{"disambiguationData":[OSD([sQuery(id+"F19.wireOp",EDGE,"E29.bottom"),sQuery(id+"F19.wireOp",EDGE,"E29.top"),sQuery(id+"F19.wireOp",EDGE,"E29.left"),sQuery(id+"F19.wireOp",EDGE,"E29.right")])]}),"instanceName":"1"}),"instanceName":"1"}),"instanceName":"1"}),"instanceName":"1"}),"instanceName":"1"});
            var Q4;
            Q4=makeQuery(id+"F27.opPattern","COPY",BODY,{"derivedFrom":makeQuery(id+"F26.opPattern","COPY",BODY,{"derivedFrom":makeQuery(id+"F25.opPattern","COPY",BODY,{"derivedFrom":makeQuery(id+"F24.opPattern","COPY",BODY,{"derivedFrom":makeQuery(id+"F23.opPattern","COPY",BODY,{"derivedFrom":makeQuery(id+"F21.opPattern","COPY",BODY,{"derivedFrom":makeQuery(id+"F20.opExtrude","SWEPT_BODY",BODY,{"disambiguationData":[OSD([sQuery(id+"F19.wireOp",EDGE,"E29.bottom"),sQuery(id+"F19.wireOp",EDGE,"E29.top"),sQuery(id+"F19.wireOp",EDGE,"E29.left"),sQuery(id+"F19.wireOp",EDGE,"E29.right")])]}),"instanceName":"1"}),"instanceName":"1"}),"instanceName":"1"}),"instanceName":"1"}),"instanceName":"1"}),"instanceName":"1"});
            var Q5;
            Q5=makeQuery(id+"F27.opPattern","COPY",BODY,{"derivedFrom":makeQuery(id+"F26.opPattern","COPY",BODY,{"derivedFrom":makeQuery(id+"F25.opPattern","COPY",BODY,{"derivedFrom":makeQuery(id+"F24.opPattern","COPY",BODY,{"derivedFrom":makeQuery(id+"F22.opPattern","COPY",BODY,{"derivedFrom":makeQuery(id+"F20.opExtrude","SWEPT_BODY",BODY,{"disambiguationData":[OSD([sQuery(id+"F19.wireOp",EDGE,"E29.bottom"),sQuery(id+"F19.wireOp",EDGE,"E29.top"),sQuery(id+"F19.wireOp",EDGE,"E29.left"),sQuery(id+"F19.wireOp",EDGE,"E29.right")])]}),"instanceName":"1"}),"instanceName":"1"}),"instanceName":"1"}),"instanceName":"1"}),"instanceName":"1"});
            var Q6;
            Q6=makeQuery(id+"F27.opPattern","COPY",BODY,{"derivedFrom":makeQuery(id+"F26.opPattern","COPY",BODY,{"derivedFrom":makeQuery(id+"F25.opPattern","COPY",BODY,{"derivedFrom":makeQuery(id+"F24.opPattern","COPY",BODY,{"derivedFrom":makeQuery(id+"F20.opExtrude","SWEPT_BODY",BODY,{"disambiguationData":[OSD([sQuery(id+"F19.wireOp",EDGE,"E29.bottom"),sQuery(id+"F19.wireOp",EDGE,"E29.top"),sQuery(id+"F19.wireOp",EDGE,"E29.left"),sQuery(id+"F19.wireOp",EDGE,"E29.right")])]}),"instanceName":"1"}),"instanceName":"1"}),"instanceName":"1"}),"instanceName":"1"});
            var Q7;
            Q7=makeQuery(id+"F28.opPattern","COPY",BODY,{"derivedFrom":makeQuery(id+"F27.opPattern","COPY",BODY,{"derivedFrom":makeQuery(id+"F26.opPattern","COPY",BODY,{"derivedFrom":makeQuery(id+"F25.opPattern","COPY",BODY,{"derivedFrom":makeQuery(id+"F24.opPattern","COPY",BODY,{"derivedFrom":makeQuery(id+"F21.opPattern","COPY",BODY,{"derivedFrom":makeQuery(id+"F20.opExtrude","SWEPT_BODY",BODY,{"disambiguationData":[OSD([sQuery(id+"F19.wireOp",EDGE,"E29.bottom"),sQuery(id+"F19.wireOp",EDGE,"E29.top"),sQuery(id+"F19.wireOp",EDGE,"E29.left"),sQuery(id+"F19.wireOp",EDGE,"E29.right")])]}),"instanceName":"1"}),"instanceName":"1"}),"instanceName":"1"}),"instanceName":"1"}),"instanceName":"1"}),"instanceName":"1"});
            var Q8;
            Q8=makeQuery(id+"F28.opPattern","COPY",BODY,{"derivedFrom":makeQuery(id+"F27.opPattern","COPY",BODY,{"derivedFrom":makeQuery(id+"F26.opPattern","COPY",BODY,{"derivedFrom":makeQuery(id+"F25.opPattern","COPY",BODY,{"derivedFrom":makeQuery(id+"F24.opPattern","COPY",BODY,{"derivedFrom":makeQuery(id+"F23.opPattern","COPY",BODY,{"derivedFrom":makeQuery(id+"F21.opPattern","COPY",BODY,{"derivedFrom":makeQuery(id+"F20.opExtrude","SWEPT_BODY",BODY,{"disambiguationData":[OSD([sQuery(id+"F19.wireOp",EDGE,"E29.bottom"),sQuery(id+"F19.wireOp",EDGE,"E29.top"),sQuery(id+"F19.wireOp",EDGE,"E29.left"),sQuery(id+"F19.wireOp",EDGE,"E29.right")])]}),"instanceName":"1"}),"instanceName":"1"}),"instanceName":"1"}),"instanceName":"1"}),"instanceName":"1"}),"instanceName":"1"}),"instanceName":"1"});
            var Q9;
            Q9=makeQuery(id+"F28.opPattern","COPY",BODY,{"derivedFrom":makeQuery(id+"F27.opPattern","COPY",BODY,{"derivedFrom":makeQuery(id+"F26.opPattern","COPY",BODY,{"derivedFrom":makeQuery(id+"F25.opPattern","COPY",BODY,{"derivedFrom":makeQuery(id+"F24.opPattern","COPY",BODY,{"derivedFrom":makeQuery(id+"F22.opPattern","COPY",BODY,{"derivedFrom":makeQuery(id+"F20.opExtrude","SWEPT_BODY",BODY,{"disambiguationData":[OSD([sQuery(id+"F19.wireOp",EDGE,"E29.bottom"),sQuery(id+"F19.wireOp",EDGE,"E29.top"),sQuery(id+"F19.wireOp",EDGE,"E29.left"),sQuery(id+"F19.wireOp",EDGE,"E29.right")])]}),"instanceName":"1"}),"instanceName":"1"}),"instanceName":"1"}),"instanceName":"1"}),"instanceName":"1"}),"instanceName":"1"});
            var Q10;
            Q10=makeQuery(id+"F28.opPattern","COPY",BODY,{"derivedFrom":makeQuery(id+"F27.opPattern","COPY",BODY,{"derivedFrom":makeQuery(id+"F26.opPattern","COPY",BODY,{"derivedFrom":makeQuery(id+"F25.opPattern","COPY",BODY,{"derivedFrom":makeQuery(id+"F24.opPattern","COPY",BODY,{"derivedFrom":makeQuery(id+"F20.opExtrude","SWEPT_BODY",BODY,{"disambiguationData":[OSD([sQuery(id+"F19.wireOp",EDGE,"E29.bottom"),sQuery(id+"F19.wireOp",EDGE,"E29.top"),sQuery(id+"F19.wireOp",EDGE,"E29.left"),sQuery(id+"F19.wireOp",EDGE,"E29.right")])]}),"instanceName":"1"}),"instanceName":"1"}),"instanceName":"1"}),"instanceName":"1"}),"instanceName":"1"});
            var Q11;
            Q11=makeQuery(id+"F29.opPattern","COPY",BODY,{"derivedFrom":makeQuery(id+"F28.opPattern","COPY",BODY,{"derivedFrom":makeQuery(id+"F27.opPattern","COPY",BODY,{"derivedFrom":makeQuery(id+"F26.opPattern","COPY",BODY,{"derivedFrom":makeQuery(id+"F25.opPattern","COPY",BODY,{"derivedFrom":makeQuery(id+"F24.opPattern","COPY",BODY,{"derivedFrom":makeQuery(id+"F20.opExtrude","SWEPT_BODY",BODY,{"disambiguationData":[OSD([sQuery(id+"F19.wireOp",EDGE,"E29.bottom"),sQuery(id+"F19.wireOp",EDGE,"E29.top"),sQuery(id+"F19.wireOp",EDGE,"E29.left"),sQuery(id+"F19.wireOp",EDGE,"E29.right")])]}),"instanceName":"1"}),"instanceName":"1"}),"instanceName":"1"}),"instanceName":"1"}),"instanceName":"1"}),"instanceName":"1"});
            var Q12;
            Q12=makeQuery(id+"F29.opPattern","COPY",BODY,{"derivedFrom":makeQuery(id+"F28.opPattern","COPY",BODY,{"derivedFrom":makeQuery(id+"F27.opPattern","COPY",BODY,{"derivedFrom":makeQuery(id+"F26.opPattern","COPY",BODY,{"derivedFrom":makeQuery(id+"F25.opPattern","COPY",BODY,{"derivedFrom":makeQuery(id+"F24.opPattern","COPY",BODY,{"derivedFrom":makeQuery(id+"F22.opPattern","COPY",BODY,{"derivedFrom":makeQuery(id+"F20.opExtrude","SWEPT_BODY",BODY,{"disambiguationData":[OSD([sQuery(id+"F19.wireOp",EDGE,"E29.bottom"),sQuery(id+"F19.wireOp",EDGE,"E29.top"),sQuery(id+"F19.wireOp",EDGE,"E29.left"),sQuery(id+"F19.wireOp",EDGE,"E29.right")])]}),"instanceName":"1"}),"instanceName":"1"}),"instanceName":"1"}),"instanceName":"1"}),"instanceName":"1"}),"instanceName":"1"}),"instanceName":"1"});
            var Q13;
            Q13=makeQuery(id+"F29.opPattern","COPY",BODY,{"derivedFrom":makeQuery(id+"F28.opPattern","COPY",BODY,{"derivedFrom":makeQuery(id+"F27.opPattern","COPY",BODY,{"derivedFrom":makeQuery(id+"F26.opPattern","COPY",BODY,{"derivedFrom":makeQuery(id+"F25.opPattern","COPY",BODY,{"derivedFrom":makeQuery(id+"F24.opPattern","COPY",BODY,{"derivedFrom":makeQuery(id+"F23.opPattern","COPY",BODY,{"derivedFrom":makeQuery(id+"F21.opPattern","COPY",BODY,{"derivedFrom":makeQuery(id+"F20.opExtrude","SWEPT_BODY",BODY,{"disambiguationData":[OSD([sQuery(id+"F19.wireOp",EDGE,"E29.bottom"),sQuery(id+"F19.wireOp",EDGE,"E29.top"),sQuery(id+"F19.wireOp",EDGE,"E29.left"),sQuery(id+"F19.wireOp",EDGE,"E29.right")])]}),"instanceName":"1"}),"instanceName":"1"}),"instanceName":"1"}),"instanceName":"1"}),"instanceName":"1"}),"instanceName":"1"}),"instanceName":"1"}),"instanceName":"1"});
            var Q14;
            Q14=makeQuery(id+"F29.opPattern","COPY",BODY,{"derivedFrom":makeQuery(id+"F28.opPattern","COPY",BODY,{"derivedFrom":makeQuery(id+"F27.opPattern","COPY",BODY,{"derivedFrom":makeQuery(id+"F26.opPattern","COPY",BODY,{"derivedFrom":makeQuery(id+"F25.opPattern","COPY",BODY,{"derivedFrom":makeQuery(id+"F24.opPattern","COPY",BODY,{"derivedFrom":makeQuery(id+"F21.opPattern","COPY",BODY,{"derivedFrom":makeQuery(id+"F20.opExtrude","SWEPT_BODY",BODY,{"disambiguationData":[OSD([sQuery(id+"F19.wireOp",EDGE,"E29.bottom"),sQuery(id+"F19.wireOp",EDGE,"E29.top"),sQuery(id+"F19.wireOp",EDGE,"E29.left"),sQuery(id+"F19.wireOp",EDGE,"E29.right")])]}),"instanceName":"1"}),"instanceName":"1"}),"instanceName":"1"}),"instanceName":"1"}),"instanceName":"1"}),"instanceName":"1"}),"instanceName":"1"});
            deleteBodies(context, id + "F85", {"entities" : qUnion([Q0, Q1, Q2, Q3, Q4, Q5, Q6, Q7, Q8, Q9, Q10, Q11, Q12, Q13, Q14])});
        }
        {
            var Q0;
            Q0=makeQuery(id+"F29.opPattern","COPY",BODY,{"derivedFrom":makeQuery(id+"F28.opPattern","COPY",BODY,{"derivedFrom":makeQuery(id+"F27.opPattern","COPY",BODY,{"derivedFrom":makeQuery(id+"F26.opPattern","COPY",BODY,{"derivedFrom":makeQuery(id+"F25.opPattern","COPY",BODY,{"derivedFrom":makeQuery(id+"F21.opPattern","COPY",BODY,{"derivedFrom":makeQuery(id+"F20.opExtrude","SWEPT_BODY",BODY,{"disambiguationData":[OSD([sQuery(id+"F19.wireOp",EDGE,"E29.bottom"),sQuery(id+"F19.wireOp",EDGE,"E29.top"),sQuery(id+"F19.wireOp",EDGE,"E29.left"),sQuery(id+"F19.wireOp",EDGE,"E29.right")])]}),"instanceName":"1"}),"instanceName":"1"}),"instanceName":"1"}),"instanceName":"1"}),"instanceName":"1"}),"instanceName":"1"});
            var Q1;
            Q1=makeQuery(id+"F29.opPattern","COPY",BODY,{"derivedFrom":makeQuery(id+"F28.opPattern","COPY",BODY,{"derivedFrom":makeQuery(id+"F27.opPattern","COPY",BODY,{"derivedFrom":makeQuery(id+"F26.opPattern","COPY",BODY,{"derivedFrom":makeQuery(id+"F25.opPattern","COPY",BODY,{"derivedFrom":makeQuery(id+"F23.opPattern","COPY",BODY,{"derivedFrom":makeQuery(id+"F21.opPattern","COPY",BODY,{"derivedFrom":makeQuery(id+"F20.opExtrude","SWEPT_BODY",BODY,{"disambiguationData":[OSD([sQuery(id+"F19.wireOp",EDGE,"E29.bottom"),sQuery(id+"F19.wireOp",EDGE,"E29.top"),sQuery(id+"F19.wireOp",EDGE,"E29.left"),sQuery(id+"F19.wireOp",EDGE,"E29.right")])]}),"instanceName":"1"}),"instanceName":"1"}),"instanceName":"1"}),"instanceName":"1"}),"instanceName":"1"}),"instanceName":"1"}),"instanceName":"1"});
            var Q2;
            Q2=makeQuery(id+"F29.opPattern","COPY",BODY,{"derivedFrom":makeQuery(id+"F28.opPattern","COPY",BODY,{"derivedFrom":makeQuery(id+"F27.opPattern","COPY",BODY,{"derivedFrom":makeQuery(id+"F26.opPattern","COPY",BODY,{"derivedFrom":makeQuery(id+"F25.opPattern","COPY",BODY,{"derivedFrom":makeQuery(id+"F22.opPattern","COPY",BODY,{"derivedFrom":makeQuery(id+"F20.opExtrude","SWEPT_BODY",BODY,{"disambiguationData":[OSD([sQuery(id+"F19.wireOp",EDGE,"E29.bottom"),sQuery(id+"F19.wireOp",EDGE,"E29.top"),sQuery(id+"F19.wireOp",EDGE,"E29.left"),sQuery(id+"F19.wireOp",EDGE,"E29.right")])]}),"instanceName":"1"}),"instanceName":"1"}),"instanceName":"1"}),"instanceName":"1"}),"instanceName":"1"}),"instanceName":"1"});
            var Q3;
            Q3=makeQuery(id+"F29.opPattern","COPY",BODY,{"derivedFrom":makeQuery(id+"F28.opPattern","COPY",BODY,{"derivedFrom":makeQuery(id+"F27.opPattern","COPY",BODY,{"derivedFrom":makeQuery(id+"F26.opPattern","COPY",BODY,{"derivedFrom":makeQuery(id+"F25.opPattern","COPY",BODY,{"derivedFrom":makeQuery(id+"F20.opExtrude","SWEPT_BODY",BODY,{"disambiguationData":[OSD([sQuery(id+"F19.wireOp",EDGE,"E29.bottom"),sQuery(id+"F19.wireOp",EDGE,"E29.top"),sQuery(id+"F19.wireOp",EDGE,"E29.left"),sQuery(id+"F19.wireOp",EDGE,"E29.right")])]}),"instanceName":"1"}),"instanceName":"1"}),"instanceName":"1"}),"instanceName":"1"}),"instanceName":"1"});
            var Q4;
            Q4=makeQuery(id+"F28.opPattern","COPY",BODY,{"derivedFrom":makeQuery(id+"F27.opPattern","COPY",BODY,{"derivedFrom":makeQuery(id+"F26.opPattern","COPY",BODY,{"derivedFrom":makeQuery(id+"F25.opPattern","COPY",BODY,{"derivedFrom":makeQuery(id+"F20.opExtrude","SWEPT_BODY",BODY,{"disambiguationData":[OSD([sQuery(id+"F19.wireOp",EDGE,"E29.bottom"),sQuery(id+"F19.wireOp",EDGE,"E29.top"),sQuery(id+"F19.wireOp",EDGE,"E29.left"),sQuery(id+"F19.wireOp",EDGE,"E29.right")])]}),"instanceName":"1"}),"instanceName":"1"}),"instanceName":"1"}),"instanceName":"1"});
            var Q5;
            Q5=makeQuery(id+"F28.opPattern","COPY",BODY,{"derivedFrom":makeQuery(id+"F27.opPattern","COPY",BODY,{"derivedFrom":makeQuery(id+"F26.opPattern","COPY",BODY,{"derivedFrom":makeQuery(id+"F25.opPattern","COPY",BODY,{"derivedFrom":makeQuery(id+"F22.opPattern","COPY",BODY,{"derivedFrom":makeQuery(id+"F20.opExtrude","SWEPT_BODY",BODY,{"disambiguationData":[OSD([sQuery(id+"F19.wireOp",EDGE,"E29.bottom"),sQuery(id+"F19.wireOp",EDGE,"E29.top"),sQuery(id+"F19.wireOp",EDGE,"E29.left"),sQuery(id+"F19.wireOp",EDGE,"E29.right")])]}),"instanceName":"1"}),"instanceName":"1"}),"instanceName":"1"}),"instanceName":"1"}),"instanceName":"1"});
            var Q6;
            Q6=makeQuery(id+"F28.opPattern","COPY",BODY,{"derivedFrom":makeQuery(id+"F27.opPattern","COPY",BODY,{"derivedFrom":makeQuery(id+"F26.opPattern","COPY",BODY,{"derivedFrom":makeQuery(id+"F25.opPattern","COPY",BODY,{"derivedFrom":makeQuery(id+"F23.opPattern","COPY",BODY,{"derivedFrom":makeQuery(id+"F21.opPattern","COPY",BODY,{"derivedFrom":makeQuery(id+"F20.opExtrude","SWEPT_BODY",BODY,{"disambiguationData":[OSD([sQuery(id+"F19.wireOp",EDGE,"E29.bottom"),sQuery(id+"F19.wireOp",EDGE,"E29.top"),sQuery(id+"F19.wireOp",EDGE,"E29.left"),sQuery(id+"F19.wireOp",EDGE,"E29.right")])]}),"instanceName":"1"}),"instanceName":"1"}),"instanceName":"1"}),"instanceName":"1"}),"instanceName":"1"}),"instanceName":"1"});
            var Q7;
            Q7=makeQuery(id+"F28.opPattern","COPY",BODY,{"derivedFrom":makeQuery(id+"F27.opPattern","COPY",BODY,{"derivedFrom":makeQuery(id+"F26.opPattern","COPY",BODY,{"derivedFrom":makeQuery(id+"F25.opPattern","COPY",BODY,{"derivedFrom":makeQuery(id+"F21.opPattern","COPY",BODY,{"derivedFrom":makeQuery(id+"F20.opExtrude","SWEPT_BODY",BODY,{"disambiguationData":[OSD([sQuery(id+"F19.wireOp",EDGE,"E29.bottom"),sQuery(id+"F19.wireOp",EDGE,"E29.top"),sQuery(id+"F19.wireOp",EDGE,"E29.left"),sQuery(id+"F19.wireOp",EDGE,"E29.right")])]}),"instanceName":"1"}),"instanceName":"1"}),"instanceName":"1"}),"instanceName":"1"}),"instanceName":"1"});
            var Q8;
            Q8=makeQuery(id+"F27.opPattern","COPY",BODY,{"derivedFrom":makeQuery(id+"F26.opPattern","COPY",BODY,{"derivedFrom":makeQuery(id+"F25.opPattern","COPY",BODY,{"derivedFrom":makeQuery(id+"F21.opPattern","COPY",BODY,{"derivedFrom":makeQuery(id+"F20.opExtrude","SWEPT_BODY",BODY,{"disambiguationData":[OSD([sQuery(id+"F19.wireOp",EDGE,"E29.bottom"),sQuery(id+"F19.wireOp",EDGE,"E29.top"),sQuery(id+"F19.wireOp",EDGE,"E29.left"),sQuery(id+"F19.wireOp",EDGE,"E29.right")])]}),"instanceName":"1"}),"instanceName":"1"}),"instanceName":"1"}),"instanceName":"1"});
            var Q9;
            Q9=makeQuery(id+"F27.opPattern","COPY",BODY,{"derivedFrom":makeQuery(id+"F26.opPattern","COPY",BODY,{"derivedFrom":makeQuery(id+"F25.opPattern","COPY",BODY,{"derivedFrom":makeQuery(id+"F23.opPattern","COPY",BODY,{"derivedFrom":makeQuery(id+"F21.opPattern","COPY",BODY,{"derivedFrom":makeQuery(id+"F20.opExtrude","SWEPT_BODY",BODY,{"disambiguationData":[OSD([sQuery(id+"F19.wireOp",EDGE,"E29.bottom"),sQuery(id+"F19.wireOp",EDGE,"E29.top"),sQuery(id+"F19.wireOp",EDGE,"E29.left"),sQuery(id+"F19.wireOp",EDGE,"E29.right")])]}),"instanceName":"1"}),"instanceName":"1"}),"instanceName":"1"}),"instanceName":"1"}),"instanceName":"1"});
            var Q10;
            Q10=makeQuery(id+"F27.opPattern","COPY",BODY,{"derivedFrom":makeQuery(id+"F26.opPattern","COPY",BODY,{"derivedFrom":makeQuery(id+"F25.opPattern","COPY",BODY,{"derivedFrom":makeQuery(id+"F22.opPattern","COPY",BODY,{"derivedFrom":makeQuery(id+"F20.opExtrude","SWEPT_BODY",BODY,{"disambiguationData":[OSD([sQuery(id+"F19.wireOp",EDGE,"E29.bottom"),sQuery(id+"F19.wireOp",EDGE,"E29.top"),sQuery(id+"F19.wireOp",EDGE,"E29.left"),sQuery(id+"F19.wireOp",EDGE,"E29.right")])]}),"instanceName":"1"}),"instanceName":"1"}),"instanceName":"1"}),"instanceName":"1"});
            var Q11;
            Q11=makeQuery(id+"F27.opPattern","COPY",BODY,{"derivedFrom":makeQuery(id+"F26.opPattern","COPY",BODY,{"derivedFrom":makeQuery(id+"F25.opPattern","COPY",BODY,{"derivedFrom":makeQuery(id+"F20.opExtrude","SWEPT_BODY",BODY,{"disambiguationData":[OSD([sQuery(id+"F19.wireOp",EDGE,"E29.bottom"),sQuery(id+"F19.wireOp",EDGE,"E29.top"),sQuery(id+"F19.wireOp",EDGE,"E29.left"),sQuery(id+"F19.wireOp",EDGE,"E29.right")])]}),"instanceName":"1"}),"instanceName":"1"}),"instanceName":"1"});
            deleteBodies(context, id + "F86", {"entities" : qUnion([Q0, Q1, Q2, Q3, Q4, Q5, Q6, Q7, Q8, Q9, Q10, Q11])});
        }
        {
            var Q0;
            Q0=makeQuery(id+"F3.opPattern","COPY",FACE,{"derivedFrom":makeQuery(id+"F2.opPattern","COPY",FACE,{"derivedFrom":makeQuery(id+"F1.opExtrude","SWEPT_FACE",FACE,{"disambiguationData":[OSD([sQuery(id+"F0.wireOp",EDGE,"E0.top")])]}),"instanceName":"1"}),"instanceName":"1"});
            var sketch = newSketch(context, id + "F87", { "sketchPlane" : qUnion([Q0])});
            skLineSegment(sketch, "E131.bottom", {"start": v(407.5, 1890) * mm, "end": v(419.5, 1890) * mm});
            skLineSegment(sketch, "E131.top", {"start": v(407.5, 1878) * mm, "end": v(419.5, 1878) * mm});
            skLineSegment(sketch, "E131.left", {"start": v(407.5, 1890) * mm, "end": v(407.5, 1878) * mm});
            skLineSegment(sketch, "E131.right", {"start": v(419.5, 1890) * mm, "end": v(419.5, 1878) * mm});
            skSolve(sketch);
        }
        {
            var Q0;
            {var subQ0=sQuery(id+"F87.wireOp",EDGE,"E131.right");Q0=makeQuery(id+"F87.imprint","IMPRINT",FACE,{"disambiguationData":[TD([[makeQuery(id+"F87.imprint","IMPRINT",EDGE,{"derivedFrom":subQ0}),-1.0]])]});}
            extrude(context, id + "F88", {"entities" : qUnion([Q0]), "depth" : 80 * mm});
        }
        {
            var Q0;
            Q0=makeQuery(id+"F88.opExtrude","SWEPT_BODY",BODY,{"disambiguationData":[OSD([sQuery(id+"F0.wireOp",EDGE,"E0.top"),sQuery(id+"F0.wireOp",EDGE,"E5.filletArc"),sQuery(id+"F87.wireOp",EDGE,"E131.bottom"),sQuery(id+"F87.wireOp",EDGE,"E131.top"),sQuery(id+"F87.wireOp",EDGE,"E131.right")])]});
            transform(context, id + "F89", {"entities" : qUnion([Q0]), "transformType" : TransformType.TRANSLATION_3D, "dx" : 150 * mm, "dy" : 0 * mm, "dz" : 0 * mm, "makeCopy" : false});
        }
        {
            var Q0;
            Q0=makeQuery(id+"F88.opExtrude","SWEPT_BODY",BODY,{"disambiguationData":[OSD([sQuery(id+"F0.wireOp",EDGE,"E0.top"),sQuery(id+"F0.wireOp",EDGE,"E5.filletArc"),sQuery(id+"F87.wireOp",EDGE,"E131.bottom"),sQuery(id+"F87.wireOp",EDGE,"E131.top"),sQuery(id+"F87.wireOp",EDGE,"E131.right")])]});
            transform(context, id + "F90", {"entities" : qUnion([Q0]), "transformType" : TransformType.TRANSLATION_3D, "dx" : 770 * mm, "dy" : 0 * mm, "dz" : 0 * mm, "makeCopy" : true});
        }
        {
            var Q0;
            Q0=makeQuery(id+"F88.opExtrude","SWEPT_BODY",BODY,{"disambiguationData":[OSD([sQuery(id+"F0.wireOp",EDGE,"E0.top"),sQuery(id+"F0.wireOp",EDGE,"E5.filletArc"),sQuery(id+"F87.wireOp",EDGE,"E131.bottom"),sQuery(id+"F87.wireOp",EDGE,"E131.top"),sQuery(id+"F87.wireOp",EDGE,"E131.right")])]});
            transform(context, id + "F91", {"entities" : qUnion([Q0]), "transformType" : TransformType.TRANSLATION_3D, "dx" : 385 * mm, "dy" : 0 * mm, "dz" : 0 * mm, "makeCopy" : true});
        }
        {
            var Q0;
            Q0=makeQuery(id+"F3.opPattern","COPY",FACE,{"derivedFrom":makeQuery(id+"F2.opPattern","COPY",FACE,{"derivedFrom":makeQuery(id+"F1.opExtrude","SWEPT_FACE",FACE,{"disambiguationData":[OSD([sQuery(id+"F0.wireOp",EDGE,"E0.top")])]}),"instanceName":"1"}),"instanceName":"1"});
            var sketch = newSketch(context, id + "F92", { "sketchPlane" : qUnion([Q0])});
            skLineSegment(sketch, "E132.bottom", {"start": v(405.5, 1890) * mm, "end": v(407.5, 1890) * mm});
            skLineSegment(sketch, "E132.top", {"start": v(405.5, 1878) * mm, "end": v(407.5, 1878) * mm});
            skLineSegment(sketch, "E132.left", {"start": v(405.5, 1890) * mm, "end": v(405.5, 1878) * mm});
            skLineSegment(sketch, "E132.right", {"start": v(407.5, 1890) * mm, "end": v(407.5, 1878) * mm});
            skSolve(sketch);
        }
        {
            var Q0;
            Q0=makeQuery(id+"F92.imprint","IMPRINT",FACE,{"disambiguationData":[TD([[makeQuery(id+"F92.imprint","IMPRINT",EDGE,{"derivedFrom":sQuery(id+"F92.wireOp",EDGE,"E132.bottom")}),-1.0]])]});
            extrude(context, id + "F93", {"entities" : qUnion([Q0]), "depth" : 1150 * mm});
        }
        {
            var Q0;
            Q0=makeQuery(id+"F93.opExtrude","SWEPT_BODY",BODY,{"disambiguationData":[OSD([sQuery(id+"F92.wireOp",EDGE,"E132.bottom"),sQuery(id+"F92.wireOp",EDGE,"E132.top"),sQuery(id+"F92.wireOp",EDGE,"E132.left"),sQuery(id+"F92.wireOp",EDGE,"E132.right")])]});
            var Q1;
            Q1=makeQuery(id+"F91.opPattern","COPY",BODY,{"derivedFrom":makeQuery(id+"F88.opExtrude","SWEPT_BODY",BODY,{"disambiguationData":[OSD([sQuery(id+"F0.wireOp",EDGE,"E0.top"),sQuery(id+"F0.wireOp",EDGE,"E5.filletArc"),sQuery(id+"F87.wireOp",EDGE,"E131.bottom"),sQuery(id+"F87.wireOp",EDGE,"E131.top"),sQuery(id+"F87.wireOp",EDGE,"E131.right")])]}),"instanceName":"1"});
            var Q2;
            Q2=makeQuery(id+"F90.opPattern","COPY",BODY,{"derivedFrom":makeQuery(id+"F88.opExtrude","SWEPT_BODY",BODY,{"disambiguationData":[OSD([sQuery(id+"F0.wireOp",EDGE,"E0.top"),sQuery(id+"F0.wireOp",EDGE,"E5.filletArc"),sQuery(id+"F87.wireOp",EDGE,"E131.bottom"),sQuery(id+"F87.wireOp",EDGE,"E131.top"),sQuery(id+"F87.wireOp",EDGE,"E131.right")])]}),"instanceName":"1"});
            var Q3;
            Q3=makeQuery(id+"F88.opExtrude","SWEPT_BODY",BODY,{"disambiguationData":[OSD([sQuery(id+"F0.wireOp",EDGE,"E0.top"),sQuery(id+"F0.wireOp",EDGE,"E5.filletArc"),sQuery(id+"F87.wireOp",EDGE,"E131.bottom"),sQuery(id+"F87.wireOp",EDGE,"E131.top"),sQuery(id+"F87.wireOp",EDGE,"E131.right")])]});
            deleteBodies(context, id + "F94", {"entities" : qUnion([Q0, Q1, Q2, Q3])});
        }
        {
            var Q0;
            Q0=makeQuery(id+"F3.opPattern","COPY",FACE,{"derivedFrom":makeQuery(id+"F2.opPattern","COPY",FACE,{"derivedFrom":makeQuery(id+"F1.opExtrude","SWEPT_FACE",FACE,{"disambiguationData":[OSD([sQuery(id+"F0.wireOp",EDGE,"E0.top")])]}),"instanceName":"1"}),"instanceName":"1"});
            var sketch = newSketch(context, id + "F95", { "sketchPlane" : qUnion([Q0])});
            skLineSegment(sketch, "E133.bottom", {"start": v(405.5, 1890) * mm, "end": v(407.5, 1890) * mm});
            skLineSegment(sketch, "E133.top", {"start": v(405.5, 1878) * mm, "end": v(407.5, 1878) * mm});
            skLineSegment(sketch, "E133.left", {"start": v(405.5, 1890) * mm, "end": v(405.5, 1878) * mm});
            skLineSegment(sketch, "E133.right", {"start": v(407.5, 1890) * mm, "end": v(407.5, 1878) * mm});
            skSolve(sketch);
        }
        {
            var Q0;
            Q0=makeQuery(id+"F95.imprint","IMPRINT",FACE,{"disambiguationData":[TD([[makeQuery(id+"F95.imprint","IMPRINT",EDGE,{"derivedFrom":sQuery(id+"F95.wireOp",EDGE,"E133.bottom")}),-1.0]])]});
            extrude(context, id + "F96", {"entities" : qUnion([Q0]), "depth" : 1150 * mm});
        }
        {
            var Q0;
            Q0=makeQuery(id+"F3.opPattern","COPY",FACE,{"derivedFrom":makeQuery(id+"F2.opPattern","COPY",FACE,{"derivedFrom":makeQuery(id+"F1.opExtrude","SWEPT_FACE",FACE,{"disambiguationData":[OSD([sQuery(id+"F0.wireOp",EDGE,"E0.top")])]}),"instanceName":"1"}),"instanceName":"1"});
            var sketch = newSketch(context, id + "F97", { "sketchPlane" : qUnion([Q0])});
            skLineSegment(sketch, "E134.bottom", {"start": v(407.5, 1890) * mm, "end": v(419.5, 1890) * mm});
            skLineSegment(sketch, "E134.top", {"start": v(407.5, 1878) * mm, "end": v(419.5, 1878) * mm});
            skLineSegment(sketch, "E134.left", {"start": v(407.5, 1890) * mm, "end": v(407.5, 1878) * mm});
            skLineSegment(sketch, "E134.right", {"start": v(419.5, 1890) * mm, "end": v(419.5, 1878) * mm});
            skSolve(sketch);
        }
        {
            var Q0;
            {var subQ0=sQuery(id+"F97.wireOp",EDGE,"E134.right");Q0=makeQuery(id+"F97.imprint","IMPRINT",FACE,{"disambiguationData":[TD([[makeQuery(id+"F97.imprint","IMPRINT",EDGE,{"derivedFrom":subQ0}),-1.0]])]});}
            var Q1;
            {var subQ0=sQuery(id+"F97.wireOp",EDGE,"E134.left");Q1=makeQuery(id+"F97.imprint","IMPRINT",FACE,{"disambiguationData":[TD([[makeQuery(id+"F97.imprint","IMPRINT",EDGE,{"derivedFrom":subQ0}),1.0]])]});}
            extrude(context, id + "F98", {"entities" : qUnion([Q0, Q1]), "depth" : 80 * mm});
        }
        {
            var Q0;
            Q0=makeQuery(id+"F98.opExtrude","SWEPT_BODY",BODY,{"disambiguationData":[OSD([sQuery(id+"F97.wireOp",EDGE,"E134.bottom"),sQuery(id+"F97.wireOp",EDGE,"E134.top"),sQuery(id+"F97.wireOp",EDGE,"E134.left"),sQuery(id+"F97.wireOp",EDGE,"E134.right")])]});
            transform(context, id + "F99", {"entities" : qUnion([Q0]), "transformType" : TransformType.TRANSLATION_3D, "dx" : 150 * mm, "dy" : 0 * mm, "dz" : 0 * mm, "makeCopy" : false});
        }
        {
            var Q0;
            Q0=makeQuery(id+"F98.opExtrude","SWEPT_BODY",BODY,{"disambiguationData":[OSD([sQuery(id+"F97.wireOp",EDGE,"E134.bottom"),sQuery(id+"F97.wireOp",EDGE,"E134.top"),sQuery(id+"F97.wireOp",EDGE,"E134.left"),sQuery(id+"F97.wireOp",EDGE,"E134.right")])]});
            transform(context, id + "F100", {"entities" : qUnion([Q0]), "transformType" : TransformType.TRANSLATION_3D, "dx" : 770 * mm, "dy" : 0 * mm, "dz" : 0 * mm, "makeCopy" : true});
        }
        {
            var Q0;
            Q0=makeQuery(id+"F96.opExtrude","SWEPT_BODY",BODY,{"disambiguationData":[OSD([sQuery(id+"F95.wireOp",EDGE,"E133.bottom"),sQuery(id+"F95.wireOp",EDGE,"E133.top"),sQuery(id+"F95.wireOp",EDGE,"E133.left"),sQuery(id+"F95.wireOp",EDGE,"E133.right")])]});
            var Q1;
            Q1=makeQuery(id+"F98.opExtrude","SWEPT_BODY",BODY,{"disambiguationData":[OSD([sQuery(id+"F97.wireOp",EDGE,"E134.bottom"),sQuery(id+"F97.wireOp",EDGE,"E134.top"),sQuery(id+"F97.wireOp",EDGE,"E134.left"),sQuery(id+"F97.wireOp",EDGE,"E134.right")])]});
            var Q2;
            Q2=makeQuery(id+"F100.opPattern","COPY",BODY,{"derivedFrom":makeQuery(id+"F98.opExtrude","SWEPT_BODY",BODY,{"disambiguationData":[OSD([sQuery(id+"F97.wireOp",EDGE,"E134.bottom"),sQuery(id+"F97.wireOp",EDGE,"E134.top"),sQuery(id+"F97.wireOp",EDGE,"E134.left"),sQuery(id+"F97.wireOp",EDGE,"E134.right")])]}),"instanceName":"1"});
            transform(context, id + "F101", {"entities" : qUnion([Q0, Q1, Q2]), "transformType" : TransformType.TRANSLATION_3D, "dx" : 0 * mm, "dy" : 0 * mm, "dz" : -430 * mm, "makeCopy" : true});
        }
        {
            var Q0;
            Q0=makeQuery(id+"F101.opPattern","COPY",BODY,{"derivedFrom":makeQuery(id+"F98.opExtrude","SWEPT_BODY",BODY,{"disambiguationData":[OSD([sQuery(id+"F97.wireOp",EDGE,"E134.bottom"),sQuery(id+"F97.wireOp",EDGE,"E134.top"),sQuery(id+"F97.wireOp",EDGE,"E134.left"),sQuery(id+"F97.wireOp",EDGE,"E134.right")])]}),"instanceName":"1"});
            var Q1;
            Q1=makeQuery(id+"F101.opPattern","COPY",BODY,{"derivedFrom":makeQuery(id+"F100.opPattern","COPY",BODY,{"derivedFrom":makeQuery(id+"F98.opExtrude","SWEPT_BODY",BODY,{"disambiguationData":[OSD([sQuery(id+"F97.wireOp",EDGE,"E134.bottom"),sQuery(id+"F97.wireOp",EDGE,"E134.top"),sQuery(id+"F97.wireOp",EDGE,"E134.left"),sQuery(id+"F97.wireOp",EDGE,"E134.right")])]}),"instanceName":"1"}),"instanceName":"1"});
            var Q2;
            Q2=makeQuery(id+"F101.opPattern","COPY",BODY,{"derivedFrom":makeQuery(id+"F96.opExtrude","SWEPT_BODY",BODY,{"disambiguationData":[OSD([sQuery(id+"F95.wireOp",EDGE,"E133.bottom"),sQuery(id+"F95.wireOp",EDGE,"E133.top"),sQuery(id+"F95.wireOp",EDGE,"E133.left"),sQuery(id+"F95.wireOp",EDGE,"E133.right")])]}),"instanceName":"1"});
            transform(context, id + "F102", {"entities" : qUnion([Q0, Q1, Q2]), "transformType" : TransformType.TRANSLATION_3D, "dx" : 0 * mm, "dy" : 0 * mm, "dz" : -295 * mm, "makeCopy" : false});
        }
        {
            var Q0;
            Q0=makeQuery(id+"F101.opPattern","COPY",BODY,{"derivedFrom":makeQuery(id+"F96.opExtrude","SWEPT_BODY",BODY,{"disambiguationData":[OSD([sQuery(id+"F95.wireOp",EDGE,"E133.bottom"),sQuery(id+"F95.wireOp",EDGE,"E133.top"),sQuery(id+"F95.wireOp",EDGE,"E133.left"),sQuery(id+"F95.wireOp",EDGE,"E133.right")])]}),"instanceName":"1"});
            var Q1;
            Q1=makeQuery(id+"F101.opPattern","COPY",BODY,{"derivedFrom":makeQuery(id+"F98.opExtrude","SWEPT_BODY",BODY,{"disambiguationData":[OSD([sQuery(id+"F97.wireOp",EDGE,"E134.bottom"),sQuery(id+"F97.wireOp",EDGE,"E134.top"),sQuery(id+"F97.wireOp",EDGE,"E134.left"),sQuery(id+"F97.wireOp",EDGE,"E134.right")])]}),"instanceName":"1"});
            var Q2;
            Q2=makeQuery(id+"F101.opPattern","COPY",BODY,{"derivedFrom":makeQuery(id+"F100.opPattern","COPY",BODY,{"derivedFrom":makeQuery(id+"F98.opExtrude","SWEPT_BODY",BODY,{"disambiguationData":[OSD([sQuery(id+"F97.wireOp",EDGE,"E134.bottom"),sQuery(id+"F97.wireOp",EDGE,"E134.top"),sQuery(id+"F97.wireOp",EDGE,"E134.left"),sQuery(id+"F97.wireOp",EDGE,"E134.right")])]}),"instanceName":"1"}),"instanceName":"1"});
            transform(context, id + "F103", {"entities" : qUnion([Q0, Q1, Q2]), "transformType" : TransformType.TRANSLATION_3D, "dx" : 0 * mm, "dy" : 0 * mm, "dz" : -295 * mm, "makeCopy" : true});
        }
        {
            var Q0;
            Q0=makeQuery(id+"F103.opPattern","COPY",BODY,{"derivedFrom":makeQuery(id+"F101.opPattern","COPY",BODY,{"derivedFrom":makeQuery(id+"F98.opExtrude","SWEPT_BODY",BODY,{"disambiguationData":[OSD([sQuery(id+"F97.wireOp",EDGE,"E134.bottom"),sQuery(id+"F97.wireOp",EDGE,"E134.top"),sQuery(id+"F97.wireOp",EDGE,"E134.left"),sQuery(id+"F97.wireOp",EDGE,"E134.right")])]}),"instanceName":"1"}),"instanceName":"1"});
            var Q1;
            Q1=makeQuery(id+"F103.opPattern","COPY",BODY,{"derivedFrom":makeQuery(id+"F101.opPattern","COPY",BODY,{"derivedFrom":makeQuery(id+"F96.opExtrude","SWEPT_BODY",BODY,{"disambiguationData":[OSD([sQuery(id+"F95.wireOp",EDGE,"E133.bottom"),sQuery(id+"F95.wireOp",EDGE,"E133.top"),sQuery(id+"F95.wireOp",EDGE,"E133.left"),sQuery(id+"F95.wireOp",EDGE,"E133.right")])]}),"instanceName":"1"}),"instanceName":"1"});
            var Q2;
            Q2=makeQuery(id+"F103.opPattern","COPY",BODY,{"derivedFrom":makeQuery(id+"F101.opPattern","COPY",BODY,{"derivedFrom":makeQuery(id+"F100.opPattern","COPY",BODY,{"derivedFrom":makeQuery(id+"F98.opExtrude","SWEPT_BODY",BODY,{"disambiguationData":[OSD([sQuery(id+"F97.wireOp",EDGE,"E134.bottom"),sQuery(id+"F97.wireOp",EDGE,"E134.top"),sQuery(id+"F97.wireOp",EDGE,"E134.left"),sQuery(id+"F97.wireOp",EDGE,"E134.right")])]}),"instanceName":"1"}),"instanceName":"1"}),"instanceName":"1"});
            transform(context, id + "F104", {"entities" : qUnion([Q0, Q1, Q2]), "transformType" : TransformType.TRANSLATION_3D, "dx" : 0 * mm, "dy" : 0 * mm, "dz" : -340 * mm, "makeCopy" : false});
        }
        {
            var Q0;
            Q0=makeQuery(id+"F101.opPattern","COPY",BODY,{"derivedFrom":makeQuery(id+"F98.opExtrude","SWEPT_BODY",BODY,{"disambiguationData":[OSD([sQuery(id+"F97.wireOp",EDGE,"E134.bottom"),sQuery(id+"F97.wireOp",EDGE,"E134.top"),sQuery(id+"F97.wireOp",EDGE,"E134.left"),sQuery(id+"F97.wireOp",EDGE,"E134.right")])]}),"instanceName":"1"});
            var Q1;
            Q1=makeQuery(id+"F101.opPattern","COPY",BODY,{"derivedFrom":makeQuery(id+"F96.opExtrude","SWEPT_BODY",BODY,{"disambiguationData":[OSD([sQuery(id+"F95.wireOp",EDGE,"E133.bottom"),sQuery(id+"F95.wireOp",EDGE,"E133.top"),sQuery(id+"F95.wireOp",EDGE,"E133.left"),sQuery(id+"F95.wireOp",EDGE,"E133.right")])]}),"instanceName":"1"});
            var Q2;
            Q2=makeQuery(id+"F101.opPattern","COPY",BODY,{"derivedFrom":makeQuery(id+"F100.opPattern","COPY",BODY,{"derivedFrom":makeQuery(id+"F98.opExtrude","SWEPT_BODY",BODY,{"disambiguationData":[OSD([sQuery(id+"F97.wireOp",EDGE,"E134.bottom"),sQuery(id+"F97.wireOp",EDGE,"E134.top"),sQuery(id+"F97.wireOp",EDGE,"E134.left"),sQuery(id+"F97.wireOp",EDGE,"E134.right")])]}),"instanceName":"1"}),"instanceName":"1"});
            transform(context, id + "F105", {"entities" : qUnion([Q0, Q1, Q2]), "transformType" : TransformType.TRANSLATION_3D, "dx" : 0 * mm, "dy" : 0 * mm, "dz" : -295 * mm, "makeCopy" : true});
        }
        {
            var Q0;
            Q0=makeQuery(id+"F103.opPattern","COPY",BODY,{"derivedFrom":makeQuery(id+"F101.opPattern","COPY",BODY,{"derivedFrom":makeQuery(id+"F96.opExtrude","SWEPT_BODY",BODY,{"disambiguationData":[OSD([sQuery(id+"F95.wireOp",EDGE,"E133.bottom"),sQuery(id+"F95.wireOp",EDGE,"E133.top"),sQuery(id+"F95.wireOp",EDGE,"E133.left"),sQuery(id+"F95.wireOp",EDGE,"E133.right")])]}),"instanceName":"1"}),"instanceName":"1"});
            var Q1;
            Q1=makeQuery(id+"F103.opPattern","COPY",BODY,{"derivedFrom":makeQuery(id+"F101.opPattern","COPY",BODY,{"derivedFrom":makeQuery(id+"F100.opPattern","COPY",BODY,{"derivedFrom":makeQuery(id+"F98.opExtrude","SWEPT_BODY",BODY,{"disambiguationData":[OSD([sQuery(id+"F97.wireOp",EDGE,"E134.bottom"),sQuery(id+"F97.wireOp",EDGE,"E134.top"),sQuery(id+"F97.wireOp",EDGE,"E134.left"),sQuery(id+"F97.wireOp",EDGE,"E134.right")])]}),"instanceName":"1"}),"instanceName":"1"}),"instanceName":"1"});
            var Q2;
            Q2=makeQuery(id+"F103.opPattern","COPY",BODY,{"derivedFrom":makeQuery(id+"F101.opPattern","COPY",BODY,{"derivedFrom":makeQuery(id+"F98.opExtrude","SWEPT_BODY",BODY,{"disambiguationData":[OSD([sQuery(id+"F97.wireOp",EDGE,"E134.bottom"),sQuery(id+"F97.wireOp",EDGE,"E134.top"),sQuery(id+"F97.wireOp",EDGE,"E134.left"),sQuery(id+"F97.wireOp",EDGE,"E134.right")])]}),"instanceName":"1"}),"instanceName":"1"});
            transform(context, id + "F106", {"entities" : qUnion([Q0, Q1, Q2]), "transformType" : TransformType.TRANSLATION_3D, "dx" : 0 * mm, "dy" : 0 * mm, "dz" : -515 * mm, "makeCopy" : true});
        }
        {
            var Q0;
            Q0=makeQuery(id+"F2.opPattern","COPY",FACE,{"derivedFrom":makeQuery(id+"F1.opExtrude","SWEPT_FACE",FACE,{"disambiguationData":[OSD([sQuery(id+"F0.wireOp",EDGE,"E0.left")])]}),"instanceName":"1"});
            cPlane(context, id + "F107", {"entities" : qUnion([Q0]), "cplaneType" : CPlaneType.OFFSET, "offset" : 195 * mm, "width" : 150 * mm, "height" : 150 * mm});
        }
        {
            var Q0;
            Q0=makeQuery(id+"F106.opPattern","COPY",BODY,{"derivedFrom":makeQuery(id+"F103.opPattern","COPY",BODY,{"derivedFrom":makeQuery(id+"F101.opPattern","COPY",BODY,{"derivedFrom":makeQuery(id+"F96.opExtrude","SWEPT_BODY",BODY,{"disambiguationData":[OSD([sQuery(id+"F95.wireOp",EDGE,"E133.bottom"),sQuery(id+"F95.wireOp",EDGE,"E133.top"),sQuery(id+"F95.wireOp",EDGE,"E133.left"),sQuery(id+"F95.wireOp",EDGE,"E133.right")])]}),"instanceName":"1"}),"instanceName":"1"}),"instanceName":"1"});
            var Q1;
            Q1=makeQuery(id+"F106.opPattern","COPY",BODY,{"derivedFrom":makeQuery(id+"F103.opPattern","COPY",BODY,{"derivedFrom":makeQuery(id+"F101.opPattern","COPY",BODY,{"derivedFrom":makeQuery(id+"F100.opPattern","COPY",BODY,{"derivedFrom":makeQuery(id+"F98.opExtrude","SWEPT_BODY",BODY,{"disambiguationData":[OSD([sQuery(id+"F97.wireOp",EDGE,"E134.bottom"),sQuery(id+"F97.wireOp",EDGE,"E134.top"),sQuery(id+"F97.wireOp",EDGE,"E134.left"),sQuery(id+"F97.wireOp",EDGE,"E134.right")])]}),"instanceName":"1"}),"instanceName":"1"}),"instanceName":"1"}),"instanceName":"1"});
            var Q2;
            Q2=makeQuery(id+"F106.opPattern","COPY",BODY,{"derivedFrom":makeQuery(id+"F103.opPattern","COPY",BODY,{"derivedFrom":makeQuery(id+"F101.opPattern","COPY",BODY,{"derivedFrom":makeQuery(id+"F98.opExtrude","SWEPT_BODY",BODY,{"disambiguationData":[OSD([sQuery(id+"F97.wireOp",EDGE,"E134.bottom"),sQuery(id+"F97.wireOp",EDGE,"E134.top"),sQuery(id+"F97.wireOp",EDGE,"E134.left"),sQuery(id+"F97.wireOp",EDGE,"E134.right")])]}),"instanceName":"1"}),"instanceName":"1"}),"instanceName":"1"});
            var Q3;
            Q3=makeQuery(id+"F103.opPattern","COPY",BODY,{"derivedFrom":makeQuery(id+"F101.opPattern","COPY",BODY,{"derivedFrom":makeQuery(id+"F96.opExtrude","SWEPT_BODY",BODY,{"disambiguationData":[OSD([sQuery(id+"F95.wireOp",EDGE,"E133.bottom"),sQuery(id+"F95.wireOp",EDGE,"E133.top"),sQuery(id+"F95.wireOp",EDGE,"E133.left"),sQuery(id+"F95.wireOp",EDGE,"E133.right")])]}),"instanceName":"1"}),"instanceName":"1"});
            var Q4;
            Q4=makeQuery(id+"F103.opPattern","COPY",BODY,{"derivedFrom":makeQuery(id+"F101.opPattern","COPY",BODY,{"derivedFrom":makeQuery(id+"F100.opPattern","COPY",BODY,{"derivedFrom":makeQuery(id+"F98.opExtrude","SWEPT_BODY",BODY,{"disambiguationData":[OSD([sQuery(id+"F97.wireOp",EDGE,"E134.bottom"),sQuery(id+"F97.wireOp",EDGE,"E134.top"),sQuery(id+"F97.wireOp",EDGE,"E134.left"),sQuery(id+"F97.wireOp",EDGE,"E134.right")])]}),"instanceName":"1"}),"instanceName":"1"}),"instanceName":"1"});
            var Q5;
            Q5=makeQuery(id+"F103.opPattern","COPY",BODY,{"derivedFrom":makeQuery(id+"F101.opPattern","COPY",BODY,{"derivedFrom":makeQuery(id+"F98.opExtrude","SWEPT_BODY",BODY,{"disambiguationData":[OSD([sQuery(id+"F97.wireOp",EDGE,"E134.bottom"),sQuery(id+"F97.wireOp",EDGE,"E134.top"),sQuery(id+"F97.wireOp",EDGE,"E134.left"),sQuery(id+"F97.wireOp",EDGE,"E134.right")])]}),"instanceName":"1"}),"instanceName":"1"});
            var Q6;
            Q6=makeQuery(id+"F105.opPattern","COPY",BODY,{"derivedFrom":makeQuery(id+"F101.opPattern","COPY",BODY,{"derivedFrom":makeQuery(id+"F96.opExtrude","SWEPT_BODY",BODY,{"disambiguationData":[OSD([sQuery(id+"F95.wireOp",EDGE,"E133.bottom"),sQuery(id+"F95.wireOp",EDGE,"E133.top"),sQuery(id+"F95.wireOp",EDGE,"E133.left"),sQuery(id+"F95.wireOp",EDGE,"E133.right")])]}),"instanceName":"1"}),"instanceName":"1"});
            var Q7;
            Q7=makeQuery(id+"F105.opPattern","COPY",BODY,{"derivedFrom":makeQuery(id+"F101.opPattern","COPY",BODY,{"derivedFrom":makeQuery(id+"F100.opPattern","COPY",BODY,{"derivedFrom":makeQuery(id+"F98.opExtrude","SWEPT_BODY",BODY,{"disambiguationData":[OSD([sQuery(id+"F97.wireOp",EDGE,"E134.bottom"),sQuery(id+"F97.wireOp",EDGE,"E134.top"),sQuery(id+"F97.wireOp",EDGE,"E134.left"),sQuery(id+"F97.wireOp",EDGE,"E134.right")])]}),"instanceName":"1"}),"instanceName":"1"}),"instanceName":"1"});
            var Q8;
            Q8=makeQuery(id+"F105.opPattern","COPY",BODY,{"derivedFrom":makeQuery(id+"F101.opPattern","COPY",BODY,{"derivedFrom":makeQuery(id+"F98.opExtrude","SWEPT_BODY",BODY,{"disambiguationData":[OSD([sQuery(id+"F97.wireOp",EDGE,"E134.bottom"),sQuery(id+"F97.wireOp",EDGE,"E134.top"),sQuery(id+"F97.wireOp",EDGE,"E134.left"),sQuery(id+"F97.wireOp",EDGE,"E134.right")])]}),"instanceName":"1"}),"instanceName":"1"});
            var Q9;
            Q9=makeQuery(id+"F101.opPattern","COPY",BODY,{"derivedFrom":makeQuery(id+"F96.opExtrude","SWEPT_BODY",BODY,{"disambiguationData":[OSD([sQuery(id+"F95.wireOp",EDGE,"E133.bottom"),sQuery(id+"F95.wireOp",EDGE,"E133.top"),sQuery(id+"F95.wireOp",EDGE,"E133.left"),sQuery(id+"F95.wireOp",EDGE,"E133.right")])]}),"instanceName":"1"});
            var Q10;
            Q10=makeQuery(id+"F101.opPattern","COPY",BODY,{"derivedFrom":makeQuery(id+"F100.opPattern","COPY",BODY,{"derivedFrom":makeQuery(id+"F98.opExtrude","SWEPT_BODY",BODY,{"disambiguationData":[OSD([sQuery(id+"F97.wireOp",EDGE,"E134.bottom"),sQuery(id+"F97.wireOp",EDGE,"E134.top"),sQuery(id+"F97.wireOp",EDGE,"E134.left"),sQuery(id+"F97.wireOp",EDGE,"E134.right")])]}),"instanceName":"1"}),"instanceName":"1"});
            var Q11;
            Q11=makeQuery(id+"F101.opPattern","COPY",BODY,{"derivedFrom":makeQuery(id+"F98.opExtrude","SWEPT_BODY",BODY,{"disambiguationData":[OSD([sQuery(id+"F97.wireOp",EDGE,"E134.bottom"),sQuery(id+"F97.wireOp",EDGE,"E134.top"),sQuery(id+"F97.wireOp",EDGE,"E134.left"),sQuery(id+"F97.wireOp",EDGE,"E134.right")])]}),"instanceName":"1"});
            var Q12;
            Q12=makeQuery(id+"F96.opExtrude","SWEPT_BODY",BODY,{"disambiguationData":[OSD([sQuery(id+"F95.wireOp",EDGE,"E133.bottom"),sQuery(id+"F95.wireOp",EDGE,"E133.top"),sQuery(id+"F95.wireOp",EDGE,"E133.left"),sQuery(id+"F95.wireOp",EDGE,"E133.right")])]});
            var Q13;
            Q13=makeQuery(id+"F100.opPattern","COPY",BODY,{"derivedFrom":makeQuery(id+"F98.opExtrude","SWEPT_BODY",BODY,{"disambiguationData":[OSD([sQuery(id+"F97.wireOp",EDGE,"E134.bottom"),sQuery(id+"F97.wireOp",EDGE,"E134.top"),sQuery(id+"F97.wireOp",EDGE,"E134.left"),sQuery(id+"F97.wireOp",EDGE,"E134.right")])]}),"instanceName":"1"});
            var Q14;
            Q14=makeQuery(id+"F98.opExtrude","SWEPT_BODY",BODY,{"disambiguationData":[OSD([sQuery(id+"F97.wireOp",EDGE,"E134.bottom"),sQuery(id+"F97.wireOp",EDGE,"E134.top"),sQuery(id+"F97.wireOp",EDGE,"E134.left"),sQuery(id+"F97.wireOp",EDGE,"E134.right")])]});
            var Q15;
            Q15=qCreatedBy(id+"F107.planeOp",FACE);
            mirror(context, id + "F108", {"entities" : qUnion([Q0, Q1, Q2, Q3, Q4, Q5, Q6, Q7, Q8, Q9, Q10, Q11, Q12, Q13, Q14]), "mirrorPlane" : qUnion([Q15])});
        }
        {
            var Q0;
            Q0=makeQuery(id+"F98.opExtrude","SWEPT_BODY",BODY,{"disambiguationData":[OSD([sQuery(id+"F97.wireOp",EDGE,"E134.bottom"),sQuery(id+"F97.wireOp",EDGE,"E134.top"),sQuery(id+"F97.wireOp",EDGE,"E134.left"),sQuery(id+"F97.wireOp",EDGE,"E134.right")])]});
            var Q1;
            Q1=makeQuery(id+"F96.opExtrude","SWEPT_BODY",BODY,{"disambiguationData":[OSD([sQuery(id+"F95.wireOp",EDGE,"E133.bottom"),sQuery(id+"F95.wireOp",EDGE,"E133.top"),sQuery(id+"F95.wireOp",EDGE,"E133.left"),sQuery(id+"F95.wireOp",EDGE,"E133.right")])]});
            var Q2;
            Q2=makeQuery(id+"F100.opPattern","COPY",BODY,{"derivedFrom":makeQuery(id+"F98.opExtrude","SWEPT_BODY",BODY,{"disambiguationData":[OSD([sQuery(id+"F97.wireOp",EDGE,"E134.bottom"),sQuery(id+"F97.wireOp",EDGE,"E134.top"),sQuery(id+"F97.wireOp",EDGE,"E134.left"),sQuery(id+"F97.wireOp",EDGE,"E134.right")])]}),"instanceName":"1"});
            var Q3;
            Q3=makeQuery(id+"F108.opPattern","COPY",BODY,{"derivedFrom":makeQuery(id+"F100.opPattern","COPY",BODY,{"derivedFrom":makeQuery(id+"F98.opExtrude","SWEPT_BODY",BODY,{"disambiguationData":[OSD([sQuery(id+"F97.wireOp",EDGE,"E134.bottom"),sQuery(id+"F97.wireOp",EDGE,"E134.top"),sQuery(id+"F97.wireOp",EDGE,"E134.left"),sQuery(id+"F97.wireOp",EDGE,"E134.right")])]}),"instanceName":"1"}),"instanceName":"1"});
            transform(context, id + "F109", {"entities" : qUnion([Q0, Q1, Q2, Q3]), "transformType" : TransformType.TRANSLATION_3D, "dx" : 0 * mm, "dy" : 0 * mm, "dz" : -430 * mm, "makeCopy" : true});
        }
        {
            var Q0;
            Q0=makeQuery(id+"F108.opPattern","COPY",BODY,{"derivedFrom":makeQuery(id+"F98.opExtrude","SWEPT_BODY",BODY,{"disambiguationData":[OSD([sQuery(id+"F97.wireOp",EDGE,"E134.bottom"),sQuery(id+"F97.wireOp",EDGE,"E134.top"),sQuery(id+"F97.wireOp",EDGE,"E134.left"),sQuery(id+"F97.wireOp",EDGE,"E134.right")])]}),"instanceName":"1"});
            var Q1;
            Q1=makeQuery(id+"F108.opPattern","COPY",BODY,{"derivedFrom":makeQuery(id+"F96.opExtrude","SWEPT_BODY",BODY,{"disambiguationData":[OSD([sQuery(id+"F95.wireOp",EDGE,"E133.bottom"),sQuery(id+"F95.wireOp",EDGE,"E133.top"),sQuery(id+"F95.wireOp",EDGE,"E133.left"),sQuery(id+"F95.wireOp",EDGE,"E133.right")])]}),"instanceName":"1"});
            transform(context, id + "F110", {"entities" : qUnion([Q0, Q1]), "transformType" : TransformType.TRANSLATION_3D, "dx" : 0 * mm, "dy" : 0 * mm, "dz" : -430 * mm, "makeCopy" : true});
        }
    });
